# Revit family: ALWT_приток
name_source: partatom
category: Воздухораспределители
revit_build: Autodesk Revit 2014 (Build: 20130308_1515(x64)
units: mm (PartAtom-declared; Revit-internal decimal feet)

## types (1863) — shared parameters
A = 52 мм
URL = http://inplast.ru
margins = 10 мм
Изготовитель = INPLAST-SMAY
Материал = Алюминий_RAL9016 (INPLAST)
Описание = Решетка ALWT-алюминиевая защитная, угол выхода потока 15°

## per-type parameters (varying)
| type | Aef | C | C' | D | D' | Step 1 | Step 2 | n1 | n2 | Тип крепежа |
| ALWT-100х100-RAL9016 | 0.006 м² | 100 мм | 95 мм | 100 мм | 96 мм | 18 мм | 64 мм | 10 | 2 | саморезы |
| ALWT-125х100-RAL9016 | 0.008 м² | 125 мм | 120 мм | 100 мм | 96 мм | 23 мм | 80 мм | 10 | 2 | саморезы |
| ALWT-125х125-RAL9016 | 0.009 м² | 125 мм | 120 мм | 125 мм | 121 мм | 23 мм | 80 мм | 13 | 2 | саморезы |
| ALWT-150х100-RAL9016 | 0.009 м² | 150 мм | 145 мм | 100 мм | 96 мм | 27 мм | 95 мм | 10 | 2 | саморезы |
| ALWT-150х125-RAL9016 | 0.011 м² | 150 мм | 145 мм | 125 мм | 121 мм | 27 мм | 95 мм | 13 | 2 | саморезы |
| ALWT-150х150-RAL9016 | 0.014 м² | 150 мм | 145 мм | 150 мм | 146 мм | 27 мм | 95 мм | 15 | 2 | саморезы |
| ALWT-200х100-RAL9016 | 0.012 м² | 200 мм | 195 мм | 100 мм | 96 мм | 36 мм | 127 мм | 10 | 2 | саморезы |
| ALWT-200х125-RAL9016 | 0.015 м² | 200 мм | 195 мм | 125 мм | 121 мм | 36 мм | 127 мм | 13 | 2 | саморезы |
| ALWT-200х150-RAL9016 | 0.018 м² | 200 мм | 195 мм | 150 мм | 146 мм | 36 мм | 127 мм | 15 | 2 | саморезы |
| ALWT-200х200-RAL9016 | 0.024 м² | 200 мм | 195 мм | 200 мм | 196 мм | 36 мм | 127 мм | 20 | 2 | саморезы |
| ALWT-225х100-RAL9016 | 0.014 м² | 225 мм | 220 мм | 100 мм | 96 мм | 41 мм | 143 мм | 10 | 2 | саморезы |
| ALWT-225х125-RAL9016 | 0.017 м² | 225 мм | 220 мм | 125 мм | 121 мм | 41 мм | 143 мм | 13 | 2 | саморезы |
| ALWT-225х150-RAL9016 | 0.020 м² | 225 мм | 220 мм | 150 мм | 146 мм | 41 мм | 143 мм | 15 | 2 | саморезы |
| ALWT-225х200-RAL9016 | 0.027 м² | 225 мм | 220 мм | 200 мм | 196 мм | 41 мм | 143 мм | 20 | 2 | саморезы |
| ALWT-225х225-RAL9016 | 0.030 м² | 225 мм | 220 мм | 225 мм | 221 мм | 41 мм | 143 мм | 23 | 2 | саморезы |
| ALWT-250х100-RAL9016 | 0.015 м² | 250 мм | 245 мм | 100 мм | 96 мм | 45 мм | 159 мм | 10 | 2 | саморезы |
| ALWT-250х125-RAL9016 | 0.019 м² | 250 мм | 245 мм | 125 мм | 121 мм | 45 мм | 159 мм | 13 | 2 | саморезы |
| ALWT-250х150-RAL9016 | 0.023 м² | 250 мм | 245 мм | 150 мм | 146 мм | 45 мм | 159 мм | 15 | 2 | саморезы |
| ALWT-250х200-RAL9016 | 0.030 м² | 250 мм | 245 мм | 200 мм | 196 мм | 45 мм | 159 мм | 20 | 2 | саморезы |
| ALWT-250х225-RAL9016 | 0.034 м² | 250 мм | 245 мм | 225 мм | 221 мм | 45 мм | 159 мм | 23 | 2 | саморезы |
| ALWT-250х250-RAL9016 | 0.038 м² | 250 мм | 245 мм | 250 мм | 246 мм | 45 мм | 159 мм | 25 | 2 | саморезы |
| ALWT-300х100-RAL9016 | 0.018 м² | 300 мм | 295 мм | 100 мм | 96 мм | 55 мм | 191 мм | 10 | 2 | саморезы |
| ALWT-300х125-RAL9016 | 0.023 м² | 300 мм | 295 мм | 125 мм | 121 мм | 55 мм | 191 мм | 13 | 2 | саморезы |
| ALWT-300х150-RAL9016 | 0.027 м² | 300 мм | 295 мм | 150 мм | 146 мм | 55 мм | 191 мм | 15 | 2 | саморезы |
| ALWT-300х200-RAL9016 | 0.036 м² | 300 мм | 295 мм | 200 мм | 196 мм | 55 мм | 191 мм | 20 | 2 | саморезы |
| ALWT-300х225-RAL9016 | 0.041 м² | 300 мм | 295 мм | 225 мм | 221 мм | 55 мм | 191 мм | 23 | 2 | саморезы |
| ALWT-300х250-RAL9016 | 0.045 м² | 300 мм | 295 мм | 250 мм | 246 мм | 55 мм | 191 мм | 25 | 2 | саморезы |
| ALWT-300х300-RAL9016 | 0.054 м² | 300 мм | 295 мм | 300 мм | 296 мм | 55 мм | 191 мм | 30 | 2 | саморезы |
| ALWT-325х100-RAL9016 | 0.020 м² | 325 мм | 320 мм | 100 мм | 96 мм | 59 мм | 207 мм | 10 | 2 | саморезы |
| ALWT-325х125-RAL9016 | 0.024 м² | 325 мм | 320 мм | 125 мм | 121 мм | 59 мм | 207 мм | 13 | 2 | саморезы |
| ALWT-325х150-RAL9016 | 0.029 м² | 325 мм | 320 мм | 150 мм | 146 мм | 59 мм | 207 мм | 15 | 2 | саморезы |
| ALWT-325х200-RAL9016 | 0.039 м² | 325 мм | 320 мм | 200 мм | 196 мм | 59 мм | 207 мм | 20 | 2 | саморезы |
| ALWT-325х225-RAL9016 | 0.044 м² | 325 мм | 320 мм | 225 мм | 221 мм | 59 мм | 207 мм | 23 | 2 | саморезы |
| ALWT-325х250-RAL9016 | 0.049 м² | 325 мм | 320 мм | 250 мм | 246 мм | 59 мм | 207 мм | 25 | 2 | саморезы |
| ALWT-325х300-RAL9016 | 0.059 м² | 325 мм | 320 мм | 300 мм | 296 мм | 59 мм | 207 мм | 30 | 2 | саморезы |
| ALWT-325х325-RAL9016 | 0.064 м² | 325 мм | 320 мм | 325 мм | 321 мм | 59 мм | 207 мм | 33 | 2 | саморезы |
| ALWT-350х100-RAL9016 | 0.021 м² | 350 мм | 345 мм | 100 мм | 96 мм | 64 мм | 223 мм | 10 | 2 | саморезы |
| ALWT-350х125-RAL9016 | 0.026 м² | 350 мм | 345 мм | 125 мм | 121 мм | 64 мм | 223 мм | 13 | 2 | саморезы |
| ALWT-350х150-RAL9016 | 0.032 м² | 350 мм | 345 мм | 150 мм | 146 мм | 64 мм | 223 мм | 15 | 2 | саморезы |
| ALWT-350х200-RAL9016 | 0.042 м² | 350 мм | 345 мм | 200 мм | 196 мм | 64 мм | 223 мм | 20 | 2 | саморезы |
| ALWT-350х225-RAL9016 | 0.047 м² | 350 мм | 345 мм | 225 мм | 221 мм | 64 мм | 223 мм | 23 | 2 | саморезы |
| ALWT-350х250-RAL9016 | 0.053 м² | 350 мм | 345 мм | 250 мм | 246 мм | 64 мм | 223 мм | 25 | 2 | саморезы |
| ALWT-350х300-RAL9016 | 0.063 м² | 350 мм | 345 мм | 300 мм | 296 мм | 64 мм | 223 мм | 30 | 2 | саморезы |
| ALWT-350х325-RAL9016 | 0.068 м² | 350 мм | 345 мм | 325 мм | 321 мм | 64 мм | 223 мм | 33 | 2 | саморезы |
| ALWT-350х350-RAL9016 | 0.074 м² | 350 мм | 345 мм | 350 мм | 346 мм | 64 мм | 223 мм | 35 | 2 | саморезы |
| ALWT-400х100-RAL9016 | 0.024 м² | 400 мм | 395 мм | 100 мм | 96 мм | 73 мм | 255 мм | 10 | 3 | саморезы |
| ALWT-400х125-RAL9016 | 0.030 м² | 400 мм | 395 мм | 125 мм | 121 мм | 73 мм | 255 мм | 13 | 3 | саморезы |
| ALWT-400х150-RAL9016 | 0.036 м² | 400 мм | 395 мм | 150 мм | 146 мм | 73 мм | 255 мм | 15 | 3 | саморезы |
| ALWT-400х200-RAL9016 | 0.048 м² | 400 мм | 395 мм | 200 мм | 196 мм | 73 мм | 255 мм | 20 | 3 | саморезы |
| ALWT-400х225-RAL9016 | 0.054 м² | 400 мм | 395 мм | 225 мм | 221 мм | 73 мм | 255 мм | 23 | 3 | саморезы |
| ALWT-400х250-RAL9016 | 0.060 м² | 400 мм | 395 мм | 250 мм | 246 мм | 73 мм | 255 мм | 25 | 3 | саморезы |
| ALWT-400х300-RAL9016 | 0.072 м² | 400 мм | 395 мм | 300 мм | 296 мм | 73 мм | 255 мм | 30 | 3 | саморезы |
| ALWT-400х325-RAL9016 | 0.078 м² | 400 мм | 395 мм | 325 мм | 321 мм | 73 мм | 255 мм | 33 | 3 | саморезы |
| ALWT-400х350-RAL9016 | 0.084 м² | 400 мм | 395 мм | 350 мм | 346 мм | 73 мм | 255 мм | 35 | 3 | саморезы |
| ALWT-400х400-RAL9016 | 0.096 м² | 400 мм | 395 мм | 400 мм | 396 мм | 73 мм | 255 мм | 40 | 3 | саморезы |
| ALWT-425х100-RAL9016 | 0.026 м² | 425 мм | 420 мм | 100 мм | 96 мм | 77 мм | 270 мм | 10 | 3 | саморезы |
| ALWT-425х125-RAL9016 | 0.032 м² | 425 мм | 420 мм | 125 мм | 121 мм | 77 мм | 270 мм | 13 | 3 | саморезы |
| ALWT-425х150-RAL9016 | 0.038 м² | 425 мм | 420 мм | 150 мм | 146 мм | 77 мм | 270 мм | 15 | 3 | саморезы |
| ALWT-425х200-RAL9016 | 0.051 м² | 425 мм | 420 мм | 200 мм | 196 мм | 77 мм | 270 мм | 20 | 3 | саморезы |
| ALWT-425х225-RAL9016 | 0.058 м² | 425 мм | 420 мм | 225 мм | 221 мм | 77 мм | 270 мм | 23 | 3 | саморезы |
| ALWT-425х250-RAL9016 | 0.064 м² | 425 мм | 420 мм | 250 мм | 246 мм | 77 мм | 270 мм | 25 | 3 | саморезы |
| ALWT-425х300-RAL9016 | 0.077 м² | 425 мм | 420 мм | 300 мм | 296 мм | 77 мм | 270 мм | 30 | 3 | саморезы |
| ALWT-425х325-RAL9016 | 0.083 м² | 425 мм | 420 мм | 325 мм | 321 мм | 77 мм | 270 мм | 33 | 3 | саморезы |
| ALWT-425х350-RAL9016 | 0.089 м² | 425 мм | 420 мм | 350 мм | 346 мм | 77 мм | 270 мм | 35 | 3 | саморезы |
| ALWT-425х400-RAL9016 | 0.102 м² | 425 мм | 420 мм | 400 мм | 396 мм | 77 мм | 270 мм | 40 | 3 | саморезы |
| ALWT-425х425-RAL9016 | 0.109 м² | 425 мм | 420 мм | 425 мм | 421 мм | 77 мм | 270 мм | 43 | 3 | саморезы |
| ALWT-450х100-RAL9016 | 0.027 м² | 450 мм | 445 мм | 100 мм | 96 мм | 82 мм | 286 мм | 10 | 3 | саморезы |
| ALWT-450х125-RAL9016 | 0.034 м² | 450 мм | 445 мм | 125 мм | 121 мм | 82 мм | 286 мм | 13 | 3 | саморезы |
| ALWT-450х150-RAL9016 | 0.041 м² | 450 мм | 445 мм | 150 мм | 146 мм | 82 мм | 286 мм | 15 | 3 | саморезы |
| ALWT-450х200-RAL9016 | 0.054 м² | 450 мм | 445 мм | 200 мм | 196 мм | 82 мм | 286 мм | 20 | 3 | саморезы |
| ALWT-450х225-RAL9016 | 0.061 м² | 450 мм | 445 мм | 225 мм | 221 мм | 82 мм | 286 мм | 23 | 3 | саморезы |
| ALWT-450х250-RAL9016 | 0.068 м² | 450 мм | 445 мм | 250 мм | 246 мм | 82 мм | 286 мм | 25 | 3 | саморезы |
| ALWT-450х300-RAL9016 | 0.081 м² | 450 мм | 445 мм | 300 мм | 296 мм | 82 мм | 286 мм | 30 | 3 | саморезы |
| ALWT-450х325-RAL9016 | 0.088 м² | 450 мм | 445 мм | 325 мм | 321 мм | 82 мм | 286 мм | 33 | 3 | саморезы |
| ALWT-450х350-RAL9016 | 0.095 м² | 450 мм | 445 мм | 350 мм | 346 мм | 82 мм | 286 мм | 35 | 3 | саморезы |
| ALWT-450х400-RAL9016 | 0.108 м² | 450 мм | 445 мм | 400 мм | 396 мм | 82 мм | 286 мм | 40 | 3 | саморезы |
| ALWT-450х425-RAL9016 | 0.115 м² | 450 мм | 445 мм | 425 мм | 421 мм | 82 мм | 286 мм | 43 | 3 | саморезы |
| ALWT-450х450-RAL9016 | 0.122 м² | 450 мм | 445 мм | 450 мм | 446 мм | 82 мм | 286 мм | 45 | 3 | саморезы |
| ALWT-500х100-RAL9016 | 0.030 м² | 500 мм | 495 мм | 100 мм | 96 мм | 91 мм | 318 мм | 10 | 3 | саморезы |
| ALWT-500х125-RAL9016 | 0.038 м² | 500 мм | 495 мм | 125 мм | 121 мм | 91 мм | 318 мм | 13 | 3 | саморезы |
| ALWT-500х150-RAL9016 | 0.045 м² | 500 мм | 495 мм | 150 мм | 146 мм | 91 мм | 318 мм | 15 | 3 | саморезы |
| ALWT-500х200-RAL9016 | 0.060 м² | 500 мм | 495 мм | 200 мм | 196 мм | 91 мм | 318 мм | 20 | 3 | саморезы |
| ALWT-500х225-RAL9016 | 0.068 м² | 500 мм | 495 мм | 225 мм | 221 мм | 91 мм | 318 мм | 23 | 3 | саморезы |
| ALWT-500х250-RAL9016 | 0.075 м² | 500 мм | 495 мм | 250 мм | 246 мм | 91 мм | 318 мм | 25 | 3 | саморезы |
| ALWT-500х300-RAL9016 | 0.090 м² | 500 мм | 495 мм | 300 мм | 296 мм | 91 мм | 318 мм | 30 | 3 | саморезы |
| ALWT-500х325-RAL9016 | 0.098 м² | 500 мм | 495 мм | 325 мм | 321 мм | 91 мм | 318 мм | 33 | 3 | саморезы |
| ALWT-500х350-RAL9016 | 0.105 м² | 500 мм | 495 мм | 350 мм | 346 мм | 91 мм | 318 мм | 35 | 3 | саморезы |
| ALWT-500х400-RAL9016 | 0.120 м² | 500 мм | 495 мм | 400 мм | 396 мм | 91 мм | 318 мм | 40 | 3 | саморезы |
| ALWT-500х425-RAL9016 | 0.128 м² | 500 мм | 495 мм | 425 мм | 421 мм | 91 мм | 318 мм | 43 | 3 | саморезы |
| ALWT-500х450-RAL9016 | 0.135 м² | 500 мм | 495 мм | 450 мм | 446 мм | 91 мм | 318 мм | 45 | 3 | саморезы |
| ALWT-500х500-RAL9016 | 0.150 м² | 500 мм | 495 мм | 500 мм | 496 мм | 91 мм | 318 мм | 50 | 3 | саморезы |
| ALWT-525х100-RAL9016 | 0.032 м² | 525 мм | 520 мм | 100 мм | 96 мм | 95 мм | 334 мм | 10 | 3 | саморезы |
| ALWT-525х125-RAL9016 | 0.039 м² | 525 мм | 520 мм | 125 мм | 121 мм | 95 мм | 334 мм | 13 | 3 | саморезы |
| ALWT-525х150-RAL9016 | 0.047 м² | 525 мм | 520 мм | 150 мм | 146 мм | 95 мм | 334 мм | 15 | 3 | саморезы |
| ALWT-525х200-RAL9016 | 0.063 м² | 525 мм | 520 мм | 200 мм | 196 мм | 95 мм | 334 мм | 20 | 3 | саморезы |
| ALWT-525х225-RAL9016 | 0.071 м² | 525 мм | 520 мм | 225 мм | 221 мм | 95 мм | 334 мм | 23 | 3 | саморезы |
| ALWT-525х250-RAL9016 | 0.079 м² | 525 мм | 520 мм | 250 мм | 246 мм | 95 мм | 334 мм | 25 | 3 | саморезы |
| ALWT-525х300-RAL9016 | 0.095 м² | 525 мм | 520 мм | 300 мм | 296 мм | 95 мм | 334 мм | 30 | 3 | саморезы |
| ALWT-525х325-RAL9016 | 0.103 м² | 525 мм | 520 мм | 325 мм | 321 мм | 95 мм | 334 мм | 33 | 3 | саморезы |
| ALWT-525х350-RAL9016 | 0.111 м² | 525 мм | 520 мм | 350 мм | 346 мм | 95 мм | 334 мм | 35 | 3 | саморезы |
| ALWT-525х400-RAL9016 | 0.126 м² | 525 мм | 520 мм | 400 мм | 396 мм | 95 мм | 334 мм | 40 | 3 | саморезы |
| ALWT-525х425-RAL9016 | 0.134 м² | 525 мм | 520 мм | 425 мм | 421 мм | 95 мм | 334 мм | 43 | 3 | саморезы |
| ALWT-525х450-RAL9016 | 0.142 м² | 525 мм | 520 мм | 450 мм | 446 мм | 95 мм | 334 мм | 45 | 3 | саморезы |
| ALWT-525х500-RAL9016 | 0.158 м² | 525 мм | 520 мм | 500 мм | 496 мм | 95 мм | 334 мм | 50 | 3 | саморезы |
| ALWT-525х525-RAL9016 | 0.166 м² | 525 мм | 520 мм | 525 мм | 521 мм | 95 мм | 334 мм | 53 | 3 | саморезы |
| ALWT-550х100-RAL9016 | 0.033 м² | 550 мм | 545 мм | 100 мм | 96 мм | 100 мм | 350 мм | 10 | 3 | саморезы |
| ALWT-550х125-RAL9016 | 0.041 м² | 550 мм | 545 мм | 125 мм | 121 мм | 100 мм | 350 мм | 13 | 3 | саморезы |
| ALWT-550х150-RAL9016 | 0.050 м² | 550 мм | 545 мм | 150 мм | 146 мм | 100 мм | 350 мм | 15 | 3 | саморезы |
| ALWT-550х200-RAL9016 | 0.066 м² | 550 мм | 545 мм | 200 мм | 196 мм | 100 мм | 350 мм | 20 | 3 | саморезы |
| ALWT-550х225-RAL9016 | 0.074 м² | 550 мм | 545 мм | 225 мм | 221 мм | 100 мм | 350 мм | 23 | 3 | саморезы |
| ALWT-550х250-RAL9016 | 0.083 м² | 550 мм | 545 мм | 250 мм | 246 мм | 100 мм | 350 мм | 25 | 3 | саморезы |
| ALWT-550х300-RAL9016 | 0.099 м² | 550 мм | 545 мм | 300 мм | 296 мм | 100 мм | 350 мм | 30 | 3 | саморезы |
| ALWT-550х325-RAL9016 | 0.108 м² | 550 мм | 545 мм | 325 мм | 321 мм | 100 мм | 350 мм | 33 | 3 | саморезы |
| ALWT-550х350-RAL9016 | 0.116 м² | 550 мм | 545 мм | 350 мм | 346 мм | 100 мм | 350 мм | 35 | 3 | саморезы |
| ALWT-550х400-RAL9016 | 0.132 м² | 550 мм | 545 мм | 400 мм | 396 мм | 100 мм | 350 мм | 40 | 3 | саморезы |
| ALWT-550х425-RAL9016 | 0.141 м² | 550 мм | 545 мм | 425 мм | 421 мм | 100 мм | 350 мм | 43 | 3 | саморезы |
| ALWT-550х450-RAL9016 | 0.149 м² | 550 мм | 545 мм | 450 мм | 446 мм | 100 мм | 350 мм | 45 | 3 | саморезы |
| ALWT-550х500-RAL9016 | 0.165 м² | 550 мм | 545 мм | 500 мм | 496 мм | 100 мм | 350 мм | 50 | 3 | саморезы |
| ALWT-550х525-RAL9016 | 0.174 м² | 550 мм | 545 мм | 525 мм | 521 мм | 100 мм | 350 мм | 53 | 3 | саморезы |
| ALWT-550х550-RAL9016 | 0.182 м² | 550 мм | 545 мм | 550 мм | 546 мм | 100 мм | 350 мм | 55 | 3 | саморезы |
| ALWT-600х100-RAL9016 | 0.036 м² | 600 мм | 595 мм | 100 мм | 96 мм | 109 мм | 382 мм | 10 | 3 | саморезы |
| ALWT-600х125-RAL9016 | 0.045 м² | 600 мм | 595 мм | 125 мм | 121 мм | 109 мм | 382 мм | 13 | 3 | саморезы |
| ALWT-600х150-RAL9016 | 0.054 м² | 600 мм | 595 мм | 150 мм | 146 мм | 109 мм | 382 мм | 15 | 3 | саморезы |
| ALWT-600х200-RAL9016 | 0.072 м² | 600 мм | 595 мм | 200 мм | 196 мм | 109 мм | 382 мм | 20 | 3 | саморезы |
| ALWT-600х225-RAL9016 | 0.081 м² | 600 мм | 595 мм | 225 мм | 221 мм | 109 мм | 382 мм | 23 | 3 | саморезы |
| ALWT-600х250-RAL9016 | 0.090 м² | 600 мм | 595 мм | 250 мм | 246 мм | 109 мм | 382 мм | 25 | 3 | саморезы |
| ALWT-600х300-RAL9016 | 0.108 м² | 600 мм | 595 мм | 300 мм | 296 мм | 109 мм | 382 мм | 30 | 3 | саморезы |
| ALWT-600х325-RAL9016 | 0.117 м² | 600 мм | 595 мм | 325 мм | 321 мм | 109 мм | 382 мм | 33 | 3 | саморезы |
| ALWT-600х350-RAL9016 | 0.126 м² | 600 мм | 595 мм | 350 мм | 346 мм | 109 мм | 382 мм | 35 | 3 | саморезы |
| ALWT-600х400-RAL9016 | 0.144 м² | 600 мм | 595 мм | 400 мм | 396 мм | 109 мм | 382 мм | 40 | 3 | саморезы |
| ALWT-600х425-RAL9016 | 0.153 м² | 600 мм | 595 мм | 425 мм | 421 мм | 109 мм | 382 мм | 43 | 3 | саморезы |
| ALWT-600х450-RAL9016 | 0.162 м² | 600 мм | 595 мм | 450 мм | 446 мм | 109 мм | 382 мм | 45 | 3 | саморезы |
| ALWT-600х500-RAL9016 | 0.180 м² | 600 мм | 595 мм | 500 мм | 496 мм | 109 мм | 382 мм | 50 | 3 | саморезы |
| ALWT-600х525-RAL9016 | 0.190 м² | 600 мм | 595 мм | 525 мм | 521 мм | 109 мм | 382 мм | 53 | 3 | саморезы |
| ALWT-600х550-RAL9016 | 0.199 м² | 600 мм | 595 мм | 550 мм | 546 мм | 109 мм | 382 мм | 55 | 3 | саморезы |
| ALWT-600х600-RAL9016 | 0.217 м² | 600 мм | 595 мм | 600 мм | 596 мм | 109 мм | 382 мм | 60 | 3 | саморезы |
| ALWT-625х100-RAL9016 | 0.038 м² | 625 мм | 620 мм | 100 мм | 96 мм | 114 мм | 398 мм | 10 | 3 | саморезы |
| ALWT-625х125-RAL9016 | 0.047 м² | 625 мм | 620 мм | 125 мм | 121 мм | 114 мм | 398 мм | 13 | 3 | саморезы |
| ALWT-625х150-RAL9016 | 0.056 м² | 625 мм | 620 мм | 150 мм | 146 мм | 114 мм | 398 мм | 15 | 3 | саморезы |
| ALWT-625х200-RAL9016 | 0.075 м² | 625 мм | 620 мм | 200 мм | 196 мм | 114 мм | 398 мм | 20 | 3 | саморезы |
| ALWT-625х225-RAL9016 | 0.085 м² | 625 мм | 620 мм | 225 мм | 221 мм | 114 мм | 398 мм | 23 | 3 | саморезы |
| ALWT-625х250-RAL9016 | 0.094 м² | 625 мм | 620 мм | 250 мм | 246 мм | 114 мм | 398 мм | 25 | 3 | саморезы |
| ALWT-625х300-RAL9016 | 0.113 м² | 625 мм | 620 мм | 300 мм | 296 мм | 114 мм | 398 мм | 30 | 3 | саморезы |
| ALWT-625х325-RAL9016 | 0.122 м² | 625 мм | 620 мм | 325 мм | 321 мм | 114 мм | 398 мм | 33 | 3 | саморезы |
| ALWT-625х350-RAL9016 | 0.132 м² | 625 мм | 620 мм | 350 мм | 346 мм | 114 мм | 398 мм | 35 | 3 | саморезы |
| ALWT-625х400-RAL9016 | 0.150 м² | 625 мм | 620 мм | 400 мм | 396 мм | 114 мм | 398 мм | 40 | 3 | саморезы |
| ALWT-625х425-RAL9016 | 0.160 м² | 625 мм | 620 мм | 425 мм | 421 мм | 114 мм | 398 мм | 43 | 3 | саморезы |
| ALWT-625х450-RAL9016 | 0.169 м² | 625 мм | 620 мм | 450 мм | 446 мм | 114 мм | 398 мм | 45 | 3 | саморезы |
| ALWT-625х500-RAL9016 | 0.188 м² | 625 мм | 620 мм | 500 мм | 496 мм | 114 мм | 398 мм | 50 | 3 | саморезы |
| ALWT-625х525-RAL9016 | 0.197 м² | 625 мм | 620 мм | 525 мм | 521 мм | 114 мм | 398 мм | 53 | 3 | саморезы |
| ALWT-625х550-RAL9016 | 0.207 м² | 625 мм | 620 мм | 550 мм | 546 мм | 114 мм | 398 мм | 55 | 3 | саморезы |
| ALWT-625х600-RAL9016 | 0.226 м² | 625 мм | 620 мм | 600 мм | 596 мм | 114 мм | 398 мм | 60 | 3 | саморезы |
| ALWT-625х625-RAL9016 | 0.235 м² | 625 мм | 620 мм | 625 мм | 621 мм | 114 мм | 398 мм | 63 | 3 | саморезы |
| ALWT-650х100-RAL9016 | 0.039 м² | 650 мм | 645 мм | 100 мм | 96 мм | 118 мм | 414 мм | 10 | 3 | саморезы |
| ALWT-650х125-RAL9016 | 0.049 м² | 650 мм | 645 мм | 125 мм | 121 мм | 118 мм | 414 мм | 13 | 3 | саморезы |
| ALWT-650х150-RAL9016 | 0.059 м² | 650 мм | 645 мм | 150 мм | 146 мм | 118 мм | 414 мм | 15 | 3 | саморезы |
| ALWT-650х200-RAL9016 | 0.078 м² | 650 мм | 645 мм | 200 мм | 196 мм | 118 мм | 414 мм | 20 | 3 | саморезы |
| ALWT-650х225-RAL9016 | 0.088 м² | 650 мм | 645 мм | 225 мм | 221 мм | 118 мм | 414 мм | 23 | 3 | саморезы |
| ALWT-650х250-RAL9016 | 0.098 м² | 650 мм | 645 мм | 250 мм | 246 мм | 118 мм | 414 мм | 25 | 3 | саморезы |
| ALWT-650х300-RAL9016 | 0.117 м² | 650 мм | 645 мм | 300 мм | 296 мм | 118 мм | 414 мм | 30 | 3 | саморезы |
| ALWT-650х325-RAL9016 | 0.127 м² | 650 мм | 645 мм | 325 мм | 321 мм | 118 мм | 414 мм | 33 | 3 | саморезы |
| ALWT-650х350-RAL9016 | 0.137 м² | 650 мм | 645 мм | 350 мм | 346 мм | 118 мм | 414 мм | 35 | 3 | саморезы |
| ALWT-650х400-RAL9016 | 0.156 м² | 650 мм | 645 мм | 400 мм | 396 мм | 118 мм | 414 мм | 40 | 3 | саморезы |
| ALWT-650х425-RAL9016 | 0.166 м² | 650 мм | 645 мм | 425 мм | 421 мм | 118 мм | 414 мм | 43 | 3 | саморезы |
| ALWT-650х450-RAL9016 | 0.176 м² | 650 мм | 645 мм | 450 мм | 446 мм | 118 мм | 414 мм | 45 | 3 | саморезы |
| ALWT-650х500-RAL9016 | 0.196 м² | 650 мм | 645 мм | 500 мм | 496 мм | 118 мм | 414 мм | 50 | 3 | саморезы |
| ALWT-650х525-RAL9016 | 0.205 м² | 650 мм | 645 мм | 525 мм | 521 мм | 118 мм | 414 мм | 53 | 3 | саморезы |
| ALWT-650х550-RAL9016 | 0.215 м² | 650 мм | 645 мм | 550 мм | 546 мм | 118 мм | 414 мм | 55 | 3 | саморезы |
| ALWT-650х600-RAL9016 | 0.235 м² | 650 мм | 645 мм | 600 мм | 596 мм | 118 мм | 414 мм | 60 | 3 | саморезы |
| ALWT-650х625-RAL9016 | 0.244 м² | 650 мм | 645 мм | 625 мм | 621 мм | 118 мм | 414 мм | 63 | 3 | саморезы |
| ALWT-650х650-RAL9016 | 0.254 м² | 650 мм | 645 мм | 650 мм | 646 мм | 118 мм | 414 мм | 65 | 3 | саморезы |
| ALWT-700х100-RAL9016 | 0.042 м² | 700 мм | 695 мм | 100 мм | 96 мм | 127 мм | 445 мм | 10 | 3 | саморезы |
| ALWT-700х125-RAL9016 | 0.053 м² | 700 мм | 695 мм | 125 мм | 121 мм | 127 мм | 445 мм | 13 | 3 | саморезы |
| ALWT-700х150-RAL9016 | 0.063 м² | 700 мм | 695 мм | 150 мм | 146 мм | 127 мм | 445 мм | 15 | 3 | саморезы |
| ALWT-700х200-RAL9016 | 0.084 м² | 700 мм | 695 мм | 200 мм | 196 мм | 127 мм | 445 мм | 20 | 3 | саморезы |
| ALWT-700х225-RAL9016 | 0.095 м² | 700 мм | 695 мм | 225 мм | 221 мм | 127 мм | 445 мм | 23 | 3 | саморезы |
| ALWT-700х250-RAL9016 | 0.105 м² | 700 мм | 695 мм | 250 мм | 246 мм | 127 мм | 445 мм | 25 | 3 | саморезы |
| ALWT-700х300-RAL9016 | 0.126 м² | 700 мм | 695 мм | 300 мм | 296 мм | 127 мм | 445 мм | 30 | 3 | саморезы |
| ALWT-700х325-RAL9016 | 0.137 м² | 700 мм | 695 мм | 325 мм | 321 мм | 127 мм | 445 мм | 33 | 3 | саморезы |
| ALWT-700х350-RAL9016 | 0.147 м² | 700 мм | 695 мм | 350 мм | 346 мм | 127 мм | 445 мм | 35 | 3 | саморезы |
| ALWT-700х400-RAL9016 | 0.168 м² | 700 мм | 695 мм | 400 мм | 396 мм | 127 мм | 445 мм | 40 | 3 | саморезы |
| ALWT-700х425-RAL9016 | 0.179 м² | 700 мм | 695 мм | 425 мм | 421 мм | 127 мм | 445 мм | 43 | 3 | саморезы |
| ALWT-700х450-RAL9016 | 0.190 м² | 700 мм | 695 мм | 450 мм | 446 мм | 127 мм | 445 мм | 45 | 3 | саморезы |
| ALWT-700х500-RAL9016 | 0.211 м² | 700 мм | 695 мм | 500 мм | 496 мм | 127 мм | 445 мм | 50 | 3 | саморезы |
| ALWT-700х525-RAL9016 | 0.221 м² | 700 мм | 695 мм | 525 мм | 521 мм | 127 мм | 445 мм | 53 | 3 | саморезы |
| ALWT-700х550-RAL9016 | 0.232 м² | 700 мм | 695 мм | 550 мм | 546 мм | 127 мм | 445 мм | 55 | 3 | саморезы |
| ALWT-700х600-RAL9016 | 0.253 м² | 700 мм | 695 мм | 600 мм | 596 мм | 127 мм | 445 мм | 60 | 3 | саморезы |
| ALWT-700х625-RAL9016 | 0.263 м² | 700 мм | 695 мм | 625 мм | 621 мм | 127 мм | 445 мм | 63 | 3 | саморезы |
| ALWT-700х650-RAL9016 | 0.274 м² | 700 мм | 695 мм | 650 мм | 646 мм | 127 мм | 445 мм | 65 | 3 | саморезы |
| ALWT-725х100-RAL9016 | 0.044 м² | 725 мм | 720 мм | 100 мм | 96 мм | 132 мм | 461 мм | 10 | 3 | саморезы |
| ALWT-725х125-RAL9016 | 0.055 м² | 725 мм | 720 мм | 125 мм | 121 мм | 132 мм | 461 мм | 13 | 3 | саморезы |
| ALWT-725х150-RAL9016 | 0.065 м² | 725 мм | 720 мм | 150 мм | 146 мм | 132 мм | 461 мм | 15 | 3 | саморезы |
| ALWT-725х200-RAL9016 | 0.087 м² | 725 мм | 720 мм | 200 мм | 196 мм | 132 мм | 461 мм | 20 | 3 | саморезы |
| ALWT-725х225-RAL9016 | 0.098 м² | 725 мм | 720 мм | 225 мм | 221 мм | 132 мм | 461 мм | 23 | 3 | саморезы |
| ALWT-725х250-RAL9016 | 0.109 м² | 725 мм | 720 мм | 250 мм | 246 мм | 132 мм | 461 мм | 25 | 3 | саморезы |
| ALWT-725х300-RAL9016 | 0.131 м² | 725 мм | 720 мм | 300 мм | 296 мм | 132 мм | 461 мм | 30 | 3 | саморезы |
| ALWT-725х325-RAL9016 | 0.142 м² | 725 мм | 720 мм | 325 мм | 321 мм | 132 мм | 461 мм | 33 | 3 | саморезы |
| ALWT-725х350-RAL9016 | 0.153 м² | 725 мм | 720 мм | 350 мм | 346 мм | 132 мм | 461 мм | 35 | 3 | саморезы |
| ALWT-725х400-RAL9016 | 0.174 м² | 725 мм | 720 мм | 400 мм | 396 мм | 132 мм | 461 мм | 40 | 3 | саморезы |
| ALWT-725х425-RAL9016 | 0.185 м² | 725 мм | 720 мм | 425 мм | 421 мм | 132 мм | 461 мм | 43 | 3 | саморезы |
| ALWT-725х450-RAL9016 | 0.196 м² | 725 мм | 720 мм | 450 мм | 446 мм | 132 мм | 461 мм | 45 | 3 | саморезы |
| ALWT-725х500-RAL9016 | 0.218 м² | 725 мм | 720 мм | 500 мм | 496 мм | 132 мм | 461 мм | 50 | 3 | саморезы |
| ALWT-725х525-RAL9016 | 0.229 м² | 725 мм | 720 мм | 525 мм | 521 мм | 132 мм | 461 мм | 53 | 3 | саморезы |
| ALWT-725х550-RAL9016 | 0.240 м² | 725 мм | 720 мм | 550 мм | 546 мм | 132 мм | 461 мм | 55 | 3 | саморезы |
| ALWT-725х600-RAL9016 | 0.262 м² | 725 мм | 720 мм | 600 мм | 596 мм | 132 мм | 461 мм | 60 | 3 | саморезы |
| ALWT-725х625-RAL9016 | 0.273 м² | 725 мм | 720 мм | 625 мм | 621 мм | 132 мм | 461 мм | 63 | 3 | саморезы |
| ALWT-725х650-RAL9016 | 0.284 м² | 725 мм | 720 мм | 650 мм | 646 мм | 132 мм | 461 мм | 65 | 3 | саморезы |
| ALWT-750х100-RAL9016 | 0.045 м² | 750 мм | 745 мм | 100 мм | 96 мм | 136 мм | 477 мм | 10 | 3 | саморезы |
| ALWT-750х125-RAL9016 | 0.056 м² | 750 мм | 745 мм | 125 мм | 121 мм | 136 мм | 477 мм | 13 | 3 | саморезы |
| ALWT-750х150-RAL9016 | 0.068 м² | 750 мм | 745 мм | 150 мм | 146 мм | 136 мм | 477 мм | 15 | 3 | саморезы |
| ALWT-750х200-RAL9016 | 0.090 м² | 750 мм | 745 мм | 200 мм | 196 мм | 136 мм | 477 мм | 20 | 3 | саморезы |
| ALWT-750х225-RAL9016 | 0.102 м² | 750 мм | 745 мм | 225 мм | 221 мм | 136 мм | 477 мм | 23 | 3 | саморезы |
| ALWT-750х250-RAL9016 | 0.113 м² | 750 мм | 745 мм | 250 мм | 246 мм | 136 мм | 477 мм | 25 | 3 | саморезы |
| ALWT-750х300-RAL9016 | 0.135 м² | 750 мм | 745 мм | 300 мм | 296 мм | 136 мм | 477 мм | 30 | 3 | саморезы |
| ALWT-750х325-RAL9016 | 0.147 м² | 750 мм | 745 мм | 325 мм | 321 мм | 136 мм | 477 мм | 33 | 3 | саморезы |
| ALWT-750х350-RAL9016 | 0.158 м² | 750 мм | 745 мм | 350 мм | 346 мм | 136 мм | 477 мм | 35 | 3 | саморезы |
| ALWT-750х400-RAL9016 | 0.180 м² | 750 мм | 745 мм | 400 мм | 396 мм | 136 мм | 477 мм | 40 | 3 | саморезы |
| ALWT-750х425-RAL9016 | 0.192 м² | 750 мм | 745 мм | 425 мм | 421 мм | 136 мм | 477 мм | 43 | 3 | саморезы |
| ALWT-750х450-RAL9016 | 0.203 м² | 750 мм | 745 мм | 450 мм | 446 мм | 136 мм | 477 мм | 45 | 3 | саморезы |
| ALWT-750х500-RAL9016 | 0.226 м² | 750 мм | 745 мм | 500 мм | 496 мм | 136 мм | 477 мм | 50 | 3 | саморезы |
| ALWT-750х525-RAL9016 | 0.237 м² | 750 мм | 745 мм | 525 мм | 521 мм | 136 мм | 477 мм | 53 | 3 | саморезы |
| ALWT-750х550-RAL9016 | 0.248 м² | 750 мм | 745 мм | 550 мм | 546 мм | 136 мм | 477 мм | 55 | 3 | саморезы |
| ALWT-750х600-RAL9016 | 0.271 м² | 750 мм | 745 мм | 600 мм | 596 мм | 136 мм | 477 мм | 60 | 3 | саморезы |
| ALWT-750х625-RAL9016 | 0.282 м² | 750 мм | 745 мм | 625 мм | 621 мм | 136 мм | 477 мм | 63 | 3 | саморезы |
| ALWT-750х650-RAL9016 | 0.293 м² | 750 мм | 745 мм | 650 мм | 646 мм | 136 мм | 477 мм | 65 | 3 | саморезы |
| ALWT-800х100-RAL9016 | 0.048 м² | 800 мм | 795 мм | 100 мм | 96 мм | 145 мм | 509 мм | 10 | 4 | саморезы |
| ALWT-800х125-RAL9016 | 0.060 м² | 800 мм | 795 мм | 125 мм | 121 мм | 145 мм | 509 мм | 13 | 4 | саморезы |
| ALWT-800х150-RAL9016 | 0.072 м² | 800 мм | 795 мм | 150 мм | 146 мм | 145 мм | 509 мм | 15 | 4 | саморезы |
| ALWT-800х200-RAL9016 | 0.096 м² | 800 мм | 795 мм | 200 мм | 196 мм | 145 мм | 509 мм | 20 | 4 | саморезы |
| ALWT-800х225-RAL9016 | 0.108 м² | 800 мм | 795 мм | 225 мм | 221 мм | 145 мм | 509 мм | 23 | 4 | саморезы |
| ALWT-800х250-RAL9016 | 0.120 м² | 800 мм | 795 мм | 250 мм | 246 мм | 145 мм | 509 мм | 25 | 4 | саморезы |
| ALWT-800х300-RAL9016 | 0.144 м² | 800 мм | 795 мм | 300 мм | 296 мм | 145 мм | 509 мм | 30 | 4 | саморезы |
| ALWT-800х325-RAL9016 | 0.156 м² | 800 мм | 795 мм | 325 мм | 321 мм | 145 мм | 509 мм | 33 | 4 | саморезы |
| ALWT-800х350-RAL9016 | 0.168 м² | 800 мм | 795 мм | 350 мм | 346 мм | 145 мм | 509 мм | 35 | 4 | саморезы |
| ALWT-800х400-RAL9016 | 0.193 м² | 800 мм | 795 мм | 400 мм | 396 мм | 145 мм | 509 мм | 40 | 4 | саморезы |
| ALWT-800х425-RAL9016 | 0.205 м² | 800 мм | 795 мм | 425 мм | 421 мм | 145 мм | 509 мм | 43 | 4 | саморезы |
| ALWT-800х450-RAL9016 | 0.217 м² | 800 мм | 795 мм | 450 мм | 446 мм | 145 мм | 509 мм | 45 | 4 | саморезы |
| ALWT-800х500-RAL9016 | 0.241 м² | 800 мм | 795 мм | 500 мм | 496 мм | 145 мм | 509 мм | 50 | 4 | саморезы |
| ALWT-800х525-RAL9016 | 0.253 м² | 800 мм | 795 мм | 525 мм | 521 мм | 145 мм | 509 мм | 53 | 4 | саморезы |
| ALWT-800х550-RAL9016 | 0.265 м² | 800 мм | 795 мм | 550 мм | 546 мм | 145 мм | 509 мм | 55 | 4 | саморезы |
| ALWT-800х600-RAL9016 | 0.289 м² | 800 мм | 795 мм | 600 мм | 596 мм | 145 мм | 509 мм | 60 | 4 | саморезы |
| ALWT-800х625-RAL9016 | 0.301 м² | 800 мм | 795 мм | 625 мм | 621 мм | 145 мм | 509 мм | 63 | 4 | саморезы |
| ALWT-800х650-RAL9016 | 0.313 м² | 800 мм | 795 мм | 650 мм | 646 мм | 145 мм | 509 мм | 65 | 4 | саморезы |
| ALWT-825х100-RAL9016 | 0.050 м² | 825 мм | 820 мм | 100 мм | 96 мм | 150 мм | 525 мм | 10 | 4 | саморезы |
| ALWT-825х125-RAL9016 | 0.062 м² | 825 мм | 820 мм | 125 мм | 121 мм | 150 мм | 525 мм | 13 | 4 | саморезы |
| ALWT-825х150-RAL9016 | 0.074 м² | 825 мм | 820 мм | 150 мм | 146 мм | 150 мм | 525 мм | 15 | 4 | саморезы |
| ALWT-825х200-RAL9016 | 0.099 м² | 825 мм | 820 мм | 200 мм | 196 мм | 150 мм | 525 мм | 20 | 4 | саморезы |
| ALWT-825х225-RAL9016 | 0.112 м² | 825 мм | 820 мм | 225 мм | 221 мм | 150 мм | 525 мм | 23 | 4 | саморезы |
| ALWT-825х250-RAL9016 | 0.124 м² | 825 мм | 820 мм | 250 мм | 246 мм | 150 мм | 525 мм | 25 | 4 | саморезы |
| ALWT-825х300-RAL9016 | 0.149 м² | 825 мм | 820 мм | 300 мм | 296 мм | 150 мм | 525 мм | 30 | 4 | саморезы |
| ALWT-825х325-RAL9016 | 0.161 м² | 825 мм | 820 мм | 325 мм | 321 мм | 150 мм | 525 мм | 33 | 4 | саморезы |
| ALWT-825х350-RAL9016 | 0.174 м² | 825 мм | 820 мм | 350 мм | 346 мм | 150 мм | 525 мм | 35 | 4 | саморезы |
| ALWT-825х400-RAL9016 | 0.199 м² | 825 мм | 820 мм | 400 мм | 396 мм | 150 мм | 525 мм | 40 | 4 | саморезы |
| ALWT-825х425-RAL9016 | 0.211 м² | 825 мм | 820 мм | 425 мм | 421 мм | 150 мм | 525 мм | 43 | 4 | саморезы |
| ALWT-825х450-RAL9016 | 0.223 м² | 825 мм | 820 мм | 450 мм | 446 мм | 150 мм | 525 мм | 45 | 4 | саморезы |
| ALWT-825х500-RAL9016 | 0.248 м² | 825 мм | 820 мм | 500 мм | 496 мм | 150 мм | 525 мм | 50 | 4 | саморезы |
| ALWT-825х525-RAL9016 | 0.261 м² | 825 мм | 820 мм | 525 мм | 521 мм | 150 мм | 525 мм | 53 | 4 | саморезы |
| ALWT-825х550-RAL9016 | 0.273 м² | 825 мм | 820 мм | 550 мм | 546 мм | 150 мм | 525 мм | 55 | 4 | саморезы |
| ALWT-825х600-RAL9016 | 0.298 м² | 825 мм | 820 мм | 600 мм | 596 мм | 150 мм | 525 мм | 60 | 4 | саморезы |
| ALWT-825х625-RAL9016 | 0.310 м² | 825 мм | 820 мм | 625 мм | 621 мм | 150 мм | 525 мм | 63 | 4 | саморезы |
| ALWT-825х650-RAL9016 | 0.323 м² | 825 мм | 820 мм | 650 мм | 646 мм | 150 мм | 525 мм | 65 | 4 | саморезы |
| ALWT-850х100-RAL9016 | 0.051 м² | 850 мм | 845 мм | 100 мм | 96 мм | 155 мм | 541 мм | 10 | 4 | саморезы |
| ALWT-850х125-RAL9016 | 0.064 м² | 850 мм | 845 мм | 125 мм | 121 мм | 155 мм | 541 мм | 13 | 4 | саморезы |
| ALWT-850х150-RAL9016 | 0.077 м² | 850 мм | 845 мм | 150 мм | 146 мм | 155 мм | 541 мм | 15 | 4 | саморезы |
| ALWT-850х200-RAL9016 | 0.102 м² | 850 мм | 845 мм | 200 мм | 196 мм | 155 мм | 541 мм | 20 | 4 | саморезы |
| ALWT-850х225-RAL9016 | 0.115 м² | 850 мм | 845 мм | 225 мм | 221 мм | 155 мм | 541 мм | 23 | 4 | саморезы |
| ALWT-850х250-RAL9016 | 0.128 м² | 850 мм | 845 мм | 250 мм | 246 мм | 155 мм | 541 мм | 25 | 4 | саморезы |
| ALWT-850х300-RAL9016 | 0.153 м² | 850 мм | 845 мм | 300 мм | 296 мм | 155 мм | 541 мм | 30 | 4 | саморезы |
| ALWT-850х325-RAL9016 | 0.166 м² | 850 мм | 845 мм | 325 мм | 321 мм | 155 мм | 541 мм | 33 | 4 | саморезы |
| ALWT-850х350-RAL9016 | 0.179 м² | 850 мм | 845 мм | 350 мм | 346 мм | 155 мм | 541 мм | 35 | 4 | саморезы |
| ALWT-850х400-RAL9016 | 0.205 м² | 850 мм | 845 мм | 400 мм | 396 мм | 155 мм | 541 мм | 40 | 4 | саморезы |
| ALWT-850х425-RAL9016 | 0.217 м² | 850 мм | 845 мм | 425 мм | 421 мм | 155 мм | 541 мм | 43 | 4 | саморезы |
| ALWT-850х450-RAL9016 | 0.230 м² | 850 мм | 845 мм | 450 мм | 446 мм | 155 мм | 541 мм | 45 | 4 | саморезы |
| ALWT-850х500-RAL9016 | 0.256 м² | 850 мм | 845 мм | 500 мм | 496 мм | 155 мм | 541 мм | 50 | 4 | саморезы |
| ALWT-850х525-RAL9016 | 0.268 м² | 850 мм | 845 мм | 525 мм | 521 мм | 155 мм | 541 мм | 53 | 4 | саморезы |
| ALWT-850х550-RAL9016 | 0.281 м² | 850 мм | 845 мм | 550 мм | 546 мм | 155 мм | 541 мм | 55 | 4 | саморезы |
| ALWT-850х600-RAL9016 | 0.307 м² | 850 мм | 845 мм | 600 мм | 596 мм | 155 мм | 541 мм | 60 | 4 | саморезы |
| ALWT-850х625-RAL9016 | 0.320 м² | 850 мм | 845 мм | 625 мм | 621 мм | 155 мм | 541 мм | 63 | 4 | саморезы |
| ALWT-850х650-RAL9016 | 0.332 м² | 850 мм | 845 мм | 650 мм | 646 мм | 155 мм | 541 мм | 65 | 4 | саморезы |
| ALWT-900х100-RAL9016 | 0.054 м² | 900 мм | 895 мм | 100 мм | 96 мм | 164 мм | 573 мм | 10 | 4 | саморезы |
| ALWT-900х125-RAL9016 | 0.068 м² | 900 мм | 895 мм | 125 мм | 121 мм | 164 мм | 573 мм | 13 | 4 | саморезы |
| ALWT-900х150-RAL9016 | 0.081 м² | 900 мм | 895 мм | 150 мм | 146 мм | 164 мм | 573 мм | 15 | 4 | саморезы |
| ALWT-900х200-RAL9016 | 0.108 м² | 900 мм | 895 мм | 200 мм | 196 мм | 164 мм | 573 мм | 20 | 4 | саморезы |
| ALWT-900х225-RAL9016 | 0.122 м² | 900 мм | 895 мм | 225 мм | 221 мм | 164 мм | 573 мм | 23 | 4 | саморезы |
| ALWT-900х250-RAL9016 | 0.135 м² | 900 мм | 895 мм | 250 мм | 246 мм | 164 мм | 573 мм | 25 | 4 | саморезы |
| ALWT-900х300-RAL9016 | 0.162 м² | 900 мм | 895 мм | 300 мм | 296 мм | 164 мм | 573 мм | 30 | 4 | саморезы |
| ALWT-900х325-RAL9016 | 0.176 м² | 900 мм | 895 мм | 325 мм | 321 мм | 164 мм | 573 мм | 33 | 4 | саморезы |
| ALWT-900х350-RAL9016 | 0.190 м² | 900 мм | 895 мм | 350 мм | 346 мм | 164 мм | 573 мм | 35 | 4 | саморезы |
| ALWT-900х400-RAL9016 | 0.217 м² | 900 мм | 895 мм | 400 мм | 396 мм | 164 мм | 573 мм | 40 | 4 | саморезы |
| ALWT-900х425-RAL9016 | 0.230 м² | 900 мм | 895 мм | 425 мм | 421 мм | 164 мм | 573 мм | 43 | 4 | саморезы |
| ALWT-900х450-RAL9016 | 0.244 м² | 900 мм | 895 мм | 450 мм | 446 мм | 164 мм | 573 мм | 45 | 4 | саморезы |
| ALWT-900х500-RAL9016 | 0.271 м² | 900 мм | 895 мм | 500 мм | 496 мм | 164 мм | 573 мм | 50 | 4 | саморезы |
| ALWT-900х525-RAL9016 | 0.284 м² | 900 мм | 895 мм | 525 мм | 521 мм | 164 мм | 573 мм | 53 | 4 | саморезы |
| ALWT-900х550-RAL9016 | 0.298 м² | 900 мм | 895 мм | 550 мм | 546 мм | 164 мм | 573 мм | 55 | 4 | саморезы |
| ALWT-900х600-RAL9016 | 0.325 м² | 900 мм | 895 мм | 600 мм | 596 мм | 164 мм | 573 мм | 60 | 4 | саморезы |
| ALWT-900х625-RAL9016 | 0.338 м² | 900 мм | 895 мм | 625 мм | 621 мм | 164 мм | 573 мм | 63 | 4 | саморезы |
| ALWT-900х650-RAL9016 | 0.352 м² | 900 мм | 895 мм | 650 мм | 646 мм | 164 мм | 573 мм | 65 | 4 | саморезы |
| ALWT-925х100-RAL9016 | 0.056 м² | 925 мм | 920 мм | 100 мм | 96 мм | 168 мм | 589 мм | 10 | 4 | саморезы |
| ALWT-925х125-RAL9016 | 0.070 м² | 925 мм | 920 мм | 125 мм | 121 мм | 168 мм | 589 мм | 13 | 4 | саморезы |
| ALWT-925х150-RAL9016 | 0.083 м² | 925 мм | 920 мм | 150 мм | 146 мм | 168 мм | 589 мм | 15 | 4 | саморезы |
| ALWT-925х200-RAL9016 | 0.111 м² | 925 мм | 920 мм | 200 мм | 196 мм | 168 мм | 589 мм | 20 | 4 | саморезы |
| ALWT-925х225-RAL9016 | 0.125 м² | 925 мм | 920 мм | 225 мм | 221 мм | 168 мм | 589 мм | 23 | 4 | саморезы |
| ALWT-925х250-RAL9016 | 0.139 м² | 925 мм | 920 мм | 250 мм | 246 мм | 168 мм | 589 мм | 25 | 4 | саморезы |
| ALWT-925х300-RAL9016 | 0.167 м² | 925 мм | 920 мм | 300 мм | 296 мм | 168 мм | 589 мм | 30 | 4 | саморезы |
| ALWT-925х325-RAL9016 | 0.181 м² | 925 мм | 920 мм | 325 мм | 321 мм | 168 мм | 589 мм | 33 | 4 | саморезы |
| ALWT-925х350-RAL9016 | 0.195 м² | 925 мм | 920 мм | 350 мм | 346 мм | 168 мм | 589 мм | 35 | 4 | саморезы |
| ALWT-925х400-RAL9016 | 0.223 м² | 925 мм | 920 мм | 400 мм | 396 мм | 168 мм | 589 мм | 40 | 4 | саморезы |
| ALWT-925х425-RAL9016 | 0.237 м² | 925 мм | 920 мм | 425 мм | 421 мм | 168 мм | 589 мм | 43 | 4 | саморезы |
| ALWT-925х450-RAL9016 | 0.250 м² | 925 мм | 920 мм | 450 мм | 446 мм | 168 мм | 589 мм | 45 | 4 | саморезы |
| ALWT-925х500-RAL9016 | 0.278 м² | 925 мм | 920 мм | 500 мм | 496 мм | 168 мм | 589 мм | 50 | 4 | саморезы |
| ALWT-925х525-RAL9016 | 0.292 м² | 925 мм | 920 мм | 525 мм | 521 мм | 168 мм | 589 мм | 53 | 4 | саморезы |
| ALWT-925х550-RAL9016 | 0.306 м² | 925 мм | 920 мм | 550 мм | 546 мм | 168 мм | 589 мм | 55 | 4 | саморезы |
| ALWT-925х600-RAL9016 | 0.334 м² | 925 мм | 920 мм | 600 мм | 596 мм | 168 мм | 589 мм | 60 | 4 | саморезы |
| ALWT-925х625-RAL9016 | 0.348 м² | 925 мм | 920 мм | 625 мм | 621 мм | 168 мм | 589 мм | 63 | 4 | саморезы |
| ALWT-925х650-RAL9016 | 0.362 м² | 925 мм | 920 мм | 650 мм | 646 мм | 168 мм | 589 мм | 65 | 4 | саморезы |
| ALWT-950х100-RAL9016 | 0.057 м² | 950 мм | 945 мм | 100 мм | 96 мм | 173 мм | 605 мм | 10 | 4 | саморезы |
| ALWT-950х125-RAL9016 | 0.071 м² | 950 мм | 945 мм | 125 мм | 121 мм | 173 мм | 605 мм | 13 | 4 | саморезы |
| ALWT-950х150-RAL9016 | 0.086 м² | 950 мм | 945 мм | 150 мм | 146 мм | 173 мм | 605 мм | 15 | 4 | саморезы |
| ALWT-950х200-RAL9016 | 0.114 м² | 950 мм | 945 мм | 200 мм | 196 мм | 173 мм | 605 мм | 20 | 4 | саморезы |
| ALWT-950х225-RAL9016 | 0.129 м² | 950 мм | 945 мм | 225 мм | 221 мм | 173 мм | 605 мм | 23 | 4 | саморезы |
| ALWT-950х250-RAL9016 | 0.143 м² | 950 мм | 945 мм | 250 мм | 246 мм | 173 мм | 605 мм | 25 | 4 | саморезы |
| ALWT-950х300-RAL9016 | 0.171 м² | 950 мм | 945 мм | 300 мм | 296 мм | 173 мм | 605 мм | 30 | 4 | саморезы |
| ALWT-950х325-RAL9016 | 0.186 м² | 950 мм | 945 мм | 325 мм | 321 мм | 173 мм | 605 мм | 33 | 4 | саморезы |
| ALWT-950х350-RAL9016 | 0.200 м² | 950 мм | 945 мм | 350 мм | 346 мм | 173 мм | 605 мм | 35 | 4 | саморезы |
| ALWT-950х400-RAL9016 | 0.229 м² | 950 мм | 945 мм | 400 мм | 396 мм | 173 мм | 605 мм | 40 | 4 | саморезы |
| ALWT-950х425-RAL9016 | 0.243 м² | 950 мм | 945 мм | 425 мм | 421 мм | 173 мм | 605 мм | 43 | 4 | саморезы |
| ALWT-950х450-RAL9016 | 0.257 м² | 950 мм | 945 мм | 450 мм | 446 мм | 173 мм | 605 мм | 45 | 4 | саморезы |
| ALWT-950х500-RAL9016 | 0.286 м² | 950 мм | 945 мм | 500 мм | 496 мм | 173 мм | 605 мм | 50 | 4 | саморезы |
| ALWT-950х525-RAL9016 | 0.300 м² | 950 мм | 945 мм | 525 мм | 521 мм | 173 мм | 605 мм | 53 | 4 | саморезы |
| ALWT-950х550-RAL9016 | 0.314 м² | 950 мм | 945 мм | 550 мм | 546 мм | 173 мм | 605 мм | 55 | 4 | саморезы |
| ALWT-950х600-RAL9016 | 0.343 м² | 950 мм | 945 мм | 600 мм | 596 мм | 173 мм | 605 мм | 60 | 4 | саморезы |
| ALWT-950х625-RAL9016 | 0.357 м² | 950 мм | 945 мм | 625 мм | 621 мм | 173 мм | 605 мм | 63 | 4 | саморезы |
| ALWT-950х650-RAL9016 | 0.371 м² | 950 мм | 945 мм | 650 мм | 646 мм | 173 мм | 605 мм | 65 | 4 | саморезы |
| ALWT-1000х100-RAL9016 | 0.060 м² | 1000 мм | 995 мм | 100 мм | 96 мм | 182 мм | 636 мм | 10 | 4 | саморезы |
| ALWT-1000х125-RAL9016 | 0.075 м² | 1000 мм | 995 мм | 125 мм | 121 мм | 182 мм | 636 мм | 13 | 4 | саморезы |
| ALWT-1000х150-RAL9016 | 0.090 м² | 1000 мм | 995 мм | 150 мм | 146 мм | 182 мм | 636 мм | 15 | 4 | саморезы |
| ALWT-1000х200-RAL9016 | 0.120 м² | 1000 мм | 995 мм | 200 мм | 196 мм | 182 мм | 636 мм | 20 | 4 | саморезы |
| ALWT-1000х225-RAL9016 | 0.135 м² | 1000 мм | 995 мм | 225 мм | 221 мм | 182 мм | 636 мм | 23 | 4 | саморезы |
| ALWT-1000х250-RAL9016 | 0.150 м² | 1000 мм | 995 мм | 250 мм | 246 мм | 182 мм | 636 мм | 25 | 4 | саморезы |
| ALWT-1000х300-RAL9016 | 0.180 м² | 1000 мм | 995 мм | 300 мм | 296 мм | 182 мм | 636 мм | 30 | 4 | саморезы |
| ALWT-1000х325-RAL9016 | 0.196 м² | 1000 мм | 995 мм | 325 мм | 321 мм | 182 мм | 636 мм | 33 | 4 | саморезы |
| ALWT-1000х350-RAL9016 | 0.211 м² | 1000 мм | 995 мм | 350 мм | 346 мм | 182 мм | 636 мм | 35 | 4 | саморезы |
| ALWT-1000х400-RAL9016 | 0.241 м² | 1000 мм | 995 мм | 400 мм | 396 мм | 182 мм | 636 мм | 40 | 4 | саморезы |
| ALWT-1000х425-RAL9016 | 0.256 м² | 1000 мм | 995 мм | 425 мм | 421 мм | 182 мм | 636 мм | 43 | 4 | саморезы |
| ALWT-1000х450-RAL9016 | 0.271 м² | 1000 мм | 995 мм | 450 мм | 446 мм | 182 мм | 636 мм | 45 | 4 | саморезы |
| ALWT-1000х500-RAL9016 | 0.301 м² | 1000 мм | 995 мм | 500 мм | 496 мм | 182 мм | 636 мм | 50 | 4 | саморезы |
| ALWT-1000х525-RAL9016 | 0.316 м² | 1000 мм | 995 мм | 525 мм | 521 мм | 182 мм | 636 мм | 53 | 4 | саморезы |
| ALWT-1000х550-RAL9016 | 0.331 м² | 1000 мм | 995 мм | 550 мм | 546 мм | 182 мм | 636 мм | 55 | 4 | саморезы |
| ALWT-1000х600-RAL9016 | 0.361 м² | 1000 мм | 995 мм | 600 мм | 596 мм | 182 мм | 636 мм | 60 | 4 | саморезы |
| ALWT-1000х625-RAL9016 | 0.376 м² | 1000 мм | 995 мм | 625 мм | 621 мм | 182 мм | 636 мм | 63 | 4 | саморезы |
| ALWT-1000х650-RAL9016 | 0.391 м² | 1000 мм | 995 мм | 650 мм | 646 мм | 182 мм | 636 мм | 65 | 4 | саморезы |
| ALWT-1025х100-RAL9016 | 0.062 м² | 1025 мм | 1020 мм | 100 мм | 96 мм | 186 мм | 652 мм | 10 | 4 | саморезы |
| ALWT-1025х125-RAL9016 | 0.077 м² | 1025 мм | 1020 мм | 125 мм | 121 мм | 186 мм | 652 мм | 13 | 4 | саморезы |
| ALWT-1025х150-RAL9016 | 0.092 м² | 1025 мм | 1020 мм | 150 мм | 146 мм | 186 мм | 652 мм | 15 | 4 | саморезы |
| ALWT-1025х200-RAL9016 | 0.123 м² | 1025 мм | 1020 мм | 200 мм | 196 мм | 186 мм | 652 мм | 20 | 4 | саморезы |
| ALWT-1025х225-RAL9016 | 0.139 м² | 1025 мм | 1020 мм | 225 мм | 221 мм | 186 мм | 652 мм | 23 | 4 | саморезы |
| ALWT-1025х250-RAL9016 | 0.154 м² | 1025 мм | 1020 мм | 250 мм | 246 мм | 186 мм | 652 мм | 25 | 4 | саморезы |
| ALWT-1025х300-RAL9016 | 0.185 м² | 1025 мм | 1020 мм | 300 мм | 296 мм | 186 мм | 652 мм | 30 | 4 | саморезы |
| ALWT-1025х325-RAL9016 | 0.200 м² | 1025 мм | 1020 мм | 325 мм | 321 мм | 186 мм | 652 мм | 33 | 4 | саморезы |
| ALWT-1025х350-RAL9016 | 0.216 м² | 1025 мм | 1020 мм | 350 мм | 346 мм | 186 мм | 652 мм | 35 | 4 | саморезы |
| ALWT-1025х400-RAL9016 | 0.247 м² | 1025 мм | 1020 мм | 400 мм | 396 мм | 186 мм | 652 мм | 40 | 4 | саморезы |
| ALWT-1025х425-RAL9016 | 0.262 м² | 1025 мм | 1020 мм | 425 мм | 421 мм | 186 мм | 652 мм | 43 | 4 | саморезы |
| ALWT-1025х450-RAL9016 | 0.277 м² | 1025 мм | 1020 мм | 450 мм | 446 мм | 186 мм | 652 мм | 45 | 4 | саморезы |
| ALWT-1025х500-RAL9016 | 0.308 м² | 1025 мм | 1020 мм | 500 мм | 496 мм | 186 мм | 652 мм | 50 | 4 | саморезы |
| ALWT-1025х525-RAL9016 | 0.324 м² | 1025 мм | 1020 мм | 525 мм | 521 мм | 186 мм | 652 мм | 53 | 4 | саморезы |
| ALWT-1025х550-RAL9016 | 0.339 м² | 1025 мм | 1020 мм | 550 мм | 546 мм | 186 мм | 652 мм | 55 | 4 | саморезы |
| ALWT-1025х600-RAL9016 | 0.370 м² | 1025 мм | 1020 мм | 600 мм | 596 мм | 186 мм | 652 мм | 60 | 4 | саморезы |
| ALWT-1025х625-RAL9016 | 0.385 м² | 1025 мм | 1020 мм | 625 мм | 621 мм | 186 мм | 652 мм | 63 | 4 | саморезы |
| ALWT-1025х650-RAL9016 | 0.401 м² | 1025 мм | 1020 мм | 650 мм | 646 мм | 186 мм | 652 мм | 65 | 4 | саморезы |
| ALWT-1050х100-RAL9016 | 0.063 м² | 1050 мм | 1045 мм | 100 мм | 96 мм | 191 мм | 668 мм | 10 | 4 | саморезы |
| ALWT-1050х125-RAL9016 | 0.079 м² | 1050 мм | 1045 мм | 125 мм | 121 мм | 191 мм | 668 мм | 13 | 4 | саморезы |
| ALWT-1050х150-RAL9016 | 0.095 м² | 1050 мм | 1045 мм | 150 мм | 146 мм | 191 мм | 668 мм | 15 | 4 | саморезы |
| ALWT-1050х200-RAL9016 | 0.126 м² | 1050 мм | 1045 мм | 200 мм | 196 мм | 191 мм | 668 мм | 20 | 4 | саморезы |
| ALWT-1050х225-RAL9016 | 0.142 м² | 1050 мм | 1045 мм | 225 мм | 221 мм | 191 мм | 668 мм | 23 | 4 | саморезы |
| ALWT-1050х250-RAL9016 | 0.158 м² | 1050 мм | 1045 мм | 250 мм | 246 мм | 191 мм | 668 мм | 25 | 4 | саморезы |
| ALWT-1050х300-RAL9016 | 0.190 м² | 1050 мм | 1045 мм | 300 мм | 296 мм | 191 мм | 668 мм | 30 | 4 | саморезы |
| ALWT-1050х325-RAL9016 | 0.205 м² | 1050 мм | 1045 мм | 325 мм | 321 мм | 191 мм | 668 мм | 33 | 4 | саморезы |
| ALWT-1050х350-RAL9016 | 0.221 м² | 1050 мм | 1045 мм | 350 мм | 346 мм | 191 мм | 668 мм | 35 | 4 | саморезы |
| ALWT-1050х400-RAL9016 | 0.253 м² | 1050 мм | 1045 мм | 400 мм | 396 мм | 191 мм | 668 мм | 40 | 4 | саморезы |
| ALWT-1050х425-RAL9016 | 0.268 м² | 1050 мм | 1045 мм | 425 мм | 421 мм | 191 мм | 668 мм | 43 | 4 | саморезы |
| ALWT-1050х450-RAL9016 | 0.284 м² | 1050 мм | 1045 мм | 450 мм | 446 мм | 191 мм | 668 мм | 45 | 4 | саморезы |
| ALWT-1050х500-RAL9016 | 0.316 м² | 1050 мм | 1045 мм | 500 мм | 496 мм | 191 мм | 668 мм | 50 | 4 | саморезы |
| ALWT-1050х525-RAL9016 | 0.332 м² | 1050 мм | 1045 мм | 525 мм | 521 мм | 191 мм | 668 мм | 53 | 4 | саморезы |
| ALWT-1050х550-RAL9016 | 0.347 м² | 1050 мм | 1045 мм | 550 мм | 546 мм | 191 мм | 668 мм | 55 | 4 | саморезы |
| ALWT-1050х600-RAL9016 | 0.379 м² | 1050 мм | 1045 мм | 600 мм | 596 мм | 191 мм | 668 мм | 60 | 4 | саморезы |
| ALWT-1050х625-RAL9016 | 0.395 м² | 1050 мм | 1045 мм | 625 мм | 621 мм | 191 мм | 668 мм | 63 | 4 | саморезы |
| ALWT-1050х650-RAL9016 | 0.411 м² | 1050 мм | 1045 мм | 650 мм | 646 мм | 191 мм | 668 мм | 65 | 4 | саморезы |
| ALWT-1100х100-RAL9016 | 0.066 м² | 1100 мм | 1095 мм | 100 мм | 96 мм | 200 мм | 700 мм | 10 | 4 | саморезы |
| ALWT-1100х125-RAL9016 | 0.083 м² | 1100 мм | 1095 мм | 125 мм | 121 мм | 200 мм | 700 мм | 13 | 4 | саморезы |
| ALWT-1100х150-RAL9016 | 0.099 м² | 1100 мм | 1095 мм | 150 мм | 146 мм | 200 мм | 700 мм | 15 | 4 | саморезы |
| ALWT-1100х200-RAL9016 | 0.132 м² | 1100 мм | 1095 мм | 200 мм | 196 мм | 200 мм | 700 мм | 20 | 4 | саморезы |
| ALWT-1100х225-RAL9016 | 0.149 м² | 1100 мм | 1095 мм | 225 мм | 221 мм | 200 мм | 700 мм | 23 | 4 | саморезы |
| ALWT-1100х250-RAL9016 | 0.165 м² | 1100 мм | 1095 мм | 250 мм | 246 мм | 200 мм | 700 мм | 25 | 4 | саморезы |
| ALWT-1100х300-RAL9016 | 0.199 м² | 1100 мм | 1095 мм | 300 мм | 296 мм | 200 мм | 700 мм | 30 | 4 | саморезы |
| ALWT-1100х325-RAL9016 | 0.215 м² | 1100 мм | 1095 мм | 325 мм | 321 мм | 200 мм | 700 мм | 33 | 4 | саморезы |
| ALWT-1100х350-RAL9016 | 0.232 м² | 1100 мм | 1095 мм | 350 мм | 346 мм | 200 мм | 700 мм | 35 | 4 | саморезы |
| ALWT-1100х400-RAL9016 | 0.265 м² | 1100 мм | 1095 мм | 400 мм | 396 мм | 200 мм | 700 мм | 40 | 4 | саморезы |
| ALWT-1100х425-RAL9016 | 0.281 м² | 1100 мм | 1095 мм | 425 мм | 421 мм | 200 мм | 700 мм | 43 | 4 | саморезы |
| ALWT-1100х450-RAL9016 | 0.298 м² | 1100 мм | 1095 мм | 450 мм | 446 мм | 200 мм | 700 мм | 45 | 4 | саморезы |
| ALWT-1100х500-RAL9016 | 0.331 м² | 1100 мм | 1095 мм | 500 мм | 496 мм | 200 мм | 700 мм | 50 | 4 | саморезы |
| ALWT-1100х525-RAL9016 | 0.347 м² | 1100 мм | 1095 мм | 525 мм | 521 мм | 200 мм | 700 мм | 53 | 4 | саморезы |
| ALWT-1100х550-RAL9016 | 0.364 м² | 1100 мм | 1095 мм | 550 мм | 546 мм | 200 мм | 700 мм | 55 | 4 | саморезы |
| ALWT-1100х600-RAL9016 | 0.397 м² | 1100 мм | 1095 мм | 600 мм | 596 мм | 200 мм | 700 мм | 60 | 4 | саморезы |
| ALWT-1100х625-RAL9016 | 0.414 м² | 1100 мм | 1095 мм | 625 мм | 621 мм | 200 мм | 700 мм | 63 | 4 | саморезы |
| ALWT-1100х650-RAL9016 | 0.430 м² | 1100 мм | 1095 мм | 650 мм | 646 мм | 200 мм | 700 мм | 65 | 4 | саморезы |
| ALWT-1125х100-RAL9016 | 0.068 м² | 1125 мм | 1120 мм | 100 мм | 96 мм | 205 мм | 716 мм | 10 | 4 | саморезы |
| ALWT-1125х125-RAL9016 | 0.085 м² | 1125 мм | 1120 мм | 125 мм | 121 мм | 205 мм | 716 мм | 13 | 4 | саморезы |
| ALWT-1125х150-RAL9016 | 0.102 м² | 1125 мм | 1120 мм | 150 мм | 146 мм | 205 мм | 716 мм | 15 | 4 | саморезы |
| ALWT-1125х200-RAL9016 | 0.135 м² | 1125 мм | 1120 мм | 200 мм | 196 мм | 205 мм | 716 мм | 20 | 4 | саморезы |
| ALWT-1125х225-RAL9016 | 0.152 м² | 1125 мм | 1120 мм | 225 мм | 221 мм | 205 мм | 716 мм | 23 | 4 | саморезы |
| ALWT-1125х250-RAL9016 | 0.169 м² | 1125 мм | 1120 мм | 250 мм | 246 мм | 205 мм | 716 мм | 25 | 4 | саморезы |
| ALWT-1125х300-RAL9016 | 0.203 м² | 1125 мм | 1120 мм | 300 мм | 296 мм | 205 мм | 716 мм | 30 | 4 | саморезы |
| ALWT-1125х325-RAL9016 | 0.220 м² | 1125 мм | 1120 мм | 325 мм | 321 мм | 205 мм | 716 мм | 33 | 4 | саморезы |
| ALWT-1125х350-RAL9016 | 0.237 м² | 1125 мм | 1120 мм | 350 мм | 346 мм | 205 мм | 716 мм | 35 | 4 | саморезы |
| ALWT-1125х400-RAL9016 | 0.271 м² | 1125 мм | 1120 мм | 400 мм | 396 мм | 205 мм | 716 мм | 40 | 4 | саморезы |
| ALWT-1125х425-RAL9016 | 0.288 м² | 1125 мм | 1120 мм | 425 мм | 421 мм | 205 мм | 716 мм | 43 | 4 | саморезы |
| ALWT-1125х450-RAL9016 | 0.305 м² | 1125 мм | 1120 мм | 450 мм | 446 мм | 205 мм | 716 мм | 45 | 4 | саморезы |
| ALWT-1125х500-RAL9016 | 0.338 м² | 1125 мм | 1120 мм | 500 мм | 496 мм | 205 мм | 716 мм | 50 | 4 | саморезы |
| ALWT-1125х525-RAL9016 | 0.355 м² | 1125 мм | 1120 мм | 525 мм | 521 мм | 205 мм | 716 мм | 53 | 4 | саморезы |
| ALWT-1125х550-RAL9016 | 0.372 м² | 1125 мм | 1120 мм | 550 мм | 546 мм | 205 мм | 716 мм | 55 | 4 | саморезы |
| ALWT-1125х600-RAL9016 | 0.406 м² | 1125 мм | 1120 мм | 600 мм | 596 мм | 205 мм | 716 мм | 60 | 4 | саморезы |
| ALWT-1125х625-RAL9016 | 0.423 м² | 1125 мм | 1120 мм | 625 мм | 621 мм | 205 мм | 716 мм | 63 | 4 | саморезы |
| ALWT-1125х650-RAL9016 | 0.440 м² | 1125 мм | 1120 мм | 650 мм | 646 мм | 205 мм | 716 мм | 65 | 4 | саморезы |
| ALWT-1150х100-RAL9016 | 0.069 м² | 1150 мм | 1145 мм | 100 мм | 96 мм | 209 мм | 732 мм | 10 | 4 | саморезы |
| ALWT-1150х125-RAL9016 | 0.086 м² | 1150 мм | 1145 мм | 125 мм | 121 мм | 209 мм | 732 мм | 13 | 4 | саморезы |
| ALWT-1150х150-RAL9016 | 0.104 м² | 1150 мм | 1145 мм | 150 мм | 146 мм | 209 мм | 732 мм | 15 | 4 | саморезы |
| ALWT-1150х200-RAL9016 | 0.138 м² | 1150 мм | 1145 мм | 200 мм | 196 мм | 209 мм | 732 мм | 20 | 4 | саморезы |
| ALWT-1150х225-RAL9016 | 0.156 м² | 1150 мм | 1145 мм | 225 мм | 221 мм | 209 мм | 732 мм | 23 | 4 | саморезы |
| ALWT-1150х250-RAL9016 | 0.173 м² | 1150 мм | 1145 мм | 250 мм | 246 мм | 209 мм | 732 мм | 25 | 4 | саморезы |
| ALWT-1150х300-RAL9016 | 0.208 м² | 1150 мм | 1145 мм | 300 мм | 296 мм | 209 мм | 732 мм | 30 | 4 | саморезы |
| ALWT-1150х325-RAL9016 | 0.225 м² | 1150 мм | 1145 мм | 325 мм | 321 мм | 209 мм | 732 мм | 33 | 4 | саморезы |
| ALWT-1150х350-RAL9016 | 0.242 м² | 1150 мм | 1145 мм | 350 мм | 346 мм | 209 мм | 732 мм | 35 | 4 | саморезы |
| ALWT-1150х400-RAL9016 | 0.277 м² | 1150 мм | 1145 мм | 400 мм | 396 мм | 209 мм | 732 мм | 40 | 4 | саморезы |
| ALWT-1150х425-RAL9016 | 0.294 м² | 1150 мм | 1145 мм | 425 мм | 421 мм | 209 мм | 732 мм | 43 | 4 | саморезы |
| ALWT-1150х450-RAL9016 | 0.311 м² | 1150 мм | 1145 мм | 450 мм | 446 мм | 209 мм | 732 мм | 45 | 4 | саморезы |
| ALWT-1150х500-RAL9016 | 0.346 м² | 1150 мм | 1145 мм | 500 мм | 496 мм | 209 мм | 732 мм | 50 | 4 | саморезы |
| ALWT-1150х525-RAL9016 | 0.363 м² | 1150 мм | 1145 мм | 525 мм | 521 мм | 209 мм | 732 мм | 53 | 4 | саморезы |
| ALWT-1150х550-RAL9016 | 0.381 м² | 1150 мм | 1145 мм | 550 мм | 546 мм | 209 мм | 732 мм | 55 | 4 | саморезы |
| ALWT-1150х600-RAL9016 | 0.415 м² | 1150 мм | 1145 мм | 600 мм | 596 мм | 209 мм | 732 мм | 60 | 4 | саморезы |
| ALWT-1150х625-RAL9016 | 0.432 м² | 1150 мм | 1145 мм | 625 мм | 621 мм | 209 мм | 732 мм | 63 | 4 | саморезы |
| ALWT-1150х650-RAL9016 | 0.450 м² | 1150 мм | 1145 мм | 650 мм | 646 мм | 209 мм | 732 мм | 65 | 4 | саморезы |
| ALWT-1200х100-RAL9016 | 0.072 м² | 1200 мм | 1195 мм | 100 мм | 96 мм | 218 мм | 764 мм | 10 | 4 | саморезы |
| ALWT-1200х125-RAL9016 | 0.090 м² | 1200 мм | 1195 мм | 125 мм | 121 мм | 218 мм | 764 мм | 13 | 4 | саморезы |
| ALWT-1200х150-RAL9016 | 0.108 м² | 1200 мм | 1195 мм | 150 мм | 146 мм | 218 мм | 764 мм | 15 | 4 | саморезы |
| ALWT-1200х200-RAL9016 | 0.144 м² | 1200 мм | 1195 мм | 200 мм | 196 мм | 218 мм | 764 мм | 20 | 4 | саморезы |
| ALWT-1200х225-RAL9016 | 0.162 м² | 1200 мм | 1195 мм | 225 мм | 221 мм | 218 мм | 764 мм | 23 | 4 | саморезы |
| ALWT-1200х250-RAL9016 | 0.180 м² | 1200 мм | 1195 мм | 250 мм | 246 мм | 218 мм | 764 мм | 25 | 4 | саморезы |
| ALWT-1200х300-RAL9016 | 0.217 м² | 1200 мм | 1195 мм | 300 мм | 296 мм | 218 мм | 764 мм | 30 | 4 | саморезы |
| ALWT-1200х325-RAL9016 | 0.235 м² | 1200 мм | 1195 мм | 325 мм | 321 мм | 218 мм | 764 мм | 33 | 4 | саморезы |
| ALWT-1200х350-RAL9016 | 0.253 м² | 1200 мм | 1195 мм | 350 мм | 346 мм | 218 мм | 764 мм | 35 | 4 | саморезы |
| ALWT-1200х400-RAL9016 | 0.289 м² | 1200 мм | 1195 мм | 400 мм | 396 мм | 218 мм | 764 мм | 40 | 4 | саморезы |
| ALWT-1200х425-RAL9016 | 0.307 м² | 1200 мм | 1195 мм | 425 мм | 421 мм | 218 мм | 764 мм | 43 | 4 | саморезы |
| ALWT-1200х450-RAL9016 | 0.325 м² | 1200 мм | 1195 мм | 450 мм | 446 мм | 218 мм | 764 мм | 45 | 4 | саморезы |
| ALWT-1200х500-RAL9016 | 0.361 м² | 1200 мм | 1195 мм | 500 мм | 496 мм | 218 мм | 764 мм | 50 | 4 | саморезы |
| ALWT-1200х525-RAL9016 | 0.379 м² | 1200 мм | 1195 мм | 525 мм | 521 мм | 218 мм | 764 мм | 53 | 4 | саморезы |
| ALWT-1200х550-RAL9016 | 0.397 м² | 1200 мм | 1195 мм | 550 мм | 546 мм | 218 мм | 764 мм | 55 | 4 | саморезы |
| ALWT-1200х600-RAL9016 | 0.433 м² | 1200 мм | 1195 мм | 600 мм | 596 мм | 218 мм | 764 мм | 60 | 4 | саморезы |
| ALWT-1200х625-RAL9016 | 0.451 м² | 1200 мм | 1195 мм | 625 мм | 621 мм | 218 мм | 764 мм | 63 | 4 | саморезы |
| ALWT-1200х650-RAL9016 | 0.469 м² | 1200 мм | 1195 мм | 650 мм | 646 мм | 218 мм | 764 мм | 65 | 4 | саморезы |
| ALWT-1225х100-RAL9016 | 0.074 м² | 1225 мм | 1220 мм | 100 мм | 96 мм | 223 мм | 780 мм | 10 | 4 | саморезы |
| ALWT-1225х125-RAL9016 | 0.092 м² | 1225 мм | 1220 мм | 125 мм | 121 мм | 223 мм | 780 мм | 13 | 4 | саморезы |
| ALWT-1225х150-RAL9016 | 0.111 м² | 1225 мм | 1220 мм | 150 мм | 146 мм | 223 мм | 780 мм | 15 | 4 | саморезы |
| ALWT-1225х200-RAL9016 | 0.147 м² | 1225 мм | 1220 мм | 200 мм | 196 мм | 223 мм | 780 мм | 20 | 4 | саморезы |
| ALWT-1225х225-RAL9016 | 0.166 м² | 1225 мм | 1220 мм | 225 мм | 221 мм | 223 мм | 780 мм | 23 | 4 | саморезы |
| ALWT-1225х250-RAL9016 | 0.184 м² | 1225 мм | 1220 мм | 250 мм | 246 мм | 223 мм | 780 мм | 25 | 4 | саморезы |
| ALWT-1225х300-RAL9016 | 0.221 м² | 1225 мм | 1220 мм | 300 мм | 296 мм | 223 мм | 780 мм | 30 | 4 | саморезы |
| ALWT-1225х325-RAL9016 | 0.240 м² | 1225 мм | 1220 мм | 325 мм | 321 мм | 223 мм | 780 мм | 33 | 4 | саморезы |
| ALWT-1225х350-RAL9016 | 0.258 м² | 1225 мм | 1220 мм | 350 мм | 346 мм | 223 мм | 780 мм | 35 | 4 | саморезы |
| ALWT-1225х400-RAL9016 | 0.295 м² | 1225 мм | 1220 мм | 400 мм | 396 мм | 223 мм | 780 мм | 40 | 4 | саморезы |
| ALWT-1225х425-RAL9016 | 0.313 м² | 1225 мм | 1220 мм | 425 мм | 421 мм | 223 мм | 780 мм | 43 | 4 | саморезы |
| ALWT-1225х450-RAL9016 | 0.332 м² | 1225 мм | 1220 мм | 450 мм | 446 мм | 223 мм | 780 мм | 45 | 4 | саморезы |
| ALWT-1225х500-RAL9016 | 0.368 м² | 1225 мм | 1220 мм | 500 мм | 496 мм | 223 мм | 780 мм | 50 | 4 | саморезы |
| ALWT-1225х525-RAL9016 | 0.387 м² | 1225 мм | 1220 мм | 525 мм | 521 мм | 223 мм | 780 мм | 53 | 4 | саморезы |
| ALWT-1225х550-RAL9016 | 0.405 м² | 1225 мм | 1220 мм | 550 мм | 546 мм | 223 мм | 780 мм | 55 | 4 | саморезы |
| ALWT-1225х600-RAL9016 | 0.442 м² | 1225 мм | 1220 мм | 600 мм | 596 мм | 223 мм | 780 мм | 60 | 4 | саморезы |
| ALWT-1225х625-RAL9016 | 0.461 м² | 1225 мм | 1220 мм | 625 мм | 621 мм | 223 мм | 780 мм | 63 | 4 | саморезы |
| ALWT-1225х650-RAL9016 | 0.479 м² | 1225 мм | 1220 мм | 650 мм | 646 мм | 223 мм | 780 мм | 65 | 4 | саморезы |
| ALWT-1250х100-RAL9016 | 0.075 м² | 1250 мм | 1245 мм | 100 мм | 96 мм | 227 мм | 795 мм | 10 | 4 | саморезы |
| ALWT-1250х125-RAL9016 | 0.094 м² | 1250 мм | 1245 мм | 125 мм | 121 мм | 227 мм | 795 мм | 13 | 4 | саморезы |
| ALWT-1250х150-RAL9016 | 0.113 м² | 1250 мм | 1245 мм | 150 мм | 146 мм | 227 мм | 795 мм | 15 | 4 | саморезы |
| ALWT-1250х200-RAL9016 | 0.150 м² | 1250 мм | 1245 мм | 200 мм | 196 мм | 227 мм | 795 мм | 20 | 4 | саморезы |
| ALWT-1250х225-RAL9016 | 0.169 м² | 1250 мм | 1245 мм | 225 мм | 221 мм | 227 мм | 795 мм | 23 | 4 | саморезы |
| ALWT-1250х250-RAL9016 | 0.188 м² | 1250 мм | 1245 мм | 250 мм | 246 мм | 227 мм | 795 мм | 25 | 4 | саморезы |
| ALWT-1250х300-RAL9016 | 0.226 м² | 1250 мм | 1245 мм | 300 мм | 296 мм | 227 мм | 795 мм | 30 | 4 | саморезы |
| ALWT-1250х325-RAL9016 | 0.244 м² | 1250 мм | 1245 мм | 325 мм | 321 мм | 227 мм | 795 мм | 33 | 4 | саморезы |
| ALWT-1250х350-RAL9016 | 0.263 м² | 1250 мм | 1245 мм | 350 мм | 346 мм | 227 мм | 795 мм | 35 | 4 | саморезы |
| ALWT-1250х400-RAL9016 | 0.301 м² | 1250 мм | 1245 мм | 400 мм | 396 мм | 227 мм | 795 мм | 40 | 4 | саморезы |
| ALWT-1250х425-RAL9016 | 0.320 м² | 1250 мм | 1245 мм | 425 мм | 421 мм | 227 мм | 795 мм | 43 | 4 | саморезы |
| ALWT-1250х450-RAL9016 | 0.338 м² | 1250 мм | 1245 мм | 450 мм | 446 мм | 227 мм | 795 мм | 45 | 4 | саморезы |
| ALWT-1250х500-RAL9016 | 0.376 м² | 1250 мм | 1245 мм | 500 мм | 496 мм | 227 мм | 795 мм | 50 | 4 | саморезы |
| ALWT-1250х525-RAL9016 | 0.395 м² | 1250 мм | 1245 мм | 525 мм | 521 мм | 227 мм | 795 мм | 53 | 4 | саморезы |
| ALWT-1250х550-RAL9016 | 0.414 м² | 1250 мм | 1245 мм | 550 мм | 546 мм | 227 мм | 795 мм | 55 | 4 | саморезы |
| ALWT-1250х600-RAL9016 | 0.451 м² | 1250 мм | 1245 мм | 600 мм | 596 мм | 227 мм | 795 мм | 60 | 4 | саморезы |
| ALWT-1250х625-RAL9016 | 0.470 м² | 1250 мм | 1245 мм | 625 мм | 621 мм | 227 мм | 795 мм | 63 | 4 | саморезы |
| ALWT-1250х650-RAL9016 | 0.489 м² | 1250 мм | 1245 мм | 650 мм | 646 мм | 227 мм | 795 мм | 65 | 4 | саморезы |
| ALWT-1300х100-RAL9016 | 0.078 м² | 1300 мм | 1295 мм | 100 мм | 96 мм | 236 мм | 827 мм | 10 | 4 | саморезы |
| ALWT-1300х125-RAL9016 | 0.098 м² | 1300 мм | 1295 мм | 125 мм | 121 мм | 236 мм | 827 мм | 13 | 4 | саморезы |
| ALWT-1300х150-RAL9016 | 0.117 м² | 1300 мм | 1295 мм | 150 мм | 146 мм | 236 мм | 827 мм | 15 | 4 | саморезы |
| ALWT-1300х200-RAL9016 | 0.156 м² | 1300 мм | 1295 мм | 200 мм | 196 мм | 236 мм | 827 мм | 20 | 4 | саморезы |
| ALWT-1300х225-RAL9016 | 0.176 м² | 1300 мм | 1295 мм | 225 мм | 221 мм | 236 мм | 827 мм | 23 | 4 | саморезы |
| ALWT-1300х250-RAL9016 | 0.196 м² | 1300 мм | 1295 мм | 250 мм | 246 мм | 236 мм | 827 мм | 25 | 4 | саморезы |
| ALWT-1300х300-RAL9016 | 0.235 м² | 1300 мм | 1295 мм | 300 мм | 296 мм | 236 мм | 827 мм | 30 | 4 | саморезы |
| ALWT-1300х325-RAL9016 | 0.254 м² | 1300 мм | 1295 мм | 325 мм | 321 мм | 236 мм | 827 мм | 33 | 4 | саморезы |
| ALWT-1300х350-RAL9016 | 0.274 м² | 1300 мм | 1295 мм | 350 мм | 346 мм | 236 мм | 827 мм | 35 | 4 | саморезы |
| ALWT-1300х400-RAL9016 | 0.313 м² | 1300 мм | 1295 мм | 400 мм | 396 мм | 236 мм | 827 мм | 40 | 4 | саморезы |
| ALWT-1300х425-RAL9016 | 0.332 м² | 1300 мм | 1295 мм | 425 мм | 421 мм | 236 мм | 827 мм | 43 | 4 | саморезы |
| ALWT-1300х450-RAL9016 | 0.352 м² | 1300 мм | 1295 мм | 450 мм | 446 мм | 236 мм | 827 мм | 45 | 4 | саморезы |
| ALWT-1300х500-RAL9016 | 0.391 м² | 1300 мм | 1295 мм | 500 мм | 496 мм | 236 мм | 827 мм | 50 | 4 | саморезы |
| ALWT-1300х525-RAL9016 | 0.411 м² | 1300 мм | 1295 мм | 525 мм | 521 мм | 236 мм | 827 мм | 53 | 4 | саморезы |
| ALWT-1300х550-RAL9016 | 0.430 м² | 1300 мм | 1295 мм | 550 мм | 546 мм | 236 мм | 827 мм | 55 | 4 | саморезы |
| ALWT-1300х600-RAL9016 | 0.469 м² | 1300 мм | 1295 мм | 600 мм | 596 мм | 236 мм | 827 мм | 60 | 4 | саморезы |
| ALWT-1300х625-RAL9016 | 0.489 м² | 1300 мм | 1295 мм | 625 мм | 621 мм | 236 мм | 827 мм | 63 | 4 | саморезы |
| ALWT-1300х650-RAL9016 | 0.508 м² | 1300 мм | 1295 мм | 650 мм | 646 мм | 236 мм | 827 мм | 65 | 4 | саморезы |
| ALWT-1325х100-RAL9016 | 0.080 м² | 1325 мм | 1320 мм | 100 мм | 96 мм | 241 мм | 843 мм | 10 | 4 | саморезы |
| ALWT-1325х125-RAL9016 | 0.100 м² | 1325 мм | 1320 мм | 125 мм | 121 мм | 241 мм | 843 мм | 13 | 4 | саморезы |
| ALWT-1325х150-RAL9016 | 0.120 м² | 1325 мм | 1320 мм | 150 мм | 146 мм | 241 мм | 843 мм | 15 | 4 | саморезы |
| ALWT-1325х200-RAL9016 | 0.159 м² | 1325 мм | 1320 мм | 200 мм | 196 мм | 241 мм | 843 мм | 20 | 4 | саморезы |
| ALWT-1325х225-RAL9016 | 0.179 м² | 1325 мм | 1320 мм | 225 мм | 221 мм | 241 мм | 843 мм | 23 | 4 | саморезы |
| ALWT-1325х250-RAL9016 | 0.199 м² | 1325 мм | 1320 мм | 250 мм | 246 мм | 241 мм | 843 мм | 25 | 4 | саморезы |
| ALWT-1325х300-RAL9016 | 0.239 м² | 1325 мм | 1320 мм | 300 мм | 296 мм | 241 мм | 843 мм | 30 | 4 | саморезы |
| ALWT-1325х325-RAL9016 | 0.259 м² | 1325 мм | 1320 мм | 325 мм | 321 мм | 241 мм | 843 мм | 33 | 4 | саморезы |
| ALWT-1325х350-RAL9016 | 0.279 м² | 1325 мм | 1320 мм | 350 мм | 346 мм | 241 мм | 843 мм | 35 | 4 | саморезы |
| ALWT-1325х400-RAL9016 | 0.319 м² | 1325 мм | 1320 мм | 400 мм | 396 мм | 241 мм | 843 мм | 40 | 4 | саморезы |
| ALWT-1325х425-RAL9016 | 0.339 м² | 1325 мм | 1320 мм | 425 мм | 421 мм | 241 мм | 843 мм | 43 | 4 | саморезы |
| ALWT-1325х450-RAL9016 | 0.359 м² | 1325 мм | 1320 мм | 450 мм | 446 мм | 241 мм | 843 мм | 45 | 4 | саморезы |
| ALWT-1325х500-RAL9016 | 0.399 м² | 1325 мм | 1320 мм | 500 мм | 496 мм | 241 мм | 843 мм | 50 | 4 | саморезы |
| ALWT-1325х525-RAL9016 | 0.418 м² | 1325 мм | 1320 мм | 525 мм | 521 мм | 241 мм | 843 мм | 53 | 4 | саморезы |
| ALWT-1325х550-RAL9016 | 0.438 м² | 1325 мм | 1320 мм | 550 мм | 546 мм | 241 мм | 843 мм | 55 | 4 | саморезы |
| ALWT-1325х600-RAL9016 | 0.478 м² | 1325 мм | 1320 мм | 600 мм | 596 мм | 241 мм | 843 мм | 60 | 4 | саморезы |
| ALWT-1325х625-RAL9016 | 0.498 м² | 1325 мм | 1320 мм | 625 мм | 621 мм | 241 мм | 843 мм | 63 | 4 | саморезы |
| ALWT-1325х650-RAL9016 | 0.518 м² | 1325 мм | 1320 мм | 650 мм | 646 мм | 241 мм | 843 мм | 65 | 4 | саморезы |
| ALWT-1350х100-RAL9016 | 0.081 м² | 1350 мм | 1345 мм | 100 мм | 96 мм | 245 мм | 859 мм | 10 | 4 | саморезы |
| ALWT-1350х125-RAL9016 | 0.102 м² | 1350 мм | 1345 мм | 125 мм | 121 мм | 245 мм | 859 мм | 13 | 4 | саморезы |
| ALWT-1350х150-RAL9016 | 0.122 м² | 1350 мм | 1345 мм | 150 мм | 146 мм | 245 мм | 859 мм | 15 | 4 | саморезы |
| ALWT-1350х200-RAL9016 | 0.162 м² | 1350 мм | 1345 мм | 200 мм | 196 мм | 245 мм | 859 мм | 20 | 4 | саморезы |
| ALWT-1350х225-RAL9016 | 0.183 м² | 1350 мм | 1345 мм | 225 мм | 221 мм | 245 мм | 859 мм | 23 | 4 | саморезы |
| ALWT-1350х250-RAL9016 | 0.203 м² | 1350 мм | 1345 мм | 250 мм | 246 мм | 245 мм | 859 мм | 25 | 4 | саморезы |
| ALWT-1350х300-RAL9016 | 0.244 м² | 1350 мм | 1345 мм | 300 мм | 296 мм | 245 мм | 859 мм | 30 | 4 | саморезы |
| ALWT-1350х325-RAL9016 | 0.264 м² | 1350 мм | 1345 мм | 325 мм | 321 мм | 245 мм | 859 мм | 33 | 4 | саморезы |
| ALWT-1350х350-RAL9016 | 0.284 м² | 1350 мм | 1345 мм | 350 мм | 346 мм | 245 мм | 859 мм | 35 | 4 | саморезы |
| ALWT-1350х400-RAL9016 | 0.325 м² | 1350 мм | 1345 мм | 400 мм | 396 мм | 245 мм | 859 мм | 40 | 4 | саморезы |
| ALWT-1350х425-RAL9016 | 0.345 м² | 1350 мм | 1345 мм | 425 мм | 421 мм | 245 мм | 859 мм | 43 | 4 | саморезы |
| ALWT-1350х450-RAL9016 | 0.365 м² | 1350 мм | 1345 мм | 450 мм | 446 мм | 245 мм | 859 мм | 45 | 4 | саморезы |
| ALWT-1350х500-RAL9016 | 0.406 м² | 1350 мм | 1345 мм | 500 мм | 496 мм | 245 мм | 859 мм | 50 | 4 | саморезы |
| ALWT-1350х525-RAL9016 | 0.426 м² | 1350 мм | 1345 мм | 525 мм | 521 мм | 245 мм | 859 мм | 53 | 4 | саморезы |
| ALWT-1350х550-RAL9016 | 0.447 м² | 1350 мм | 1345 мм | 550 мм | 546 мм | 245 мм | 859 мм | 55 | 4 | саморезы |
| ALWT-1350х600-RAL9016 | 0.487 м² | 1350 мм | 1345 мм | 600 мм | 596 мм | 245 мм | 859 мм | 60 | 4 | саморезы |
| ALWT-1350х625-RAL9016 | 0.508 м² | 1350 мм | 1345 мм | 625 мм | 621 мм | 245 мм | 859 мм | 63 | 4 | саморезы |
| ALWT-1350х650-RAL9016 | 0.528 м² | 1350 мм | 1345 мм | 650 мм | 646 мм | 245 мм | 859 мм | 65 | 4 | саморезы |
| ALWT-1400х100-RAL9016 | 0.084 м² | 1400 мм | 1395 мм | 100 мм | 96 мм | 255 мм | 891 мм | 10 | 4 | саморезы |
| ALWT-1400х125-RAL9016 | 0.105 м² | 1400 мм | 1395 мм | 125 мм | 121 мм | 255 мм | 891 мм | 13 | 4 | саморезы |
| ALWT-1400х150-RAL9016 | 0.126 м² | 1400 мм | 1395 мм | 150 мм | 146 мм | 255 мм | 891 мм | 15 | 4 | саморезы |
| ALWT-1400х200-RAL9016 | 0.168 м² | 1400 мм | 1395 мм | 200 мм | 196 мм | 255 мм | 891 мм | 20 | 4 | саморезы |
| ALWT-1400х225-RAL9016 | 0.190 м² | 1400 мм | 1395 мм | 225 мм | 221 мм | 255 мм | 891 мм | 23 | 4 | саморезы |
| ALWT-1400х250-RAL9016 | 0.211 м² | 1400 мм | 1395 мм | 250 мм | 246 мм | 255 мм | 891 мм | 25 | 4 | саморезы |
| ALWT-1400х300-RAL9016 | 0.253 м² | 1400 мм | 1395 мм | 300 мм | 296 мм | 255 мм | 891 мм | 30 | 4 | саморезы |
| ALWT-1400х325-RAL9016 | 0.274 м² | 1400 мм | 1395 мм | 325 мм | 321 мм | 255 мм | 891 мм | 33 | 4 | саморезы |
| ALWT-1400х350-RAL9016 | 0.295 м² | 1400 мм | 1395 мм | 350 мм | 346 мм | 255 мм | 891 мм | 35 | 4 | саморезы |
| ALWT-1400х400-RAL9016 | 0.337 м² | 1400 мм | 1395 мм | 400 мм | 396 мм | 255 мм | 891 мм | 40 | 4 | саморезы |
| ALWT-1400х425-RAL9016 | 0.358 м² | 1400 мм | 1395 мм | 425 мм | 421 мм | 255 мм | 891 мм | 43 | 4 | саморезы |
| ALWT-1400х450-RAL9016 | 0.379 м² | 1400 мм | 1395 мм | 450 мм | 446 мм | 255 мм | 891 мм | 45 | 4 | саморезы |
| ALWT-1400х500-RAL9016 | 0.421 м² | 1400 мм | 1395 мм | 500 мм | 496 мм | 255 мм | 891 мм | 50 | 4 | саморезы |
| ALWT-1400х525-RAL9016 | 0.442 м² | 1400 мм | 1395 мм | 525 мм | 521 мм | 255 мм | 891 мм | 53 | 4 | саморезы |
| ALWT-1400х550-RAL9016 | 0.463 м² | 1400 мм | 1395 мм | 550 мм | 546 мм | 255 мм | 891 мм | 55 | 4 | саморезы |
| ALWT-1400х600-RAL9016 | 0.505 м² | 1400 мм | 1395 мм | 600 мм | 596 мм | 255 мм | 891 мм | 60 | 4 | саморезы |
| ALWT-1400х625-RAL9016 | 0.526 м² | 1400 мм | 1395 мм | 625 мм | 621 мм | 255 мм | 891 мм | 63 | 4 | саморезы |
| ALWT-1400х650-RAL9016 | 0.547 м² | 1400 мм | 1395 мм | 650 мм | 646 мм | 255 мм | 891 мм | 65 | 4 | саморезы |
| ALWT-1425х100-RAL9016 | 0.086 м² | 1425 мм | 1420 мм | 100 мм | 96 мм | 259 мм | 907 мм | 10 | 4 | саморезы |
| ALWT-1425х125-RAL9016 | 0.107 м² | 1425 мм | 1420 мм | 125 мм | 121 мм | 259 мм | 907 мм | 13 | 4 | саморезы |
| ALWT-1425х150-RAL9016 | 0.129 м² | 1425 мм | 1420 мм | 150 мм | 146 мм | 259 мм | 907 мм | 15 | 4 | саморезы |
| ALWT-1425х200-RAL9016 | 0.171 м² | 1425 мм | 1420 мм | 200 мм | 196 мм | 259 мм | 907 мм | 20 | 4 | саморезы |
| ALWT-1425х225-RAL9016 | 0.193 м² | 1425 мм | 1420 мм | 225 мм | 221 мм | 259 мм | 907 мм | 23 | 4 | саморезы |
| ALWT-1425х250-RAL9016 | 0.214 м² | 1425 мм | 1420 мм | 250 мм | 246 мм | 259 мм | 907 мм | 25 | 4 | саморезы |
| ALWT-1425х300-RAL9016 | 0.257 м² | 1425 мм | 1420 мм | 300 мм | 296 мм | 259 мм | 907 мм | 30 | 4 | саморезы |
| ALWT-1425х325-RAL9016 | 0.279 м² | 1425 мм | 1420 мм | 325 мм | 321 мм | 259 мм | 907 мм | 33 | 4 | саморезы |
| ALWT-1425х350-RAL9016 | 0.300 м² | 1425 мм | 1420 мм | 350 мм | 346 мм | 259 мм | 907 мм | 35 | 4 | саморезы |
| ALWT-1425х400-RAL9016 | 0.343 м² | 1425 мм | 1420 мм | 400 мм | 396 мм | 259 мм | 907 мм | 40 | 4 | саморезы |
| ALWT-1425х425-RAL9016 | 0.364 м² | 1425 мм | 1420 мм | 425 мм | 421 мм | 259 мм | 907 мм | 43 | 4 | саморезы |
| ALWT-1425х450-RAL9016 | 0.386 м² | 1425 мм | 1420 мм | 450 мм | 446 мм | 259 мм | 907 мм | 45 | 4 | саморезы |
| ALWT-1425х500-RAL9016 | 0.429 м² | 1425 мм | 1420 мм | 500 мм | 496 мм | 259 мм | 907 мм | 50 | 4 | саморезы |
| ALWT-1425х525-RAL9016 | 0.450 м² | 1425 мм | 1420 мм | 525 мм | 521 мм | 259 мм | 907 мм | 53 | 4 | саморезы |
| ALWT-1425х550-RAL9016 | 0.472 м² | 1425 мм | 1420 мм | 550 мм | 546 мм | 259 мм | 907 мм | 55 | 4 | саморезы |
| ALWT-1425х600-RAL9016 | 0.514 м² | 1425 мм | 1420 мм | 600 мм | 596 мм | 259 мм | 907 мм | 60 | 4 | саморезы |
| ALWT-1425х625-RAL9016 | 0.536 м² | 1425 мм | 1420 мм | 625 мм | 621 мм | 259 мм | 907 мм | 63 | 4 | саморезы |
| ALWT-1425х650-RAL9016 | 0.557 м² | 1425 мм | 1420 мм | 650 мм | 646 мм | 259 мм | 907 мм | 65 | 4 | саморезы |
| ALWT-1450х100-RAL9016 | 0.087 м² | 1450 мм | 1445 мм | 100 мм | 96 мм | 264 мм | 923 мм | 10 | 4 | саморезы |
| ALWT-1450х125-RAL9016 | 0.109 м² | 1450 мм | 1445 мм | 125 мм | 121 мм | 264 мм | 923 мм | 13 | 4 | саморезы |
| ALWT-1450х150-RAL9016 | 0.131 м² | 1450 мм | 1445 мм | 150 мм | 146 мм | 264 мм | 923 мм | 15 | 4 | саморезы |
| ALWT-1450х200-RAL9016 | 0.174 м² | 1450 мм | 1445 мм | 200 мм | 196 мм | 264 мм | 923 мм | 20 | 4 | саморезы |
| ALWT-1450х225-RAL9016 | 0.196 м² | 1450 мм | 1445 мм | 225 мм | 221 мм | 264 мм | 923 мм | 23 | 4 | саморезы |
| ALWT-1450х250-RAL9016 | 0.218 м² | 1450 мм | 1445 мм | 250 мм | 246 мм | 264 мм | 923 мм | 25 | 4 | саморезы |
| ALWT-1450х300-RAL9016 | 0.262 м² | 1450 мм | 1445 мм | 300 мм | 296 мм | 264 мм | 923 мм | 30 | 4 | саморезы |
| ALWT-1450х325-RAL9016 | 0.284 м² | 1450 мм | 1445 мм | 325 мм | 321 мм | 264 мм | 923 мм | 33 | 4 | саморезы |
| ALWT-1450х350-RAL9016 | 0.305 м² | 1450 мм | 1445 мм | 350 мм | 346 мм | 264 мм | 923 мм | 35 | 4 | саморезы |
| ALWT-1450х400-RAL9016 | 0.349 м² | 1450 мм | 1445 мм | 400 мм | 396 мм | 264 мм | 923 мм | 40 | 4 | саморезы |
| ALWT-1450х425-RAL9016 | 0.371 м² | 1450 мм | 1445 мм | 425 мм | 421 мм | 264 мм | 923 мм | 43 | 4 | саморезы |
| ALWT-1450х450-RAL9016 | 0.393 м² | 1450 мм | 1445 мм | 450 мм | 446 мм | 264 мм | 923 мм | 45 | 4 | саморезы |
| ALWT-1450х500-RAL9016 | 0.436 м² | 1450 мм | 1445 мм | 500 мм | 496 мм | 264 мм | 923 мм | 50 | 4 | саморезы |
| ALWT-1450х525-RAL9016 | 0.458 м² | 1450 мм | 1445 мм | 525 мм | 521 мм | 264 мм | 923 мм | 53 | 4 | саморезы |
| ALWT-1450х550-RAL9016 | 0.480 м² | 1450 мм | 1445 мм | 550 мм | 546 мм | 264 мм | 923 мм | 55 | 4 | саморезы |
| ALWT-1450х600-RAL9016 | 0.523 м² | 1450 мм | 1445 мм | 600 мм | 596 мм | 264 мм | 923 мм | 60 | 4 | саморезы |
| ALWT-1450х625-RAL9016 | 0.545 м² | 1450 мм | 1445 мм | 625 мм | 621 мм | 264 мм | 923 мм | 63 | 4 | саморезы |
| ALWT-1450х650-RAL9016 | 0.567 м² | 1450 мм | 1445 мм | 650 мм | 646 мм | 264 мм | 923 мм | 65 | 4 | саморезы |
| ALWT-1500х100-RAL9016 | 0.090 м² | 1500 мм | 1495 мм | 100 мм | 96 мм | 273 мм | 955 мм | 10 | 4 | саморезы |
| ALWT-1500х125-RAL9016 | 0.113 м² | 1500 мм | 1495 мм | 125 мм | 121 мм | 273 мм | 955 мм | 13 | 4 | саморезы |
| ALWT-1500х150-RAL9016 | 0.135 м² | 1500 мм | 1495 мм | 150 мм | 146 мм | 273 мм | 955 мм | 15 | 4 | саморезы |
| ALWT-1500х200-RAL9016 | 0.180 м² | 1500 мм | 1495 мм | 200 мм | 196 мм | 273 мм | 955 мм | 20 | 4 | саморезы |
| ALWT-1500х225-RAL9016 | 0.203 м² | 1500 мм | 1495 мм | 225 мм | 221 мм | 273 мм | 955 мм | 23 | 4 | саморезы |
| ALWT-1500х250-RAL9016 | 0.226 м² | 1500 мм | 1495 мм | 250 мм | 246 мм | 273 мм | 955 мм | 25 | 4 | саморезы |
| ALWT-1500х300-RAL9016 | 0.271 м² | 1500 мм | 1495 мм | 300 мм | 296 мм | 273 мм | 955 мм | 30 | 4 | саморезы |
| ALWT-1500х325-RAL9016 | 0.293 м² | 1500 мм | 1495 мм | 325 мм | 321 мм | 273 мм | 955 мм | 33 | 4 | саморезы |
| ALWT-1500х350-RAL9016 | 0.316 м² | 1500 мм | 1495 мм | 350 мм | 346 мм | 273 мм | 955 мм | 35 | 4 | саморезы |
| ALWT-1500х400-RAL9016 | 0.361 м² | 1500 мм | 1495 мм | 400 мм | 396 мм | 273 мм | 955 мм | 40 | 4 | саморезы |
| ALWT-1500х425-RAL9016 | 0.384 м² | 1500 мм | 1495 мм | 425 мм | 421 мм | 273 мм | 955 мм | 43 | 4 | саморезы |
| ALWT-1500х450-RAL9016 | 0.406 м² | 1500 мм | 1495 мм | 450 мм | 446 мм | 273 мм | 955 мм | 45 | 4 | саморезы |
| ALWT-1500х500-RAL9016 | 0.451 м² | 1500 мм | 1495 мм | 500 мм | 496 мм | 273 мм | 955 мм | 50 | 4 | саморезы |
| ALWT-1500х525-RAL9016 | 0.474 м² | 1500 мм | 1495 мм | 525 мм | 521 мм | 273 мм | 955 мм | 53 | 4 | саморезы |
| ALWT-1500х550-RAL9016 | 0.496 м² | 1500 мм | 1495 мм | 550 мм | 546 мм | 273 мм | 955 мм | 55 | 4 | саморезы |
| ALWT-1500х600-RAL9016 | 0.541 м² | 1500 мм | 1495 мм | 600 мм | 596 мм | 273 мм | 955 мм | 60 | 4 | саморезы |
| ALWT-1500х625-RAL9016 | 0.564 м² | 1500 мм | 1495 мм | 625 мм | 621 мм | 273 мм | 955 мм | 63 | 4 | саморезы |
| ALWT-1500х650-RAL9016 | 0.587 м² | 1500 мм | 1495 мм | 650 мм | 646 мм | 273 мм | 955 мм | 65 | 4 | саморезы |
| ALWT-100х100-Z-АА | 0.006 м² | 100 мм | 95 мм | 100 мм | 96 мм | 18 мм | 64 мм | 10 | 2 | скрытые защелки |
| ALWT-125х100-Z-АА | 0.008 м² | 125 мм | 120 мм | 100 мм | 96 мм | 23 мм | 80 мм | 10 | 2 | скрытые защелки |
| ALWT-125х125-Z-АА | 0.009 м² | 125 мм | 120 мм | 125 мм | 121 мм | 23 мм | 80 мм | 13 | 2 | скрытые защелки |
| ALWT-150х100-Z-АА | 0.009 м² | 150 мм | 145 мм | 100 мм | 96 мм | 27 мм | 95 мм | 10 | 2 | скрытые защелки |
| ALWT-150х125-Z-АА | 0.011 м² | 150 мм | 145 мм | 125 мм | 121 мм | 27 мм | 95 мм | 13 | 2 | скрытые защелки |
| ALWT-150х150-Z-АА | 0.014 м² | 150 мм | 145 мм | 150 мм | 146 мм | 27 мм | 95 мм | 15 | 2 | скрытые защелки |
| ALWT-200х100-Z-АА | 0.012 м² | 200 мм | 195 мм | 100 мм | 96 мм | 36 мм | 127 мм | 10 | 2 | скрытые защелки |
| ALWT-200х125-Z-АА | 0.015 м² | 200 мм | 195 мм | 125 мм | 121 мм | 36 мм | 127 мм | 13 | 2 | скрытые защелки |
| ALWT-200х150-Z-АА | 0.018 м² | 200 мм | 195 мм | 150 мм | 146 мм | 36 мм | 127 мм | 15 | 2 | скрытые защелки |
| ALWT-200х200-Z-АА | 0.024 м² | 200 мм | 195 мм | 200 мм | 196 мм | 36 мм | 127 мм | 20 | 2 | скрытые защелки |
| ALWT-225х100-Z-АА | 0.014 м² | 225 мм | 220 мм | 100 мм | 96 мм | 41 мм | 143 мм | 10 | 2 | скрытые защелки |
| ALWT-225х125-Z-АА | 0.017 м² | 225 мм | 220 мм | 125 мм | 121 мм | 41 мм | 143 мм | 13 | 2 | скрытые защелки |
| ALWT-225х150-Z-АА | 0.020 м² | 225 мм | 220 мм | 150 мм | 146 мм | 41 мм | 143 мм | 15 | 2 | скрытые защелки |
| ALWT-225х200-Z-АА | 0.027 м² | 225 мм | 220 мм | 200 мм | 196 мм | 41 мм | 143 мм | 20 | 2 | скрытые защелки |
| ALWT-225х225-Z-АА | 0.030 м² | 225 мм | 220 мм | 225 мм | 221 мм | 41 мм | 143 мм | 23 | 2 | скрытые защелки |
| ALWT-250х100-Z-АА | 0.015 м² | 250 мм | 245 мм | 100 мм | 96 мм | 45 мм | 159 мм | 10 | 2 | скрытые защелки |
| ALWT-250х125-Z-АА | 0.019 м² | 250 мм | 245 мм | 125 мм | 121 мм | 45 мм | 159 мм | 13 | 2 | скрытые защелки |
| ALWT-250х150-Z-АА | 0.023 м² | 250 мм | 245 мм | 150 мм | 146 мм | 45 мм | 159 мм | 15 | 2 | скрытые защелки |
| ALWT-250х200-Z-АА | 0.030 м² | 250 мм | 245 мм | 200 мм | 196 мм | 45 мм | 159 мм | 20 | 2 | скрытые защелки |
| ALWT-250х225-Z-АА | 0.034 м² | 250 мм | 245 мм | 225 мм | 221 мм | 45 мм | 159 мм | 23 | 2 | скрытые защелки |
| ALWT-250х250-Z-АА | 0.038 м² | 250 мм | 245 мм | 250 мм | 246 мм | 45 мм | 159 мм | 25 | 2 | скрытые защелки |
| ALWT-300х100-Z-АА | 0.018 м² | 300 мм | 295 мм | 100 мм | 96 мм | 55 мм | 191 мм | 10 | 2 | скрытые защелки |
| ALWT-300х125-Z-АА | 0.023 м² | 300 мм | 295 мм | 125 мм | 121 мм | 55 мм | 191 мм | 13 | 2 | скрытые защелки |
| ALWT-300х150-Z-АА | 0.027 м² | 300 мм | 295 мм | 150 мм | 146 мм | 55 мм | 191 мм | 15 | 2 | скрытые защелки |
| ALWT-300х200-Z-АА | 0.036 м² | 300 мм | 295 мм | 200 мм | 196 мм | 55 мм | 191 мм | 20 | 2 | скрытые защелки |
| ALWT-300х225-Z-АА | 0.041 м² | 300 мм | 295 мм | 225 мм | 221 мм | 55 мм | 191 мм | 23 | 2 | скрытые защелки |
| ALWT-300х250-Z-АА | 0.045 м² | 300 мм | 295 мм | 250 мм | 246 мм | 55 мм | 191 мм | 25 | 2 | скрытые защелки |
| ALWT-300х300-Z-АА | 0.054 м² | 300 мм | 295 мм | 300 мм | 296 мм | 55 мм | 191 мм | 30 | 2 | скрытые защелки |
| ALWT-325х100-Z-АА | 0.020 м² | 325 мм | 320 мм | 100 мм | 96 мм | 59 мм | 207 мм | 10 | 2 | скрытые защелки |
| ALWT-325х125-Z-АА | 0.024 м² | 325 мм | 320 мм | 125 мм | 121 мм | 59 мм | 207 мм | 13 | 2 | скрытые защелки |
| ALWT-325х150-Z-АА | 0.029 м² | 325 мм | 320 мм | 150 мм | 146 мм | 59 мм | 207 мм | 15 | 2 | скрытые защелки |
| ALWT-325х200-Z-АА | 0.039 м² | 325 мм | 320 мм | 200 мм | 196 мм | 59 мм | 207 мм | 20 | 2 | скрытые защелки |
| ALWT-325х225-Z-АА | 0.044 м² | 325 мм | 320 мм | 225 мм | 221 мм | 59 мм | 207 мм | 23 | 2 | скрытые защелки |
| ALWT-325х250-Z-АА | 0.049 м² | 325 мм | 320 мм | 250 мм | 246 мм | 59 мм | 207 мм | 25 | 2 | скрытые защелки |
| ALWT-325х300-Z-АА | 0.059 м² | 325 мм | 320 мм | 300 мм | 296 мм | 59 мм | 207 мм | 30 | 2 | скрытые защелки |
| ALWT-325х325-Z-АА | 0.064 м² | 325 мм | 320 мм | 325 мм | 321 мм | 59 мм | 207 мм | 33 | 2 | скрытые защелки |
| ALWT-350х100-Z-АА | 0.021 м² | 350 мм | 345 мм | 100 мм | 96 мм | 64 мм | 223 мм | 10 | 2 | скрытые защелки |
| ALWT-350х125-Z-АА | 0.026 м² | 350 мм | 345 мм | 125 мм | 121 мм | 64 мм | 223 мм | 13 | 2 | скрытые защелки |
| ALWT-350х150-Z-АА | 0.032 м² | 350 мм | 345 мм | 150 мм | 146 мм | 64 мм | 223 мм | 15 | 2 | скрытые защелки |
| ALWT-350х200-Z-АА | 0.042 м² | 350 мм | 345 мм | 200 мм | 196 мм | 64 мм | 223 мм | 20 | 2 | скрытые защелки |
| ALWT-350х225-Z-АА | 0.047 м² | 350 мм | 345 мм | 225 мм | 221 мм | 64 мм | 223 мм | 23 | 2 | скрытые защелки |
| ALWT-350х250-Z-АА | 0.053 м² | 350 мм | 345 мм | 250 мм | 246 мм | 64 мм | 223 мм | 25 | 2 | скрытые защелки |
| ALWT-350х300-Z-АА | 0.063 м² | 350 мм | 345 мм | 300 мм | 296 мм | 64 мм | 223 мм | 30 | 2 | скрытые защелки |
| ALWT-350х325-Z-АА | 0.068 м² | 350 мм | 345 мм | 325 мм | 321 мм | 64 мм | 223 мм | 33 | 2 | скрытые защелки |
| ALWT-350х350-Z-АА | 0.074 м² | 350 мм | 345 мм | 350 мм | 346 мм | 64 мм | 223 мм | 35 | 2 | скрытые защелки |
| ALWT-400х100-Z-АА | 0.024 м² | 400 мм | 395 мм | 100 мм | 96 мм | 73 мм | 255 мм | 10 | 3 | скрытые защелки |
| ALWT-400х125-Z-АА | 0.030 м² | 400 мм | 395 мм | 125 мм | 121 мм | 73 мм | 255 мм | 13 | 3 | скрытые защелки |
| ALWT-400х150-Z-АА | 0.036 м² | 400 мм | 395 мм | 150 мм | 146 мм | 73 мм | 255 мм | 15 | 3 | скрытые защелки |
| ALWT-400х200-Z-АА | 0.048 м² | 400 мм | 395 мм | 200 мм | 196 мм | 73 мм | 255 мм | 20 | 3 | скрытые защелки |
| ALWT-400х225-Z-АА | 0.054 м² | 400 мм | 395 мм | 225 мм | 221 мм | 73 мм | 255 мм | 23 | 3 | скрытые защелки |
| ALWT-400х250-Z-АА | 0.060 м² | 400 мм | 395 мм | 250 мм | 246 мм | 73 мм | 255 мм | 25 | 3 | скрытые защелки |
| ALWT-400х300-Z-АА | 0.072 м² | 400 мм | 395 мм | 300 мм | 296 мм | 73 мм | 255 мм | 30 | 3 | скрытые защелки |
| ALWT-400х325-Z-АА | 0.078 м² | 400 мм | 395 мм | 325 мм | 321 мм | 73 мм | 255 мм | 33 | 3 | скрытые защелки |
| ALWT-400х350-Z-АА | 0.084 м² | 400 мм | 395 мм | 350 мм | 346 мм | 73 мм | 255 мм | 35 | 3 | скрытые защелки |
| ALWT-400х400-Z-АА | 0.096 м² | 400 мм | 395 мм | 400 мм | 396 мм | 73 мм | 255 мм | 40 | 3 | скрытые защелки |
| ALWT-425х100-Z-АА | 0.026 м² | 425 мм | 420 мм | 100 мм | 96 мм | 77 мм | 270 мм | 10 | 3 | скрытые защелки |
| ALWT-425х125-Z-АА | 0.032 м² | 425 мм | 420 мм | 125 мм | 121 мм | 77 мм | 270 мм | 13 | 3 | скрытые защелки |
| ALWT-425х150-Z-АА | 0.038 м² | 425 мм | 420 мм | 150 мм | 146 мм | 77 мм | 270 мм | 15 | 3 | скрытые защелки |
| ALWT-425х200-Z-АА | 0.051 м² | 425 мм | 420 мм | 200 мм | 196 мм | 77 мм | 270 мм | 20 | 3 | скрытые защелки |
| ALWT-425х225-Z-АА | 0.058 м² | 425 мм | 420 мм | 225 мм | 221 мм | 77 мм | 270 мм | 23 | 3 | скрытые защелки |
| ALWT-425х250-Z-АА | 0.064 м² | 425 мм | 420 мм | 250 мм | 246 мм | 77 мм | 270 мм | 25 | 3 | скрытые защелки |
| ALWT-425х300-Z-АА | 0.077 м² | 425 мм | 420 мм | 300 мм | 296 мм | 77 мм | 270 мм | 30 | 3 | скрытые защелки |
| ALWT-425х325-Z-АА | 0.083 м² | 425 мм | 420 мм | 325 мм | 321 мм | 77 мм | 270 мм | 33 | 3 | скрытые защелки |
| ALWT-425х350-Z-АА | 0.089 м² | 425 мм | 420 мм | 350 мм | 346 мм | 77 мм | 270 мм | 35 | 3 | скрытые защелки |
| ALWT-425х400-Z-АА | 0.102 м² | 425 мм | 420 мм | 400 мм | 396 мм | 77 мм | 270 мм | 40 | 3 | скрытые защелки |
| ALWT-425х425-Z-АА | 0.109 м² | 425 мм | 420 мм | 425 мм | 421 мм | 77 мм | 270 мм | 43 | 3 | скрытые защелки |
| ALWT-450х100-Z-АА | 0.027 м² | 450 мм | 445 мм | 100 мм | 96 мм | 82 мм | 286 мм | 10 | 3 | скрытые защелки |
| ALWT-450х125-Z-АА | 0.034 м² | 450 мм | 445 мм | 125 мм | 121 мм | 82 мм | 286 мм | 13 | 3 | скрытые защелки |
| ALWT-450х150-Z-АА | 0.041 м² | 450 мм | 445 мм | 150 мм | 146 мм | 82 мм | 286 мм | 15 | 3 | скрытые защелки |
| ALWT-450х200-Z-АА | 0.054 м² | 450 мм | 445 мм | 200 мм | 196 мм | 82 мм | 286 мм | 20 | 3 | скрытые защелки |
| ALWT-450х225-Z-АА | 0.061 м² | 450 мм | 445 мм | 225 мм | 221 мм | 82 мм | 286 мм | 23 | 3 | скрытые защелки |
| ALWT-450х250-Z-АА | 0.068 м² | 450 мм | 445 мм | 250 мм | 246 мм | 82 мм | 286 мм | 25 | 3 | скрытые защелки |
| ALWT-450х300-Z-АА | 0.081 м² | 450 мм | 445 мм | 300 мм | 296 мм | 82 мм | 286 мм | 30 | 3 | скрытые защелки |
| ALWT-450х325-Z-АА | 0.088 м² | 450 мм | 445 мм | 325 мм | 321 мм | 82 мм | 286 мм | 33 | 3 | скрытые защелки |
| ALWT-450х350-Z-АА | 0.095 м² | 450 мм | 445 мм | 350 мм | 346 мм | 82 мм | 286 мм | 35 | 3 | скрытые защелки |
| ALWT-450х400-Z-АА | 0.108 м² | 450 мм | 445 мм | 400 мм | 396 мм | 82 мм | 286 мм | 40 | 3 | скрытые защелки |
| ALWT-450х425-Z-АА | 0.115 м² | 450 мм | 445 мм | 425 мм | 421 мм | 82 мм | 286 мм | 43 | 3 | скрытые защелки |
| ALWT-450х450-Z-АА | 0.122 м² | 450 мм | 445 мм | 450 мм | 446 мм | 82 мм | 286 мм | 45 | 3 | скрытые защелки |
| ALWT-500х100-Z-АА | 0.030 м² | 500 мм | 495 мм | 100 мм | 96 мм | 91 мм | 318 мм | 10 | 3 | скрытые защелки |
| ALWT-500х125-Z-АА | 0.038 м² | 500 мм | 495 мм | 125 мм | 121 мм | 91 мм | 318 мм | 13 | 3 | скрытые защелки |
| ALWT-500х150-Z-АА | 0.045 м² | 500 мм | 495 мм | 150 мм | 146 мм | 91 мм | 318 мм | 15 | 3 | скрытые защелки |
| ALWT-500х200-Z-АА | 0.060 м² | 500 мм | 495 мм | 200 мм | 196 мм | 91 мм | 318 мм | 20 | 3 | скрытые защелки |
| ALWT-500х225-Z-АА | 0.068 м² | 500 мм | 495 мм | 225 мм | 221 мм | 91 мм | 318 мм | 23 | 3 | скрытые защелки |
| ALWT-500х250-Z-АА | 0.075 м² | 500 мм | 495 мм | 250 мм | 246 мм | 91 мм | 318 мм | 25 | 3 | скрытые защелки |
| ALWT-500х300-Z-АА | 0.090 м² | 500 мм | 495 мм | 300 мм | 296 мм | 91 мм | 318 мм | 30 | 3 | скрытые защелки |
| ALWT-500х325-Z-АА | 0.098 м² | 500 мм | 495 мм | 325 мм | 321 мм | 91 мм | 318 мм | 33 | 3 | скрытые защелки |
| ALWT-500х350-Z-АА | 0.105 м² | 500 мм | 495 мм | 350 мм | 346 мм | 91 мм | 318 мм | 35 | 3 | скрытые защелки |
| ALWT-500х400-Z-АА | 0.120 м² | 500 мм | 495 мм | 400 мм | 396 мм | 91 мм | 318 мм | 40 | 3 | скрытые защелки |
| ALWT-500х425-Z-АА | 0.128 м² | 500 мм | 495 мм | 425 мм | 421 мм | 91 мм | 318 мм | 43 | 3 | скрытые защелки |
| ALWT-500х450-Z-АА | 0.135 м² | 500 мм | 495 мм | 450 мм | 446 мм | 91 мм | 318 мм | 45 | 3 | скрытые защелки |
| ALWT-500х500-Z-АА | 0.150 м² | 500 мм | 495 мм | 500 мм | 496 мм | 91 мм | 318 мм | 50 | 3 | скрытые защелки |
| ALWT-525х100-Z-АА | 0.032 м² | 525 мм | 520 мм | 100 мм | 96 мм | 95 мм | 334 мм | 10 | 3 | скрытые защелки |
| ALWT-525х125-Z-АА | 0.039 м² | 525 мм | 520 мм | 125 мм | 121 мм | 95 мм | 334 мм | 13 | 3 | скрытые защелки |
| ALWT-525х150-Z-АА | 0.047 м² | 525 мм | 520 мм | 150 мм | 146 мм | 95 мм | 334 мм | 15 | 3 | скрытые защелки |
| ALWT-525х200-Z-АА | 0.063 м² | 525 мм | 520 мм | 200 мм | 196 мм | 95 мм | 334 мм | 20 | 3 | скрытые защелки |
| ALWT-525х225-Z-АА | 0.071 м² | 525 мм | 520 мм | 225 мм | 221 мм | 95 мм | 334 мм | 23 | 3 | скрытые защелки |
| ALWT-525х250-Z-АА | 0.079 м² | 525 мм | 520 мм | 250 мм | 246 мм | 95 мм | 334 мм | 25 | 3 | скрытые защелки |
| ALWT-525х300-Z-АА | 0.095 м² | 525 мм | 520 мм | 300 мм | 296 мм | 95 мм | 334 мм | 30 | 3 | скрытые защелки |
| ALWT-525х325-Z-АА | 0.103 м² | 525 мм | 520 мм | 325 мм | 321 мм | 95 мм | 334 мм | 33 | 3 | скрытые защелки |
| ALWT-525х350-Z-АА | 0.111 м² | 525 мм | 520 мм | 350 мм | 346 мм | 95 мм | 334 мм | 35 | 3 | скрытые защелки |
| ALWT-525х400-Z-АА | 0.126 м² | 525 мм | 520 мм | 400 мм | 396 мм | 95 мм | 334 мм | 40 | 3 | скрытые защелки |
| ALWT-525х425-Z-АА | 0.134 м² | 525 мм | 520 мм | 425 мм | 421 мм | 95 мм | 334 мм | 43 | 3 | скрытые защелки |
| ALWT-525х450-Z-АА | 0.142 м² | 525 мм | 520 мм | 450 мм | 446 мм | 95 мм | 334 мм | 45 | 3 | скрытые защелки |
| ALWT-525х500-Z-АА | 0.158 м² | 525 мм | 520 мм | 500 мм | 496 мм | 95 мм | 334 мм | 50 | 3 | скрытые защелки |
| ALWT-525х525-Z-АА | 0.166 м² | 525 мм | 520 мм | 525 мм | 521 мм | 95 мм | 334 мм | 53 | 3 | скрытые защелки |
| ALWT-550х100-Z-АА | 0.033 м² | 550 мм | 545 мм | 100 мм | 96 мм | 100 мм | 350 мм | 10 | 3 | скрытые защелки |
| ALWT-550х125-Z-АА | 0.041 м² | 550 мм | 545 мм | 125 мм | 121 мм | 100 мм | 350 мм | 13 | 3 | скрытые защелки |
| ALWT-550х150-Z-АА | 0.050 м² | 550 мм | 545 мм | 150 мм | 146 мм | 100 мм | 350 мм | 15 | 3 | скрытые защелки |
| ALWT-550х200-Z-АА | 0.066 м² | 550 мм | 545 мм | 200 мм | 196 мм | 100 мм | 350 мм | 20 | 3 | скрытые защелки |
| ALWT-550х225-Z-АА | 0.074 м² | 550 мм | 545 мм | 225 мм | 221 мм | 100 мм | 350 мм | 23 | 3 | скрытые защелки |
| ALWT-550х250-Z-АА | 0.083 м² | 550 мм | 545 мм | 250 мм | 246 мм | 100 мм | 350 мм | 25 | 3 | скрытые защелки |
| ALWT-550х300-Z-АА | 0.099 м² | 550 мм | 545 мм | 300 мм | 296 мм | 100 мм | 350 мм | 30 | 3 | скрытые защелки |
| ALWT-550х325-Z-АА | 0.108 м² | 550 мм | 545 мм | 325 мм | 321 мм | 100 мм | 350 мм | 33 | 3 | скрытые защелки |
| ALWT-550х350-Z-АА | 0.116 м² | 550 мм | 545 мм | 350 мм | 346 мм | 100 мм | 350 мм | 35 | 3 | скрытые защелки |
| ALWT-550х400-Z-АА | 0.132 м² | 550 мм | 545 мм | 400 мм | 396 мм | 100 мм | 350 мм | 40 | 3 | скрытые защелки |
| ALWT-550х425-Z-АА | 0.141 м² | 550 мм | 545 мм | 425 мм | 421 мм | 100 мм | 350 мм | 43 | 3 | скрытые защелки |
| ALWT-550х450-Z-АА | 0.149 м² | 550 мм | 545 мм | 450 мм | 446 мм | 100 мм | 350 мм | 45 | 3 | скрытые защелки |
| ALWT-550х500-Z-АА | 0.165 м² | 550 мм | 545 мм | 500 мм | 496 мм | 100 мм | 350 мм | 50 | 3 | скрытые защелки |
| ALWT-550х525-Z-АА | 0.174 м² | 550 мм | 545 мм | 525 мм | 521 мм | 100 мм | 350 мм | 53 | 3 | скрытые защелки |
| ALWT-550х550-Z-АА | 0.182 м² | 550 мм | 545 мм | 550 мм | 546 мм | 100 мм | 350 мм | 55 | 3 | скрытые защелки |
| ALWT-600х100-Z-АА | 0.036 м² | 600 мм | 595 мм | 100 мм | 96 мм | 109 мм | 382 мм | 10 | 3 | скрытые защелки |
| ALWT-600х125-Z-АА | 0.045 м² | 600 мм | 595 мм | 125 мм | 121 мм | 109 мм | 382 мм | 13 | 3 | скрытые защелки |
| ALWT-600х150-Z-АА | 0.054 м² | 600 мм | 595 мм | 150 мм | 146 мм | 109 мм | 382 мм | 15 | 3 | скрытые защелки |
| ALWT-600х200-Z-АА | 0.072 м² | 600 мм | 595 мм | 200 мм | 196 мм | 109 мм | 382 мм | 20 | 3 | скрытые защелки |
| ALWT-600х225-Z-АА | 0.081 м² | 600 мм | 595 мм | 225 мм | 221 мм | 109 мм | 382 мм | 23 | 3 | скрытые защелки |
| ALWT-600х250-Z-АА | 0.090 м² | 600 мм | 595 мм | 250 мм | 246 мм | 109 мм | 382 мм | 25 | 3 | скрытые защелки |
| ALWT-600х300-Z-АА | 0.108 м² | 600 мм | 595 мм | 300 мм | 296 мм | 109 мм | 382 мм | 30 | 3 | скрытые защелки |
| ALWT-600х325-Z-АА | 0.117 м² | 600 мм | 595 мм | 325 мм | 321 мм | 109 мм | 382 мм | 33 | 3 | скрытые защелки |
| ALWT-600х350-Z-АА | 0.126 м² | 600 мм | 595 мм | 350 мм | 346 мм | 109 мм | 382 мм | 35 | 3 | скрытые защелки |
| ALWT-600х400-Z-АА | 0.144 м² | 600 мм | 595 мм | 400 мм | 396 мм | 109 мм | 382 мм | 40 | 3 | скрытые защелки |
| ALWT-600х425-Z-АА | 0.153 м² | 600 мм | 595 мм | 425 мм | 421 мм | 109 мм | 382 мм | 43 | 3 | скрытые защелки |
| ALWT-600х450-Z-АА | 0.162 м² | 600 мм | 595 мм | 450 мм | 446 мм | 109 мм | 382 мм | 45 | 3 | скрытые защелки |
| ALWT-600х500-Z-АА | 0.180 м² | 600 мм | 595 мм | 500 мм | 496 мм | 109 мм | 382 мм | 50 | 3 | скрытые защелки |
| ALWT-600х525-Z-АА | 0.190 м² | 600 мм | 595 мм | 525 мм | 521 мм | 109 мм | 382 мм | 53 | 3 | скрытые защелки |
| ALWT-600х550-Z-АА | 0.199 м² | 600 мм | 595 мм | 550 мм | 546 мм | 109 мм | 382 мм | 55 | 3 | скрытые защелки |
| ALWT-600х600-Z-АА | 0.217 м² | 600 мм | 595 мм | 600 мм | 596 мм | 109 мм | 382 мм | 60 | 3 | скрытые защелки |
| ALWT-625х100-Z-АА | 0.038 м² | 625 мм | 620 мм | 100 мм | 96 мм | 114 мм | 398 мм | 10 | 3 | скрытые защелки |
| ALWT-625х125-Z-АА | 0.047 м² | 625 мм | 620 мм | 125 мм | 121 мм | 114 мм | 398 мм | 13 | 3 | скрытые защелки |
| ALWT-625х150-Z-АА | 0.056 м² | 625 мм | 620 мм | 150 мм | 146 мм | 114 мм | 398 мм | 15 | 3 | скрытые защелки |
| ALWT-625х200-Z-АА | 0.075 м² | 625 мм | 620 мм | 200 мм | 196 мм | 114 мм | 398 мм | 20 | 3 | скрытые защелки |
| ALWT-625х225-Z-АА | 0.085 м² | 625 мм | 620 мм | 225 мм | 221 мм | 114 мм | 398 мм | 23 | 3 | скрытые защелки |
| ALWT-625х250-Z-АА | 0.094 м² | 625 мм | 620 мм | 250 мм | 246 мм | 114 мм | 398 мм | 25 | 3 | скрытые защелки |
| ALWT-625х300-Z-АА | 0.113 м² | 625 мм | 620 мм | 300 мм | 296 мм | 114 мм | 398 мм | 30 | 3 | скрытые защелки |
| ALWT-625х325-Z-АА | 0.122 м² | 625 мм | 620 мм | 325 мм | 321 мм | 114 мм | 398 мм | 33 | 3 | скрытые защелки |
| ALWT-625х350-Z-АА | 0.132 м² | 625 мм | 620 мм | 350 мм | 346 мм | 114 мм | 398 мм | 35 | 3 | скрытые защелки |
| ALWT-625х400-Z-АА | 0.150 м² | 625 мм | 620 мм | 400 мм | 396 мм | 114 мм | 398 мм | 40 | 3 | скрытые защелки |
| ALWT-625х425-Z-АА | 0.160 м² | 625 мм | 620 мм | 425 мм | 421 мм | 114 мм | 398 мм | 43 | 3 | скрытые защелки |
| ALWT-625х450-Z-АА | 0.169 м² | 625 мм | 620 мм | 450 мм | 446 мм | 114 мм | 398 мм | 45 | 3 | скрытые защелки |
| ALWT-625х500-Z-АА | 0.188 м² | 625 мм | 620 мм | 500 мм | 496 мм | 114 мм | 398 мм | 50 | 3 | скрытые защелки |
| ALWT-625х525-Z-АА | 0.197 м² | 625 мм | 620 мм | 525 мм | 521 мм | 114 мм | 398 мм | 53 | 3 | скрытые защелки |
| ALWT-625х550-Z-АА | 0.207 м² | 625 мм | 620 мм | 550 мм | 546 мм | 114 мм | 398 мм | 55 | 3 | скрытые защелки |
| ALWT-625х600-Z-АА | 0.226 м² | 625 мм | 620 мм | 600 мм | 596 мм | 114 мм | 398 мм | 60 | 3 | скрытые защелки |
| ALWT-625х625-Z-АА | 0.235 м² | 625 мм | 620 мм | 625 мм | 621 мм | 114 мм | 398 мм | 63 | 3 | скрытые защелки |
| ALWT-650х100-Z-АА | 0.039 м² | 650 мм | 645 мм | 100 мм | 96 мм | 118 мм | 414 мм | 10 | 3 | скрытые защелки |
| ALWT-650х125-Z-АА | 0.049 м² | 650 мм | 645 мм | 125 мм | 121 мм | 118 мм | 414 мм | 13 | 3 | скрытые защелки |
| ALWT-650х150-Z-АА | 0.059 м² | 650 мм | 645 мм | 150 мм | 146 мм | 118 мм | 414 мм | 15 | 3 | скрытые защелки |
| ALWT-650х200-Z-АА | 0.078 м² | 650 мм | 645 мм | 200 мм | 196 мм | 118 мм | 414 мм | 20 | 3 | скрытые защелки |
| ALWT-650х225-Z-АА | 0.088 м² | 650 мм | 645 мм | 225 мм | 221 мм | 118 мм | 414 мм | 23 | 3 | скрытые защелки |
| ALWT-650х250-Z-АА | 0.098 м² | 650 мм | 645 мм | 250 мм | 246 мм | 118 мм | 414 мм | 25 | 3 | скрытые защелки |
| ALWT-650х300-Z-АА | 0.117 м² | 650 мм | 645 мм | 300 мм | 296 мм | 118 мм | 414 мм | 30 | 3 | скрытые защелки |
| ALWT-650х325-Z-АА | 0.127 м² | 650 мм | 645 мм | 325 мм | 321 мм | 118 мм | 414 мм | 33 | 3 | скрытые защелки |
| ALWT-650х350-Z-АА | 0.137 м² | 650 мм | 645 мм | 350 мм | 346 мм | 118 мм | 414 мм | 35 | 3 | скрытые защелки |
| ALWT-650х400-Z-АА | 0.156 м² | 650 мм | 645 мм | 400 мм | 396 мм | 118 мм | 414 мм | 40 | 3 | скрытые защелки |
| ALWT-650х425-Z-АА | 0.166 м² | 650 мм | 645 мм | 425 мм | 421 мм | 118 мм | 414 мм | 43 | 3 | скрытые защелки |
| ALWT-650х450-Z-АА | 0.176 м² | 650 мм | 645 мм | 450 мм | 446 мм | 118 мм | 414 мм | 45 | 3 | скрытые защелки |
| ALWT-650х500-Z-АА | 0.196 м² | 650 мм | 645 мм | 500 мм | 496 мм | 118 мм | 414 мм | 50 | 3 | скрытые защелки |
| ALWT-650х525-Z-АА | 0.205 м² | 650 мм | 645 мм | 525 мм | 521 мм | 118 мм | 414 мм | 53 | 3 | скрытые защелки |
| ALWT-650х550-Z-АА | 0.215 м² | 650 мм | 645 мм | 550 мм | 546 мм | 118 мм | 414 мм | 55 | 3 | скрытые защелки |
| ALWT-650х600-Z-АА | 0.235 м² | 650 мм | 645 мм | 600 мм | 596 мм | 118 мм | 414 мм | 60 | 3 | скрытые защелки |
| ALWT-650х625-Z-АА | 0.244 м² | 650 мм | 645 мм | 625 мм | 621 мм | 118 мм | 414 мм | 63 | 3 | скрытые защелки |
| ALWT-650х650-Z-АА | 0.254 м² | 650 мм | 645 мм | 650 мм | 646 мм | 118 мм | 414 мм | 65 | 3 | скрытые защелки |
| ALWT-700х100-Z-АА | 0.042 м² | 700 мм | 695 мм | 100 мм | 96 мм | 127 мм | 445 мм | 10 | 3 | скрытые защелки |
| ALWT-700х125-Z-АА | 0.053 м² | 700 мм | 695 мм | 125 мм | 121 мм | 127 мм | 445 мм | 13 | 3 | скрытые защелки |
| ALWT-700х150-Z-АА | 0.063 м² | 700 мм | 695 мм | 150 мм | 146 мм | 127 мм | 445 мм | 15 | 3 | скрытые защелки |
| ALWT-700х200-Z-АА | 0.084 м² | 700 мм | 695 мм | 200 мм | 196 мм | 127 мм | 445 мм | 20 | 3 | скрытые защелки |
| ALWT-700х225-Z-АА | 0.095 м² | 700 мм | 695 мм | 225 мм | 221 мм | 127 мм | 445 мм | 23 | 3 | скрытые защелки |
| ALWT-700х250-Z-АА | 0.105 м² | 700 мм | 695 мм | 250 мм | 246 мм | 127 мм | 445 мм | 25 | 3 | скрытые защелки |
| ALWT-700х300-Z-АА | 0.126 м² | 700 мм | 695 мм | 300 мм | 296 мм | 127 мм | 445 мм | 30 | 3 | скрытые защелки |
| ALWT-700х325-Z-АА | 0.137 м² | 700 мм | 695 мм | 325 мм | 321 мм | 127 мм | 445 мм | 33 | 3 | скрытые защелки |
| ALWT-700х350-Z-АА | 0.147 м² | 700 мм | 695 мм | 350 мм | 346 мм | 127 мм | 445 мм | 35 | 3 | скрытые защелки |
| ALWT-700х400-Z-АА | 0.168 м² | 700 мм | 695 мм | 400 мм | 396 мм | 127 мм | 445 мм | 40 | 3 | скрытые защелки |
| ALWT-700х425-Z-АА | 0.179 м² | 700 мм | 695 мм | 425 мм | 421 мм | 127 мм | 445 мм | 43 | 3 | скрытые защелки |
| ALWT-700х450-Z-АА | 0.190 м² | 700 мм | 695 мм | 450 мм | 446 мм | 127 мм | 445 мм | 45 | 3 | скрытые защелки |
| ALWT-700х500-Z-АА | 0.211 м² | 700 мм | 695 мм | 500 мм | 496 мм | 127 мм | 445 мм | 50 | 3 | скрытые защелки |
| ALWT-700х525-Z-АА | 0.221 м² | 700 мм | 695 мм | 525 мм | 521 мм | 127 мм | 445 мм | 53 | 3 | скрытые защелки |
| ALWT-700х550-Z-АА | 0.232 м² | 700 мм | 695 мм | 550 мм | 546 мм | 127 мм | 445 мм | 55 | 3 | скрытые защелки |
| ALWT-700х600-Z-АА | 0.253 м² | 700 мм | 695 мм | 600 мм | 596 мм | 127 мм | 445 мм | 60 | 3 | скрытые защелки |
| ALWT-700х625-Z-АА | 0.263 м² | 700 мм | 695 мм | 625 мм | 621 мм | 127 мм | 445 мм | 63 | 3 | скрытые защелки |
| ALWT-700х650-Z-АА | 0.274 м² | 700 мм | 695 мм | 650 мм | 646 мм | 127 мм | 445 мм | 65 | 3 | скрытые защелки |
| ALWT-725х100-Z-АА | 0.044 м² | 725 мм | 720 мм | 100 мм | 96 мм | 132 мм | 461 мм | 10 | 3 | скрытые защелки |
| ALWT-725х125-Z-АА | 0.055 м² | 725 мм | 720 мм | 125 мм | 121 мм | 132 мм | 461 мм | 13 | 3 | скрытые защелки |
| ALWT-725х150-Z-АА | 0.065 м² | 725 мм | 720 мм | 150 мм | 146 мм | 132 мм | 461 мм | 15 | 3 | скрытые защелки |
| ALWT-725х200-Z-АА | 0.087 м² | 725 мм | 720 мм | 200 мм | 196 мм | 132 мм | 461 мм | 20 | 3 | скрытые защелки |
| ALWT-725х225-Z-АА | 0.098 м² | 725 мм | 720 мм | 225 мм | 221 мм | 132 мм | 461 мм | 23 | 3 | скрытые защелки |
| ALWT-725х250-Z-АА | 0.109 м² | 725 мм | 720 мм | 250 мм | 246 мм | 132 мм | 461 мм | 25 | 3 | скрытые защелки |
| ALWT-725х300-Z-АА | 0.131 м² | 725 мм | 720 мм | 300 мм | 296 мм | 132 мм | 461 мм | 30 | 3 | скрытые защелки |
| ALWT-725х325-Z-АА | 0.142 м² | 725 мм | 720 мм | 325 мм | 321 мм | 132 мм | 461 мм | 33 | 3 | скрытые защелки |
| ALWT-725х350-Z-АА | 0.153 м² | 725 мм | 720 мм | 350 мм | 346 мм | 132 мм | 461 мм | 35 | 3 | скрытые защелки |
| ALWT-725х400-Z-АА | 0.174 м² | 725 мм | 720 мм | 400 мм | 396 мм | 132 мм | 461 мм | 40 | 3 | скрытые защелки |
| ALWT-725х425-Z-АА | 0.185 м² | 725 мм | 720 мм | 425 мм | 421 мм | 132 мм | 461 мм | 43 | 3 | скрытые защелки |
| ALWT-725х450-Z-АА | 0.196 м² | 725 мм | 720 мм | 450 мм | 446 мм | 132 мм | 461 мм | 45 | 3 | скрытые защелки |
| ALWT-725х500-Z-АА | 0.218 м² | 725 мм | 720 мм | 500 мм | 496 мм | 132 мм | 461 мм | 50 | 3 | скрытые защелки |
| ALWT-725х525-Z-АА | 0.229 м² | 725 мм | 720 мм | 525 мм | 521 мм | 132 мм | 461 мм | 53 | 3 | скрытые защелки |
| ALWT-725х550-Z-АА | 0.240 м² | 725 мм | 720 мм | 550 мм | 546 мм | 132 мм | 461 мм | 55 | 3 | скрытые защелки |
| ALWT-725х600-Z-АА | 0.262 м² | 725 мм | 720 мм | 600 мм | 596 мм | 132 мм | 461 мм | 60 | 3 | скрытые защелки |
| ALWT-725х625-Z-АА | 0.273 м² | 725 мм | 720 мм | 625 мм | 621 мм | 132 мм | 461 мм | 63 | 3 | скрытые защелки |
| ALWT-725х650-Z-АА | 0.284 м² | 725 мм | 720 мм | 650 мм | 646 мм | 132 мм | 461 мм | 65 | 3 | скрытые защелки |
| ALWT-750х100-Z-АА | 0.045 м² | 750 мм | 745 мм | 100 мм | 96 мм | 136 мм | 477 мм | 10 | 3 | скрытые защелки |
| ALWT-750х125-Z-АА | 0.056 м² | 750 мм | 745 мм | 125 мм | 121 мм | 136 мм | 477 мм | 13 | 3 | скрытые защелки |
| ALWT-750х150-Z-АА | 0.068 м² | 750 мм | 745 мм | 150 мм | 146 мм | 136 мм | 477 мм | 15 | 3 | скрытые защелки |
| ALWT-750х200-Z-АА | 0.090 м² | 750 мм | 745 мм | 200 мм | 196 мм | 136 мм | 477 мм | 20 | 3 | скрытые защелки |
| ALWT-750х225-Z-АА | 0.102 м² | 750 мм | 745 мм | 225 мм | 221 мм | 136 мм | 477 мм | 23 | 3 | скрытые защелки |
| ALWT-750х250-Z-АА | 0.113 м² | 750 мм | 745 мм | 250 мм | 246 мм | 136 мм | 477 мм | 25 | 3 | скрытые защелки |
| ALWT-750х300-Z-АА | 0.135 м² | 750 мм | 745 мм | 300 мм | 296 мм | 136 мм | 477 мм | 30 | 3 | скрытые защелки |
| ALWT-750х325-Z-АА | 0.147 м² | 750 мм | 745 мм | 325 мм | 321 мм | 136 мм | 477 мм | 33 | 3 | скрытые защелки |
| ALWT-750х350-Z-АА | 0.158 м² | 750 мм | 745 мм | 350 мм | 346 мм | 136 мм | 477 мм | 35 | 3 | скрытые защелки |
| ALWT-750х400-Z-АА | 0.180 м² | 750 мм | 745 мм | 400 мм | 396 мм | 136 мм | 477 мм | 40 | 3 | скрытые защелки |
| ALWT-750х425-Z-АА | 0.192 м² | 750 мм | 745 мм | 425 мм | 421 мм | 136 мм | 477 мм | 43 | 3 | скрытые защелки |
| ALWT-750х450-Z-АА | 0.203 м² | 750 мм | 745 мм | 450 мм | 446 мм | 136 мм | 477 мм | 45 | 3 | скрытые защелки |
| ALWT-750х500-Z-АА | 0.226 м² | 750 мм | 745 мм | 500 мм | 496 мм | 136 мм | 477 мм | 50 | 3 | скрытые защелки |
| ALWT-750х525-Z-АА | 0.237 м² | 750 мм | 745 мм | 525 мм | 521 мм | 136 мм | 477 мм | 53 | 3 | скрытые защелки |
| ALWT-750х550-Z-АА | 0.248 м² | 750 мм | 745 мм | 550 мм | 546 мм | 136 мм | 477 мм | 55 | 3 | скрытые защелки |
| ALWT-750х600-Z-АА | 0.271 м² | 750 мм | 745 мм | 600 мм | 596 мм | 136 мм | 477 мм | 60 | 3 | скрытые защелки |
| ALWT-750х625-Z-АА | 0.282 м² | 750 мм | 745 мм | 625 мм | 621 мм | 136 мм | 477 мм | 63 | 3 | скрытые защелки |
| ALWT-750х650-Z-АА | 0.293 м² | 750 мм | 745 мм | 650 мм | 646 мм | 136 мм | 477 мм | 65 | 3 | скрытые защелки |
| ALWT-800х100-Z-АА | 0.048 м² | 800 мм | 795 мм | 100 мм | 96 мм | 145 мм | 509 мм | 10 | 4 | скрытые защелки |
| ALWT-800х125-Z-АА | 0.060 м² | 800 мм | 795 мм | 125 мм | 121 мм | 145 мм | 509 мм | 13 | 4 | скрытые защелки |
| ALWT-800х150-Z-АА | 0.072 м² | 800 мм | 795 мм | 150 мм | 146 мм | 145 мм | 509 мм | 15 | 4 | скрытые защелки |
| ALWT-800х200-Z-АА | 0.096 м² | 800 мм | 795 мм | 200 мм | 196 мм | 145 мм | 509 мм | 20 | 4 | скрытые защелки |
| ALWT-800х225-Z-АА | 0.108 м² | 800 мм | 795 мм | 225 мм | 221 мм | 145 мм | 509 мм | 23 | 4 | скрытые защелки |
| ALWT-800х250-Z-АА | 0.120 м² | 800 мм | 795 мм | 250 мм | 246 мм | 145 мм | 509 мм | 25 | 4 | скрытые защелки |
| ALWT-800х300-Z-АА | 0.144 м² | 800 мм | 795 мм | 300 мм | 296 мм | 145 мм | 509 мм | 30 | 4 | скрытые защелки |
| ALWT-800х325-Z-АА | 0.156 м² | 800 мм | 795 мм | 325 мм | 321 мм | 145 мм | 509 мм | 33 | 4 | скрытые защелки |
| ALWT-800х350-Z-АА | 0.168 м² | 800 мм | 795 мм | 350 мм | 346 мм | 145 мм | 509 мм | 35 | 4 | скрытые защелки |
| ALWT-800х400-Z-АА | 0.193 м² | 800 мм | 795 мм | 400 мм | 396 мм | 145 мм | 509 мм | 40 | 4 | скрытые защелки |
| ALWT-800х425-Z-АА | 0.205 м² | 800 мм | 795 мм | 425 мм | 421 мм | 145 мм | 509 мм | 43 | 4 | скрытые защелки |
| ALWT-800х450-Z-АА | 0.217 м² | 800 мм | 795 мм | 450 мм | 446 мм | 145 мм | 509 мм | 45 | 4 | скрытые защелки |
| ALWT-800х500-Z-АА | 0.241 м² | 800 мм | 795 мм | 500 мм | 496 мм | 145 мм | 509 мм | 50 | 4 | скрытые защелки |
| ALWT-800х525-Z-АА | 0.253 м² | 800 мм | 795 мм | 525 мм | 521 мм | 145 мм | 509 мм | 53 | 4 | скрытые защелки |
| ALWT-800х550-Z-АА | 0.265 м² | 800 мм | 795 мм | 550 мм | 546 мм | 145 мм | 509 мм | 55 | 4 | скрытые защелки |
| ALWT-800х600-Z-АА | 0.289 м² | 800 мм | 795 мм | 600 мм | 596 мм | 145 мм | 509 мм | 60 | 4 | скрытые защелки |
| ALWT-800х625-Z-АА | 0.301 м² | 800 мм | 795 мм | 625 мм | 621 мм | 145 мм | 509 мм | 63 | 4 | скрытые защелки |
| ALWT-800х650-Z-АА | 0.313 м² | 800 мм | 795 мм | 650 мм | 646 мм | 145 мм | 509 мм | 65 | 4 | скрытые защелки |
| ALWT-825х100-Z-АА | 0.050 м² | 825 мм | 820 мм | 100 мм | 96 мм | 150 мм | 525 мм | 10 | 4 | скрытые защелки |
| ALWT-825х125-Z-АА | 0.062 м² | 825 мм | 820 мм | 125 мм | 121 мм | 150 мм | 525 мм | 13 | 4 | скрытые защелки |
| ALWT-825х150-Z-АА | 0.074 м² | 825 мм | 820 мм | 150 мм | 146 мм | 150 мм | 525 мм | 15 | 4 | скрытые защелки |
| ALWT-825х200-Z-АА | 0.099 м² | 825 мм | 820 мм | 200 мм | 196 мм | 150 мм | 525 мм | 20 | 4 | скрытые защелки |
| ALWT-825х225-Z-АА | 0.112 м² | 825 мм | 820 мм | 225 мм | 221 мм | 150 мм | 525 мм | 23 | 4 | скрытые защелки |
| ALWT-825х250-Z-АА | 0.124 м² | 825 мм | 820 мм | 250 мм | 246 мм | 150 мм | 525 мм | 25 | 4 | скрытые защелки |
| ALWT-825х300-Z-АА | 0.149 м² | 825 мм | 820 мм | 300 мм | 296 мм | 150 мм | 525 мм | 30 | 4 | скрытые защелки |
| ALWT-825х325-Z-АА | 0.161 м² | 825 мм | 820 мм | 325 мм | 321 мм | 150 мм | 525 мм | 33 | 4 | скрытые защелки |
| ALWT-825х350-Z-АА | 0.174 м² | 825 мм | 820 мм | 350 мм | 346 мм | 150 мм | 525 мм | 35 | 4 | скрытые защелки |
| ALWT-825х400-Z-АА | 0.199 м² | 825 мм | 820 мм | 400 мм | 396 мм | 150 мм | 525 мм | 40 | 4 | скрытые защелки |
| ALWT-825х425-Z-АА | 0.211 м² | 825 мм | 820 мм | 425 мм | 421 мм | 150 мм | 525 мм | 43 | 4 | скрытые защелки |
| ALWT-825х450-Z-АА | 0.223 м² | 825 мм | 820 мм | 450 мм | 446 мм | 150 мм | 525 мм | 45 | 4 | скрытые защелки |
| ALWT-825х500-Z-АА | 0.248 м² | 825 мм | 820 мм | 500 мм | 496 мм | 150 мм | 525 мм | 50 | 4 | скрытые защелки |
| ALWT-825х525-Z-АА | 0.261 м² | 825 мм | 820 мм | 525 мм | 521 мм | 150 мм | 525 мм | 53 | 4 | скрытые защелки |
| ALWT-825х550-Z-АА | 0.273 м² | 825 мм | 820 мм | 550 мм | 546 мм | 150 мм | 525 мм | 55 | 4 | скрытые защелки |
| ALWT-825х600-Z-АА | 0.298 м² | 825 мм | 820 мм | 600 мм | 596 мм | 150 мм | 525 мм | 60 | 4 | скрытые защелки |
| ALWT-825х625-Z-АА | 0.310 м² | 825 мм | 820 мм | 625 мм | 621 мм | 150 мм | 525 мм | 63 | 4 | скрытые защелки |
| ALWT-825х650-Z-АА | 0.323 м² | 825 мм | 820 мм | 650 мм | 646 мм | 150 мм | 525 мм | 65 | 4 | скрытые защелки |
| ALWT-850х100-Z-АА | 0.051 м² | 850 мм | 845 мм | 100 мм | 96 мм | 155 мм | 541 мм | 10 | 4 | скрытые защелки |
| ALWT-850х125-Z-АА | 0.064 м² | 850 мм | 845 мм | 125 мм | 121 мм | 155 мм | 541 мм | 13 | 4 | скрытые защелки |
| ALWT-850х150-Z-АА | 0.077 м² | 850 мм | 845 мм | 150 мм | 146 мм | 155 мм | 541 мм | 15 | 4 | скрытые защелки |
| ALWT-850х200-Z-АА | 0.102 м² | 850 мм | 845 мм | 200 мм | 196 мм | 155 мм | 541 мм | 20 | 4 | скрытые защелки |
| ALWT-850х225-Z-АА | 0.115 м² | 850 мм | 845 мм | 225 мм | 221 мм | 155 мм | 541 мм | 23 | 4 | скрытые защелки |
| ALWT-850х250-Z-АА | 0.128 м² | 850 мм | 845 мм | 250 мм | 246 мм | 155 мм | 541 мм | 25 | 4 | скрытые защелки |
| ALWT-850х300-Z-АА | 0.153 м² | 850 мм | 845 мм | 300 мм | 296 мм | 155 мм | 541 мм | 30 | 4 | скрытые защелки |
| ALWT-850х325-Z-АА | 0.166 м² | 850 мм | 845 мм | 325 мм | 321 мм | 155 мм | 541 мм | 33 | 4 | скрытые защелки |
| ALWT-850х350-Z-АА | 0.179 м² | 850 мм | 845 мм | 350 мм | 346 мм | 155 мм | 541 мм | 35 | 4 | скрытые защелки |
| ALWT-850х400-Z-АА | 0.205 м² | 850 мм | 845 мм | 400 мм | 396 мм | 155 мм | 541 мм | 40 | 4 | скрытые защелки |
| ALWT-850х425-Z-АА | 0.217 м² | 850 мм | 845 мм | 425 мм | 421 мм | 155 мм | 541 мм | 43 | 4 | скрытые защелки |
| ALWT-850х450-Z-АА | 0.230 м² | 850 мм | 845 мм | 450 мм | 446 мм | 155 мм | 541 мм | 45 | 4 | скрытые защелки |
| ALWT-850х500-Z-АА | 0.256 м² | 850 мм | 845 мм | 500 мм | 496 мм | 155 мм | 541 мм | 50 | 4 | скрытые защелки |
| ALWT-850х525-Z-АА | 0.268 м² | 850 мм | 845 мм | 525 мм | 521 мм | 155 мм | 541 мм | 53 | 4 | скрытые защелки |
| ALWT-850х550-Z-АА | 0.281 м² | 850 мм | 845 мм | 550 мм | 546 мм | 155 мм | 541 мм | 55 | 4 | скрытые защелки |
| ALWT-850х600-Z-АА | 0.307 м² | 850 мм | 845 мм | 600 мм | 596 мм | 155 мм | 541 мм | 60 | 4 | скрытые защелки |
| ALWT-850х625-Z-АА | 0.320 м² | 850 мм | 845 мм | 625 мм | 621 мм | 155 мм | 541 мм | 63 | 4 | скрытые защелки |
| ALWT-850х650-Z-АА | 0.332 м² | 850 мм | 845 мм | 650 мм | 646 мм | 155 мм | 541 мм | 65 | 4 | скрытые защелки |
| ALWT-900х100-Z-АА | 0.054 м² | 900 мм | 895 мм | 100 мм | 96 мм | 164 мм | 573 мм | 10 | 4 | скрытые защелки |
| ALWT-900х125-Z-АА | 0.068 м² | 900 мм | 895 мм | 125 мм | 121 мм | 164 мм | 573 мм | 13 | 4 | скрытые защелки |
| ALWT-900х150-Z-АА | 0.081 м² | 900 мм | 895 мм | 150 мм | 146 мм | 164 мм | 573 мм | 15 | 4 | скрытые защелки |
| ALWT-900х200-Z-АА | 0.108 м² | 900 мм | 895 мм | 200 мм | 196 мм | 164 мм | 573 мм | 20 | 4 | скрытые защелки |
| ALWT-900х225-Z-АА | 0.122 м² | 900 мм | 895 мм | 225 мм | 221 мм | 164 мм | 573 мм | 23 | 4 | скрытые защелки |
| ALWT-900х250-Z-АА | 0.135 м² | 900 мм | 895 мм | 250 мм | 246 мм | 164 мм | 573 мм | 25 | 4 | скрытые защелки |
| ALWT-900х300-Z-АА | 0.162 м² | 900 мм | 895 мм | 300 мм | 296 мм | 164 мм | 573 мм | 30 | 4 | скрытые защелки |
| ALWT-900х325-Z-АА | 0.176 м² | 900 мм | 895 мм | 325 мм | 321 мм | 164 мм | 573 мм | 33 | 4 | скрытые защелки |
| ALWT-900х350-Z-АА | 0.190 м² | 900 мм | 895 мм | 350 мм | 346 мм | 164 мм | 573 мм | 35 | 4 | скрытые защелки |
| ALWT-900х400-Z-АА | 0.217 м² | 900 мм | 895 мм | 400 мм | 396 мм | 164 мм | 573 мм | 40 | 4 | скрытые защелки |
| ALWT-900х425-Z-АА | 0.230 м² | 900 мм | 895 мм | 425 мм | 421 мм | 164 мм | 573 мм | 43 | 4 | скрытые защелки |
| ALWT-900х450-Z-АА | 0.244 м² | 900 мм | 895 мм | 450 мм | 446 мм | 164 мм | 573 мм | 45 | 4 | скрытые защелки |
| ALWT-900х500-Z-АА | 0.271 м² | 900 мм | 895 мм | 500 мм | 496 мм | 164 мм | 573 мм | 50 | 4 | скрытые защелки |
| ALWT-900х525-Z-АА | 0.284 м² | 900 мм | 895 мм | 525 мм | 521 мм | 164 мм | 573 мм | 53 | 4 | скрытые защелки |
| ALWT-900х550-Z-АА | 0.298 м² | 900 мм | 895 мм | 550 мм | 546 мм | 164 мм | 573 мм | 55 | 4 | скрытые защелки |
| ALWT-900х600-Z-АА | 0.325 м² | 900 мм | 895 мм | 600 мм | 596 мм | 164 мм | 573 мм | 60 | 4 | скрытые защелки |
| ALWT-900х625-Z-АА | 0.338 м² | 900 мм | 895 мм | 625 мм | 621 мм | 164 мм | 573 мм | 63 | 4 | скрытые защелки |
| ALWT-900х650-Z-АА | 0.352 м² | 900 мм | 895 мм | 650 мм | 646 мм | 164 мм | 573 мм | 65 | 4 | скрытые защелки |
| ALWT-925х100-Z-АА | 0.056 м² | 925 мм | 920 мм | 100 мм | 96 мм | 168 мм | 589 мм | 10 | 4 | скрытые защелки |
| ALWT-925х125-Z-АА | 0.070 м² | 925 мм | 920 мм | 125 мм | 121 мм | 168 мм | 589 мм | 13 | 4 | скрытые защелки |
| ALWT-925х150-Z-АА | 0.083 м² | 925 мм | 920 мм | 150 мм | 146 мм | 168 мм | 589 мм | 15 | 4 | скрытые защелки |
| ALWT-925х200-Z-АА | 0.111 м² | 925 мм | 920 мм | 200 мм | 196 мм | 168 мм | 589 мм | 20 | 4 | скрытые защелки |
| ALWT-925х225-Z-АА | 0.125 м² | 925 мм | 920 мм | 225 мм | 221 мм | 168 мм | 589 мм | 23 | 4 | скрытые защелки |
| ALWT-925х250-Z-АА | 0.139 м² | 925 мм | 920 мм | 250 мм | 246 мм | 168 мм | 589 мм | 25 | 4 | скрытые защелки |
| ALWT-925х300-Z-АА | 0.167 м² | 925 мм | 920 мм | 300 мм | 296 мм | 168 мм | 589 мм | 30 | 4 | скрытые защелки |
| ALWT-925х325-Z-АА | 0.181 м² | 925 мм | 920 мм | 325 мм | 321 мм | 168 мм | 589 мм | 33 | 4 | скрытые защелки |
| ALWT-925х350-Z-АА | 0.195 м² | 925 мм | 920 мм | 350 мм | 346 мм | 168 мм | 589 мм | 35 | 4 | скрытые защелки |
| ALWT-925х400-Z-АА | 0.223 м² | 925 мм | 920 мм | 400 мм | 396 мм | 168 мм | 589 мм | 40 | 4 | скрытые защелки |
| ALWT-925х425-Z-АА | 0.237 м² | 925 мм | 920 мм | 425 мм | 421 мм | 168 мм | 589 мм | 43 | 4 | скрытые защелки |
| ALWT-925х450-Z-АА | 0.250 м² | 925 мм | 920 мм | 450 мм | 446 мм | 168 мм | 589 мм | 45 | 4 | скрытые защелки |
| ALWT-925х500-Z-АА | 0.278 м² | 925 мм | 920 мм | 500 мм | 496 мм | 168 мм | 589 мм | 50 | 4 | скрытые защелки |
| ALWT-925х525-Z-АА | 0.292 м² | 925 мм | 920 мм | 525 мм | 521 мм | 168 мм | 589 мм | 53 | 4 | скрытые защелки |
| ALWT-925х550-Z-АА | 0.306 м² | 925 мм | 920 мм | 550 мм | 546 мм | 168 мм | 589 мм | 55 | 4 | скрытые защелки |
| ALWT-925х600-Z-АА | 0.334 м² | 925 мм | 920 мм | 600 мм | 596 мм | 168 мм | 589 мм | 60 | 4 | скрытые защелки |
| ALWT-925х625-Z-АА | 0.348 м² | 925 мм | 920 мм | 625 мм | 621 мм | 168 мм | 589 мм | 63 | 4 | скрытые защелки |
| ALWT-925х650-Z-АА | 0.362 м² | 925 мм | 920 мм | 650 мм | 646 мм | 168 мм | 589 мм | 65 | 4 | скрытые защелки |
| ALWT-950х100-Z-АА | 0.057 м² | 950 мм | 945 мм | 100 мм | 96 мм | 173 мм | 605 мм | 10 | 4 | скрытые защелки |
| ALWT-950х125-Z-АА | 0.071 м² | 950 мм | 945 мм | 125 мм | 121 мм | 173 мм | 605 мм | 13 | 4 | скрытые защелки |
| ALWT-950х150-Z-АА | 0.086 м² | 950 мм | 945 мм | 150 мм | 146 мм | 173 мм | 605 мм | 15 | 4 | скрытые защелки |
| ALWT-950х200-Z-АА | 0.114 м² | 950 мм | 945 мм | 200 мм | 196 мм | 173 мм | 605 мм | 20 | 4 | скрытые защелки |
| ALWT-950х225-Z-АА | 0.129 м² | 950 мм | 945 мм | 225 мм | 221 мм | 173 мм | 605 мм | 23 | 4 | скрытые защелки |
| ALWT-950х250-Z-АА | 0.143 м² | 950 мм | 945 мм | 250 мм | 246 мм | 173 мм | 605 мм | 25 | 4 | скрытые защелки |
| ALWT-950х300-Z-АА | 0.171 м² | 950 мм | 945 мм | 300 мм | 296 мм | 173 мм | 605 мм | 30 | 4 | скрытые защелки |
| ALWT-950х325-Z-АА | 0.186 м² | 950 мм | 945 мм | 325 мм | 321 мм | 173 мм | 605 мм | 33 | 4 | скрытые защелки |
| ALWT-950х350-Z-АА | 0.200 м² | 950 мм | 945 мм | 350 мм | 346 мм | 173 мм | 605 мм | 35 | 4 | скрытые защелки |
| ALWT-950х400-Z-АА | 0.229 м² | 950 мм | 945 мм | 400 мм | 396 мм | 173 мм | 605 мм | 40 | 4 | скрытые защелки |
| ALWT-950х425-Z-АА | 0.243 м² | 950 мм | 945 мм | 425 мм | 421 мм | 173 мм | 605 мм | 43 | 4 | скрытые защелки |
| ALWT-950х450-Z-АА | 0.257 м² | 950 мм | 945 мм | 450 мм | 446 мм | 173 мм | 605 мм | 45 | 4 | скрытые защелки |
| ALWT-950х500-Z-АА | 0.286 м² | 950 мм | 945 мм | 500 мм | 496 мм | 173 мм | 605 мм | 50 | 4 | скрытые защелки |
| ALWT-950х525-Z-АА | 0.300 м² | 950 мм | 945 мм | 525 мм | 521 мм | 173 мм | 605 мм | 53 | 4 | скрытые защелки |
| ALWT-950х550-Z-АА | 0.314 м² | 950 мм | 945 мм | 550 мм | 546 мм | 173 мм | 605 мм | 55 | 4 | скрытые защелки |
| ALWT-950х600-Z-АА | 0.343 м² | 950 мм | 945 мм | 600 мм | 596 мм | 173 мм | 605 мм | 60 | 4 | скрытые защелки |
| ALWT-950х625-Z-АА | 0.357 м² | 950 мм | 945 мм | 625 мм | 621 мм | 173 мм | 605 мм | 63 | 4 | скрытые защелки |
| ALWT-950х650-Z-АА | 0.371 м² | 950 мм | 945 мм | 650 мм | 646 мм | 173 мм | 605 мм | 65 | 4 | скрытые защелки |
| ALWT-1000х100-Z-АА | 0.060 м² | 1000 мм | 995 мм | 100 мм | 96 мм | 182 мм | 636 мм | 10 | 4 | скрытые защелки |
| ALWT-1000х125-Z-АА | 0.075 м² | 1000 мм | 995 мм | 125 мм | 121 мм | 182 мм | 636 мм | 13 | 4 | скрытые защелки |
| ALWT-1000х150-Z-АА | 0.090 м² | 1000 мм | 995 мм | 150 мм | 146 мм | 182 мм | 636 мм | 15 | 4 | скрытые защелки |
| ALWT-1000х200-Z-АА | 0.120 м² | 1000 мм | 995 мм | 200 мм | 196 мм | 182 мм | 636 мм | 20 | 4 | скрытые защелки |
| ALWT-1000х225-Z-АА | 0.135 м² | 1000 мм | 995 мм | 225 мм | 221 мм | 182 мм | 636 мм | 23 | 4 | скрытые защелки |
| ALWT-1000х250-Z-АА | 0.150 м² | 1000 мм | 995 мм | 250 мм | 246 мм | 182 мм | 636 мм | 25 | 4 | скрытые защелки |
| ALWT-1000х300-Z-АА | 0.180 м² | 1000 мм | 995 мм | 300 мм | 296 мм | 182 мм | 636 мм | 30 | 4 | скрытые защелки |
| ALWT-1000х325-Z-АА | 0.196 м² | 1000 мм | 995 мм | 325 мм | 321 мм | 182 мм | 636 мм | 33 | 4 | скрытые защелки |
| ALWT-1000х350-Z-АА | 0.211 м² | 1000 мм | 995 мм | 350 мм | 346 мм | 182 мм | 636 мм | 35 | 4 | скрытые защелки |
| ALWT-1000х400-Z-АА | 0.241 м² | 1000 мм | 995 мм | 400 мм | 396 мм | 182 мм | 636 мм | 40 | 4 | скрытые защелки |
| ALWT-1000х425-Z-АА | 0.256 м² | 1000 мм | 995 мм | 425 мм | 421 мм | 182 мм | 636 мм | 43 | 4 | скрытые защелки |
| ALWT-1000х450-Z-АА | 0.271 м² | 1000 мм | 995 мм | 450 мм | 446 мм | 182 мм | 636 мм | 45 | 4 | скрытые защелки |
| ALWT-1000х500-Z-АА | 0.301 м² | 1000 мм | 995 мм | 500 мм | 496 мм | 182 мм | 636 мм | 50 | 4 | скрытые защелки |
| ALWT-1000х525-Z-АА | 0.316 м² | 1000 мм | 995 мм | 525 мм | 521 мм | 182 мм | 636 мм | 53 | 4 | скрытые защелки |
| ALWT-1000х550-Z-АА | 0.331 м² | 1000 мм | 995 мм | 550 мм | 546 мм | 182 мм | 636 мм | 55 | 4 | скрытые защелки |
| ALWT-1000х600-Z-АА | 0.361 м² | 1000 мм | 995 мм | 600 мм | 596 мм | 182 мм | 636 мм | 60 | 4 | скрытые защелки |
| ALWT-1000х625-Z-АА | 0.376 м² | 1000 мм | 995 мм | 625 мм | 621 мм | 182 мм | 636 мм | 63 | 4 | скрытые защелки |
| ALWT-1000х650-Z-АА | 0.391 м² | 1000 мм | 995 мм | 650 мм | 646 мм | 182 мм | 636 мм | 65 | 4 | скрытые защелки |
| ALWT-1025х100-Z-АА | 0.062 м² | 1025 мм | 1020 мм | 100 мм | 96 мм | 186 мм | 652 мм | 10 | 4 | скрытые защелки |
| ALWT-1025х125-Z-АА | 0.077 м² | 1025 мм | 1020 мм | 125 мм | 121 мм | 186 мм | 652 мм | 13 | 4 | скрытые защелки |
| ALWT-1025х150-Z-АА | 0.092 м² | 1025 мм | 1020 мм | 150 мм | 146 мм | 186 мм | 652 мм | 15 | 4 | скрытые защелки |
| ALWT-1025х200-Z-АА | 0.123 м² | 1025 мм | 1020 мм | 200 мм | 196 мм | 186 мм | 652 мм | 20 | 4 | скрытые защелки |
| ALWT-1025х225-Z-АА | 0.139 м² | 1025 мм | 1020 мм | 225 мм | 221 мм | 186 мм | 652 мм | 23 | 4 | скрытые защелки |
| ALWT-1025х250-Z-АА | 0.154 м² | 1025 мм | 1020 мм | 250 мм | 246 мм | 186 мм | 652 мм | 25 | 4 | скрытые защелки |
| ALWT-1025х300-Z-АА | 0.185 м² | 1025 мм | 1020 мм | 300 мм | 296 мм | 186 мм | 652 мм | 30 | 4 | скрытые защелки |
| ALWT-1025х325-Z-АА | 0.200 м² | 1025 мм | 1020 мм | 325 мм | 321 мм | 186 мм | 652 мм | 33 | 4 | скрытые защелки |
| ALWT-1025х350-Z-АА | 0.216 м² | 1025 мм | 1020 мм | 350 мм | 346 мм | 186 мм | 652 мм | 35 | 4 | скрытые защелки |
| ALWT-1025х400-Z-АА | 0.247 м² | 1025 мм | 1020 мм | 400 мм | 396 мм | 186 мм | 652 мм | 40 | 4 | скрытые защелки |
| ALWT-1025х425-Z-АА | 0.262 м² | 1025 мм | 1020 мм | 425 мм | 421 мм | 186 мм | 652 мм | 43 | 4 | скрытые защелки |
| ALWT-1025х450-Z-АА | 0.277 м² | 1025 мм | 1020 мм | 450 мм | 446 мм | 186 мм | 652 мм | 45 | 4 | скрытые защелки |
| ALWT-1025х500-Z-АА | 0.308 м² | 1025 мм | 1020 мм | 500 мм | 496 мм | 186 мм | 652 мм | 50 | 4 | скрытые защелки |
| ALWT-1025х525-Z-АА | 0.324 м² | 1025 мм | 1020 мм | 525 мм | 521 мм | 186 мм | 652 мм | 53 | 4 | скрытые защелки |
| ALWT-1025х550-Z-АА | 0.339 м² | 1025 мм | 1020 мм | 550 мм | 546 мм | 186 мм | 652 мм | 55 | 4 | скрытые защелки |
| ALWT-1025х600-Z-АА | 0.370 м² | 1025 мм | 1020 мм | 600 мм | 596 мм | 186 мм | 652 мм | 60 | 4 | скрытые защелки |
| ALWT-1025х625-Z-АА | 0.385 м² | 1025 мм | 1020 мм | 625 мм | 621 мм | 186 мм | 652 мм | 63 | 4 | скрытые защелки |
| ALWT-1025х650-Z-АА | 0.401 м² | 1025 мм | 1020 мм | 650 мм | 646 мм | 186 мм | 652 мм | 65 | 4 | скрытые защелки |
| ALWT-1050х100-Z-АА | 0.063 м² | 1050 мм | 1045 мм | 100 мм | 96 мм | 191 мм | 668 мм | 10 | 4 | скрытые защелки |
| ALWT-1050х125-Z-АА | 0.079 м² | 1050 мм | 1045 мм | 125 мм | 121 мм | 191 мм | 668 мм | 13 | 4 | скрытые защелки |
| ALWT-1050х150-Z-АА | 0.095 м² | 1050 мм | 1045 мм | 150 мм | 146 мм | 191 мм | 668 мм | 15 | 4 | скрытые защелки |
| ALWT-1050х200-Z-АА | 0.126 м² | 1050 мм | 1045 мм | 200 мм | 196 мм | 191 мм | 668 мм | 20 | 4 | скрытые защелки |
| ALWT-1050х225-Z-АА | 0.142 м² | 1050 мм | 1045 мм | 225 мм | 221 мм | 191 мм | 668 мм | 23 | 4 | скрытые защелки |
| ALWT-1050х250-Z-АА | 0.158 м² | 1050 мм | 1045 мм | 250 мм | 246 мм | 191 мм | 668 мм | 25 | 4 | скрытые защелки |
| ALWT-1050х300-Z-АА | 0.190 м² | 1050 мм | 1045 мм | 300 мм | 296 мм | 191 мм | 668 мм | 30 | 4 | скрытые защелки |
| ALWT-1050х325-Z-АА | 0.205 м² | 1050 мм | 1045 мм | 325 мм | 321 мм | 191 мм | 668 мм | 33 | 4 | скрытые защелки |
| ALWT-1050х350-Z-АА | 0.221 м² | 1050 мм | 1045 мм | 350 мм | 346 мм | 191 мм | 668 мм | 35 | 4 | скрытые защелки |
| ALWT-1050х400-Z-АА | 0.253 м² | 1050 мм | 1045 мм | 400 мм | 396 мм | 191 мм | 668 мм | 40 | 4 | скрытые защелки |
| ALWT-1050х425-Z-АА | 0.268 м² | 1050 мм | 1045 мм | 425 мм | 421 мм | 191 мм | 668 мм | 43 | 4 | скрытые защелки |
| ALWT-1050х450-Z-АА | 0.284 м² | 1050 мм | 1045 мм | 450 мм | 446 мм | 191 мм | 668 мм | 45 | 4 | скрытые защелки |
| ALWT-1050х500-Z-АА | 0.316 м² | 1050 мм | 1045 мм | 500 мм | 496 мм | 191 мм | 668 мм | 50 | 4 | скрытые защелки |
| ALWT-1050х525-Z-АА | 0.332 м² | 1050 мм | 1045 мм | 525 мм | 521 мм | 191 мм | 668 мм | 53 | 4 | скрытые защелки |
| ALWT-1050х550-Z-АА | 0.347 м² | 1050 мм | 1045 мм | 550 мм | 546 мм | 191 мм | 668 мм | 55 | 4 | скрытые защелки |
| ALWT-1050х600-Z-АА | 0.379 м² | 1050 мм | 1045 мм | 600 мм | 596 мм | 191 мм | 668 мм | 60 | 4 | скрытые защелки |
| ALWT-1050х625-Z-АА | 0.395 м² | 1050 мм | 1045 мм | 625 мм | 621 мм | 191 мм | 668 мм | 63 | 4 | скрытые защелки |
| ALWT-1050х650-Z-АА | 0.411 м² | 1050 мм | 1045 мм | 650 мм | 646 мм | 191 мм | 668 мм | 65 | 4 | скрытые защелки |
| ALWT-1100х100-Z-АА | 0.066 м² | 1100 мм | 1095 мм | 100 мм | 96 мм | 200 мм | 700 мм | 10 | 4 | скрытые защелки |
| ALWT-1100х125-Z-АА | 0.083 м² | 1100 мм | 1095 мм | 125 мм | 121 мм | 200 мм | 700 мм | 13 | 4 | скрытые защелки |
| ALWT-1100х150-Z-АА | 0.099 м² | 1100 мм | 1095 мм | 150 мм | 146 мм | 200 мм | 700 мм | 15 | 4 | скрытые защелки |
| ALWT-1100х200-Z-АА | 0.132 м² | 1100 мм | 1095 мм | 200 мм | 196 мм | 200 мм | 700 мм | 20 | 4 | скрытые защелки |
| ALWT-1100х225-Z-АА | 0.149 м² | 1100 мм | 1095 мм | 225 мм | 221 мм | 200 мм | 700 мм | 23 | 4 | скрытые защелки |
| ALWT-1100х250-Z-АА | 0.165 м² | 1100 мм | 1095 мм | 250 мм | 246 мм | 200 мм | 700 мм | 25 | 4 | скрытые защелки |
| ALWT-1100х300-Z-АА | 0.199 м² | 1100 мм | 1095 мм | 300 мм | 296 мм | 200 мм | 700 мм | 30 | 4 | скрытые защелки |
| ALWT-1100х325-Z-АА | 0.215 м² | 1100 мм | 1095 мм | 325 мм | 321 мм | 200 мм | 700 мм | 33 | 4 | скрытые защелки |
| ALWT-1100х350-Z-АА | 0.232 м² | 1100 мм | 1095 мм | 350 мм | 346 мм | 200 мм | 700 мм | 35 | 4 | скрытые защелки |
| ALWT-1100х400-Z-АА | 0.265 м² | 1100 мм | 1095 мм | 400 мм | 396 мм | 200 мм | 700 мм | 40 | 4 | скрытые защелки |
| ALWT-1100х425-Z-АА | 0.281 м² | 1100 мм | 1095 мм | 425 мм | 421 мм | 200 мм | 700 мм | 43 | 4 | скрытые защелки |
| ALWT-1100х450-Z-АА | 0.298 м² | 1100 мм | 1095 мм | 450 мм | 446 мм | 200 мм | 700 мм | 45 | 4 | скрытые защелки |
| ALWT-1100х500-Z-АА | 0.331 м² | 1100 мм | 1095 мм | 500 мм | 496 мм | 200 мм | 700 мм | 50 | 4 | скрытые защелки |
| ALWT-1100х525-Z-АА | 0.347 м² | 1100 мм | 1095 мм | 525 мм | 521 мм | 200 мм | 700 мм | 53 | 4 | скрытые защелки |
| ALWT-1100х550-Z-АА | 0.364 м² | 1100 мм | 1095 мм | 550 мм | 546 мм | 200 мм | 700 мм | 55 | 4 | скрытые защелки |
| ALWT-1100х600-Z-АА | 0.397 м² | 1100 мм | 1095 мм | 600 мм | 596 мм | 200 мм | 700 мм | 60 | 4 | скрытые защелки |
| ALWT-1100х625-Z-АА | 0.414 м² | 1100 мм | 1095 мм | 625 мм | 621 мм | 200 мм | 700 мм | 63 | 4 | скрытые защелки |
| ALWT-1100х650-Z-АА | 0.430 м² | 1100 мм | 1095 мм | 650 мм | 646 мм | 200 мм | 700 мм | 65 | 4 | скрытые защелки |
| ALWT-1125х100-Z-АА | 0.068 м² | 1125 мм | 1120 мм | 100 мм | 96 мм | 205 мм | 716 мм | 10 | 4 | скрытые защелки |
| ALWT-1125х125-Z-АА | 0.085 м² | 1125 мм | 1120 мм | 125 мм | 121 мм | 205 мм | 716 мм | 13 | 4 | скрытые защелки |
| ALWT-1125х150-Z-АА | 0.102 м² | 1125 мм | 1120 мм | 150 мм | 146 мм | 205 мм | 716 мм | 15 | 4 | скрытые защелки |
| ALWT-1125х200-Z-АА | 0.135 м² | 1125 мм | 1120 мм | 200 мм | 196 мм | 205 мм | 716 мм | 20 | 4 | скрытые защелки |
| ALWT-1125х225-Z-АА | 0.152 м² | 1125 мм | 1120 мм | 225 мм | 221 мм | 205 мм | 716 мм | 23 | 4 | скрытые защелки |
| ALWT-1125х250-Z-АА | 0.169 м² | 1125 мм | 1120 мм | 250 мм | 246 мм | 205 мм | 716 мм | 25 | 4 | скрытые защелки |
| ALWT-1125х300-Z-АА | 0.203 м² | 1125 мм | 1120 мм | 300 мм | 296 мм | 205 мм | 716 мм | 30 | 4 | скрытые защелки |
| ALWT-1125х325-Z-АА | 0.220 м² | 1125 мм | 1120 мм | 325 мм | 321 мм | 205 мм | 716 мм | 33 | 4 | скрытые защелки |
| ALWT-1125х350-Z-АА | 0.237 м² | 1125 мм | 1120 мм | 350 мм | 346 мм | 205 мм | 716 мм | 35 | 4 | скрытые защелки |
| ALWT-1125х400-Z-АА | 0.271 м² | 1125 мм | 1120 мм | 400 мм | 396 мм | 205 мм | 716 мм | 40 | 4 | скрытые защелки |
| ALWT-1125х425-Z-АА | 0.288 м² | 1125 мм | 1120 мм | 425 мм | 421 мм | 205 мм | 716 мм | 43 | 4 | скрытые защелки |
| ALWT-1125х450-Z-АА | 0.305 м² | 1125 мм | 1120 мм | 450 мм | 446 мм | 205 мм | 716 мм | 45 | 4 | скрытые защелки |
| ALWT-1125х500-Z-АА | 0.338 м² | 1125 мм | 1120 мм | 500 мм | 496 мм | 205 мм | 716 мм | 50 | 4 | скрытые защелки |
| ALWT-1125х525-Z-АА | 0.355 м² | 1125 мм | 1120 мм | 525 мм | 521 мм | 205 мм | 716 мм | 53 | 4 | скрытые защелки |
| ALWT-1125х550-Z-АА | 0.372 м² | 1125 мм | 1120 мм | 550 мм | 546 мм | 205 мм | 716 мм | 55 | 4 | скрытые защелки |
| ALWT-1125х600-Z-АА | 0.406 м² | 1125 мм | 1120 мм | 600 мм | 596 мм | 205 мм | 716 мм | 60 | 4 | скрытые защелки |
| ALWT-1125х625-Z-АА | 0.423 м² | 1125 мм | 1120 мм | 625 мм | 621 мм | 205 мм | 716 мм | 63 | 4 | скрытые защелки |
| ALWT-1125х650-Z-АА | 0.440 м² | 1125 мм | 1120 мм | 650 мм | 646 мм | 205 мм | 716 мм | 65 | 4 | скрытые защелки |
| ALWT-1150х100-Z-АА | 0.069 м² | 1150 мм | 1145 мм | 100 мм | 96 мм | 209 мм | 732 мм | 10 | 4 | скрытые защелки |
| ALWT-1150х125-Z-АА | 0.086 м² | 1150 мм | 1145 мм | 125 мм | 121 мм | 209 мм | 732 мм | 13 | 4 | скрытые защелки |
| ALWT-1150х150-Z-АА | 0.104 м² | 1150 мм | 1145 мм | 150 мм | 146 мм | 209 мм | 732 мм | 15 | 4 | скрытые защелки |
| ALWT-1150х200-Z-АА | 0.138 м² | 1150 мм | 1145 мм | 200 мм | 196 мм | 209 мм | 732 мм | 20 | 4 | скрытые защелки |
| ALWT-1150х225-Z-АА | 0.156 м² | 1150 мм | 1145 мм | 225 мм | 221 мм | 209 мм | 732 мм | 23 | 4 | скрытые защелки |
| ALWT-1150х250-Z-АА | 0.173 м² | 1150 мм | 1145 мм | 250 мм | 246 мм | 209 мм | 732 мм | 25 | 4 | скрытые защелки |
| ALWT-1150х300-Z-АА | 0.208 м² | 1150 мм | 1145 мм | 300 мм | 296 мм | 209 мм | 732 мм | 30 | 4 | скрытые защелки |
| ALWT-1150х325-Z-АА | 0.225 м² | 1150 мм | 1145 мм | 325 мм | 321 мм | 209 мм | 732 мм | 33 | 4 | скрытые защелки |
| ALWT-1150х350-Z-АА | 0.242 м² | 1150 мм | 1145 мм | 350 мм | 346 мм | 209 мм | 732 мм | 35 | 4 | скрытые защелки |
| ALWT-1150х400-Z-АА | 0.277 м² | 1150 мм | 1145 мм | 400 мм | 396 мм | 209 мм | 732 мм | 40 | 4 | скрытые защелки |
| ALWT-1150х425-Z-АА | 0.294 м² | 1150 мм | 1145 мм | 425 мм | 421 мм | 209 мм | 732 мм | 43 | 4 | скрытые защелки |
| ALWT-1150х450-Z-АА | 0.311 м² | 1150 мм | 1145 мм | 450 мм | 446 мм | 209 мм | 732 мм | 45 | 4 | скрытые защелки |
| ALWT-1150х500-Z-АА | 0.346 м² | 1150 мм | 1145 мм | 500 мм | 496 мм | 209 мм | 732 мм | 50 | 4 | скрытые защелки |
| ALWT-1150х525-Z-АА | 0.363 м² | 1150 мм | 1145 мм | 525 мм | 521 мм | 209 мм | 732 мм | 53 | 4 | скрытые защелки |
| ALWT-1150х550-Z-АА | 0.381 м² | 1150 мм | 1145 мм | 550 мм | 546 мм | 209 мм | 732 мм | 55 | 4 | скрытые защелки |
| ALWT-1150х600-Z-АА | 0.415 м² | 1150 мм | 1145 мм | 600 мм | 596 мм | 209 мм | 732 мм | 60 | 4 | скрытые защелки |
| ALWT-1150х625-Z-АА | 0.432 м² | 1150 мм | 1145 мм | 625 мм | 621 мм | 209 мм | 732 мм | 63 | 4 | скрытые защелки |
| ALWT-1150х650-Z-АА | 0.450 м² | 1150 мм | 1145 мм | 650 мм | 646 мм | 209 мм | 732 мм | 65 | 4 | скрытые защелки |
| ALWT-1200х100-Z-АА | 0.072 м² | 1200 мм | 1195 мм | 100 мм | 96 мм | 218 мм | 764 мм | 10 | 4 | скрытые защелки |
| ALWT-1200х125-Z-АА | 0.090 м² | 1200 мм | 1195 мм | 125 мм | 121 мм | 218 мм | 764 мм | 13 | 4 | скрытые защелки |
| ALWT-1200х150-Z-АА | 0.108 м² | 1200 мм | 1195 мм | 150 мм | 146 мм | 218 мм | 764 мм | 15 | 4 | скрытые защелки |
| ALWT-1200х200-Z-АА | 0.144 м² | 1200 мм | 1195 мм | 200 мм | 196 мм | 218 мм | 764 мм | 20 | 4 | скрытые защелки |
| ALWT-1200х225-Z-АА | 0.162 м² | 1200 мм | 1195 мм | 225 мм | 221 мм | 218 мм | 764 мм | 23 | 4 | скрытые защелки |
| ALWT-1200х250-Z-АА | 0.180 м² | 1200 мм | 1195 мм | 250 мм | 246 мм | 218 мм | 764 мм | 25 | 4 | скрытые защелки |
| ALWT-1200х300-Z-АА | 0.217 м² | 1200 мм | 1195 мм | 300 мм | 296 мм | 218 мм | 764 мм | 30 | 4 | скрытые защелки |
| ALWT-1200х325-Z-АА | 0.235 м² | 1200 мм | 1195 мм | 325 мм | 321 мм | 218 мм | 764 мм | 33 | 4 | скрытые защелки |
| ALWT-1200х350-Z-АА | 0.253 м² | 1200 мм | 1195 мм | 350 мм | 346 мм | 218 мм | 764 мм | 35 | 4 | скрытые защелки |
| ALWT-1200х400-Z-АА | 0.289 м² | 1200 мм | 1195 мм | 400 мм | 396 мм | 218 мм | 764 мм | 40 | 4 | скрытые защелки |
| ALWT-1200х425-Z-АА | 0.307 м² | 1200 мм | 1195 мм | 425 мм | 421 мм | 218 мм | 764 мм | 43 | 4 | скрытые защелки |
| ALWT-1200х450-Z-АА | 0.325 м² | 1200 мм | 1195 мм | 450 мм | 446 мм | 218 мм | 764 мм | 45 | 4 | скрытые защелки |
| ALWT-1200х500-Z-АА | 0.361 м² | 1200 мм | 1195 мм | 500 мм | 496 мм | 218 мм | 764 мм | 50 | 4 | скрытые защелки |
| ALWT-1200х525-Z-АА | 0.379 м² | 1200 мм | 1195 мм | 525 мм | 521 мм | 218 мм | 764 мм | 53 | 4 | скрытые защелки |
| ALWT-1200х550-Z-АА | 0.397 м² | 1200 мм | 1195 мм | 550 мм | 546 мм | 218 мм | 764 мм | 55 | 4 | скрытые защелки |
| ALWT-1200х600-Z-АА | 0.433 м² | 1200 мм | 1195 мм | 600 мм | 596 мм | 218 мм | 764 мм | 60 | 4 | скрытые защелки |
| ALWT-1200х625-Z-АА | 0.451 м² | 1200 мм | 1195 мм | 625 мм | 621 мм | 218 мм | 764 мм | 63 | 4 | скрытые защелки |
| ALWT-1200х650-Z-АА | 0.469 м² | 1200 мм | 1195 мм | 650 мм | 646 мм | 218 мм | 764 мм | 65 | 4 | скрытые защелки |
| ALWT-1225х100-Z-АА | 0.074 м² | 1225 мм | 1220 мм | 100 мм | 96 мм | 223 мм | 780 мм | 10 | 4 | скрытые защелки |
| ALWT-1225х125-Z-АА | 0.092 м² | 1225 мм | 1220 мм | 125 мм | 121 мм | 223 мм | 780 мм | 13 | 4 | скрытые защелки |
| ALWT-1225х150-Z-АА | 0.111 м² | 1225 мм | 1220 мм | 150 мм | 146 мм | 223 мм | 780 мм | 15 | 4 | скрытые защелки |
| ALWT-1225х200-Z-АА | 0.147 м² | 1225 мм | 1220 мм | 200 мм | 196 мм | 223 мм | 780 мм | 20 | 4 | скрытые защелки |
| ALWT-1225х225-Z-АА | 0.166 м² | 1225 мм | 1220 мм | 225 мм | 221 мм | 223 мм | 780 мм | 23 | 4 | скрытые защелки |
| ALWT-1225х250-Z-АА | 0.184 м² | 1225 мм | 1220 мм | 250 мм | 246 мм | 223 мм | 780 мм | 25 | 4 | скрытые защелки |
| ALWT-1225х300-Z-АА | 0.221 м² | 1225 мм | 1220 мм | 300 мм | 296 мм | 223 мм | 780 мм | 30 | 4 | скрытые защелки |
| ALWT-1225х325-Z-АА | 0.240 м² | 1225 мм | 1220 мм | 325 мм | 321 мм | 223 мм | 780 мм | 33 | 4 | скрытые защелки |
| ALWT-1225х350-Z-АА | 0.258 м² | 1225 мм | 1220 мм | 350 мм | 346 мм | 223 мм | 780 мм | 35 | 4 | скрытые защелки |
| ALWT-1225х400-Z-АА | 0.295 м² | 1225 мм | 1220 мм | 400 мм | 396 мм | 223 мм | 780 мм | 40 | 4 | скрытые защелки |
| ALWT-1225х425-Z-АА | 0.313 м² | 1225 мм | 1220 мм | 425 мм | 421 мм | 223 мм | 780 мм | 43 | 4 | скрытые защелки |
| ALWT-1225х450-Z-АА | 0.332 м² | 1225 мм | 1220 мм | 450 мм | 446 мм | 223 мм | 780 мм | 45 | 4 | скрытые защелки |
| ALWT-1225х500-Z-АА | 0.368 м² | 1225 мм | 1220 мм | 500 мм | 496 мм | 223 мм | 780 мм | 50 | 4 | скрытые защелки |
| ALWT-1225х525-Z-АА | 0.387 м² | 1225 мм | 1220 мм | 525 мм | 521 мм | 223 мм | 780 мм | 53 | 4 | скрытые защелки |
| ALWT-1225х550-Z-АА | 0.405 м² | 1225 мм | 1220 мм | 550 мм | 546 мм | 223 мм | 780 мм | 55 | 4 | скрытые защелки |
| ALWT-1225х600-Z-АА | 0.442 м² | 1225 мм | 1220 мм | 600 мм | 596 мм | 223 мм | 780 мм | 60 | 4 | скрытые защелки |
| ALWT-1225х625-Z-АА | 0.461 м² | 1225 мм | 1220 мм | 625 мм | 621 мм | 223 мм | 780 мм | 63 | 4 | скрытые защелки |
| ALWT-1225х650-Z-АА | 0.479 м² | 1225 мм | 1220 мм | 650 мм | 646 мм | 223 мм | 780 мм | 65 | 4 | скрытые защелки |
| ALWT-1250х100-Z-АА | 0.075 м² | 1250 мм | 1245 мм | 100 мм | 96 мм | 227 мм | 795 мм | 10 | 4 | скрытые защелки |
| ALWT-1250х125-Z-АА | 0.094 м² | 1250 мм | 1245 мм | 125 мм | 121 мм | 227 мм | 795 мм | 13 | 4 | скрытые защелки |
| ALWT-1250х150-Z-АА | 0.113 м² | 1250 мм | 1245 мм | 150 мм | 146 мм | 227 мм | 795 мм | 15 | 4 | скрытые защелки |
| ALWT-1250х200-Z-АА | 0.150 м² | 1250 мм | 1245 мм | 200 мм | 196 мм | 227 мм | 795 мм | 20 | 4 | скрытые защелки |
| ALWT-1250х225-Z-АА | 0.169 м² | 1250 мм | 1245 мм | 225 мм | 221 мм | 227 мм | 795 мм | 23 | 4 | скрытые защелки |
| ALWT-1250х250-Z-АА | 0.188 м² | 1250 мм | 1245 мм | 250 мм | 246 мм | 227 мм | 795 мм | 25 | 4 | скрытые защелки |
| ALWT-1250х300-Z-АА | 0.226 м² | 1250 мм | 1245 мм | 300 мм | 296 мм | 227 мм | 795 мм | 30 | 4 | скрытые защелки |
| ALWT-1250х325-Z-АА | 0.244 м² | 1250 мм | 1245 мм | 325 мм | 321 мм | 227 мм | 795 мм | 33 | 4 | скрытые защелки |
| ALWT-1250х350-Z-АА | 0.263 м² | 1250 мм | 1245 мм | 350 мм | 346 мм | 227 мм | 795 мм | 35 | 4 | скрытые защелки |
| ALWT-1250х400-Z-АА | 0.301 м² | 1250 мм | 1245 мм | 400 мм | 396 мм | 227 мм | 795 мм | 40 | 4 | скрытые защелки |
| ALWT-1250х425-Z-АА | 0.320 м² | 1250 мм | 1245 мм | 425 мм | 421 мм | 227 мм | 795 мм | 43 | 4 | скрытые защелки |
| ALWT-1250х450-Z-АА | 0.338 м² | 1250 мм | 1245 мм | 450 мм | 446 мм | 227 мм | 795 мм | 45 | 4 | скрытые защелки |
| ALWT-1250х500-Z-АА | 0.376 м² | 1250 мм | 1245 мм | 500 мм | 496 мм | 227 мм | 795 мм | 50 | 4 | скрытые защелки |
| ALWT-1250х525-Z-АА | 0.395 м² | 1250 мм | 1245 мм | 525 мм | 521 мм | 227 мм | 795 мм | 53 | 4 | скрытые защелки |
| ALWT-1250х550-Z-АА | 0.414 м² | 1250 мм | 1245 мм | 550 мм | 546 мм | 227 мм | 795 мм | 55 | 4 | скрытые защелки |
| ALWT-1250х600-Z-АА | 0.451 м² | 1250 мм | 1245 мм | 600 мм | 596 мм | 227 мм | 795 мм | 60 | 4 | скрытые защелки |
| ALWT-1250х625-Z-АА | 0.470 м² | 1250 мм | 1245 мм | 625 мм | 621 мм | 227 мм | 795 мм | 63 | 4 | скрытые защелки |
| ALWT-1250х650-Z-АА | 0.489 м² | 1250 мм | 1245 мм | 650 мм | 646 мм | 227 мм | 795 мм | 65 | 4 | скрытые защелки |
| ALWT-1300х100-Z-АА | 0.078 м² | 1300 мм | 1295 мм | 100 мм | 96 мм | 236 мм | 827 мм | 10 | 4 | скрытые защелки |
| ALWT-1300х125-Z-АА | 0.098 м² | 1300 мм | 1295 мм | 125 мм | 121 мм | 236 мм | 827 мм | 13 | 4 | скрытые защелки |
| ALWT-1300х150-Z-АА | 0.117 м² | 1300 мм | 1295 мм | 150 мм | 146 мм | 236 мм | 827 мм | 15 | 4 | скрытые защелки |
| ALWT-1300х200-Z-АА | 0.156 м² | 1300 мм | 1295 мм | 200 мм | 196 мм | 236 мм | 827 мм | 20 | 4 | скрытые защелки |
| ALWT-1300х225-Z-АА | 0.176 м² | 1300 мм | 1295 мм | 225 мм | 221 мм | 236 мм | 827 мм | 23 | 4 | скрытые защелки |
| ALWT-1300х250-Z-АА | 0.196 м² | 1300 мм | 1295 мм | 250 мм | 246 мм | 236 мм | 827 мм | 25 | 4 | скрытые защелки |
| ALWT-1300х300-Z-АА | 0.235 м² | 1300 мм | 1295 мм | 300 мм | 296 мм | 236 мм | 827 мм | 30 | 4 | скрытые защелки |
| ALWT-1300х325-Z-АА | 0.254 м² | 1300 мм | 1295 мм | 325 мм | 321 мм | 236 мм | 827 мм | 33 | 4 | скрытые защелки |
| ALWT-1300х350-Z-АА | 0.274 м² | 1300 мм | 1295 мм | 350 мм | 346 мм | 236 мм | 827 мм | 35 | 4 | скрытые защелки |
| ALWT-1300х400-Z-АА | 0.313 м² | 1300 мм | 1295 мм | 400 мм | 396 мм | 236 мм | 827 мм | 40 | 4 | скрытые защелки |
| ALWT-1300х425-Z-АА | 0.332 м² | 1300 мм | 1295 мм | 425 мм | 421 мм | 236 мм | 827 мм | 43 | 4 | скрытые защелки |
| ALWT-1300х450-Z-АА | 0.352 м² | 1300 мм | 1295 мм | 450 мм | 446 мм | 236 мм | 827 мм | 45 | 4 | скрытые защелки |
| ALWT-1300х500-Z-АА | 0.391 м² | 1300 мм | 1295 мм | 500 мм | 496 мм | 236 мм | 827 мм | 50 | 4 | скрытые защелки |
| ALWT-1300х525-Z-АА | 0.411 м² | 1300 мм | 1295 мм | 525 мм | 521 мм | 236 мм | 827 мм | 53 | 4 | скрытые защелки |
| ALWT-1300х550-Z-АА | 0.430 м² | 1300 мм | 1295 мм | 550 мм | 546 мм | 236 мм | 827 мм | 55 | 4 | скрытые защелки |
| ALWT-1300х600-Z-АА | 0.469 м² | 1300 мм | 1295 мм | 600 мм | 596 мм | 236 мм | 827 мм | 60 | 4 | скрытые защелки |
| ALWT-1300х625-Z-АА | 0.489 м² | 1300 мм | 1295 мм | 625 мм | 621 мм | 236 мм | 827 мм | 63 | 4 | скрытые защелки |
| ALWT-1300х650-Z-АА | 0.508 м² | 1300 мм | 1295 мм | 650 мм | 646 мм | 236 мм | 827 мм | 65 | 4 | скрытые защелки |
| ALWT-1325х100-Z-АА | 0.080 м² | 1325 мм | 1320 мм | 100 мм | 96 мм | 241 мм | 843 мм | 10 | 4 | скрытые защелки |
| ALWT-1325х125-Z-АА | 0.100 м² | 1325 мм | 1320 мм | 125 мм | 121 мм | 241 мм | 843 мм | 13 | 4 | скрытые защелки |
| ALWT-1325х150-Z-АА | 0.120 м² | 1325 мм | 1320 мм | 150 мм | 146 мм | 241 мм | 843 мм | 15 | 4 | скрытые защелки |
| ALWT-1325х200-Z-АА | 0.159 м² | 1325 мм | 1320 мм | 200 мм | 196 мм | 241 мм | 843 мм | 20 | 4 | скрытые защелки |
| ALWT-1325х225-Z-АА | 0.179 м² | 1325 мм | 1320 мм | 225 мм | 221 мм | 241 мм | 843 мм | 23 | 4 | скрытые защелки |
| ALWT-1325х250-Z-АА | 0.199 м² | 1325 мм | 1320 мм | 250 мм | 246 мм | 241 мм | 843 мм | 25 | 4 | скрытые защелки |
| ALWT-1325х300-Z-АА | 0.239 м² | 1325 мм | 1320 мм | 300 мм | 296 мм | 241 мм | 843 мм | 30 | 4 | скрытые защелки |
| ALWT-1325х325-Z-АА | 0.259 м² | 1325 мм | 1320 мм | 325 мм | 321 мм | 241 мм | 843 мм | 33 | 4 | скрытые защелки |
| ALWT-1325х350-Z-АА | 0.279 м² | 1325 мм | 1320 мм | 350 мм | 346 мм | 241 мм | 843 мм | 35 | 4 | скрытые защелки |
| ALWT-1325х400-Z-АА | 0.319 м² | 1325 мм | 1320 мм | 400 мм | 396 мм | 241 мм | 843 мм | 40 | 4 | скрытые защелки |
| ALWT-1325х425-Z-АА | 0.339 м² | 1325 мм | 1320 мм | 425 мм | 421 мм | 241 мм | 843 мм | 43 | 4 | скрытые защелки |
| ALWT-1325х450-Z-АА | 0.359 м² | 1325 мм | 1320 мм | 450 мм | 446 мм | 241 мм | 843 мм | 45 | 4 | скрытые защелки |
| ALWT-1325х500-Z-АА | 0.399 м² | 1325 мм | 1320 мм | 500 мм | 496 мм | 241 мм | 843 мм | 50 | 4 | скрытые защелки |
| ALWT-1325х525-Z-АА | 0.418 м² | 1325 мм | 1320 мм | 525 мм | 521 мм | 241 мм | 843 мм | 53 | 4 | скрытые защелки |
| ALWT-1325х550-Z-АА | 0.438 м² | 1325 мм | 1320 мм | 550 мм | 546 мм | 241 мм | 843 мм | 55 | 4 | скрытые защелки |
| ALWT-1325х600-Z-АА | 0.478 м² | 1325 мм | 1320 мм | 600 мм | 596 мм | 241 мм | 843 мм | 60 | 4 | скрытые защелки |
| ALWT-1325х625-Z-АА | 0.498 м² | 1325 мм | 1320 мм | 625 мм | 621 мм | 241 мм | 843 мм | 63 | 4 | скрытые защелки |
| ALWT-1325х650-Z-АА | 0.518 м² | 1325 мм | 1320 мм | 650 мм | 646 мм | 241 мм | 843 мм | 65 | 4 | скрытые защелки |
| ALWT-1350х100-Z-АА | 0.081 м² | 1350 мм | 1345 мм | 100 мм | 96 мм | 245 мм | 859 мм | 10 | 4 | скрытые защелки |
| ALWT-1350х125-Z-АА | 0.102 м² | 1350 мм | 1345 мм | 125 мм | 121 мм | 245 мм | 859 мм | 13 | 4 | скрытые защелки |
| ALWT-1350х150-Z-АА | 0.122 м² | 1350 мм | 1345 мм | 150 мм | 146 мм | 245 мм | 859 мм | 15 | 4 | скрытые защелки |
| ALWT-1350х200-Z-АА | 0.162 м² | 1350 мм | 1345 мм | 200 мм | 196 мм | 245 мм | 859 мм | 20 | 4 | скрытые защелки |
| ALWT-1350х225-Z-АА | 0.183 м² | 1350 мм | 1345 мм | 225 мм | 221 мм | 245 мм | 859 мм | 23 | 4 | скрытые защелки |
| ALWT-1350х250-Z-АА | 0.203 м² | 1350 мм | 1345 мм | 250 мм | 246 мм | 245 мм | 859 мм | 25 | 4 | скрытые защелки |
| ALWT-1350х300-Z-АА | 0.244 м² | 1350 мм | 1345 мм | 300 мм | 296 мм | 245 мм | 859 мм | 30 | 4 | скрытые защелки |
| ALWT-1350х325-Z-АА | 0.264 м² | 1350 мм | 1345 мм | 325 мм | 321 мм | 245 мм | 859 мм | 33 | 4 | скрытые защелки |
| ALWT-1350х350-Z-АА | 0.284 м² | 1350 мм | 1345 мм | 350 мм | 346 мм | 245 мм | 859 мм | 35 | 4 | скрытые защелки |
| ALWT-1350х400-Z-АА | 0.325 м² | 1350 мм | 1345 мм | 400 мм | 396 мм | 245 мм | 859 мм | 40 | 4 | скрытые защелки |
| ALWT-1350х425-Z-АА | 0.345 м² | 1350 мм | 1345 мм | 425 мм | 421 мм | 245 мм | 859 мм | 43 | 4 | скрытые защелки |
| ALWT-1350х450-Z-АА | 0.365 м² | 1350 мм | 1345 мм | 450 мм | 446 мм | 245 мм | 859 мм | 45 | 4 | скрытые защелки |
| ALWT-1350х500-Z-АА | 0.406 м² | 1350 мм | 1345 мм | 500 мм | 496 мм | 245 мм | 859 мм | 50 | 4 | скрытые защелки |
| ALWT-1350х525-Z-АА | 0.426 м² | 1350 мм | 1345 мм | 525 мм | 521 мм | 245 мм | 859 мм | 53 | 4 | скрытые защелки |
| ALWT-1350х550-Z-АА | 0.447 м² | 1350 мм | 1345 мм | 550 мм | 546 мм | 245 мм | 859 мм | 55 | 4 | скрытые защелки |
| ALWT-1350х600-Z-АА | 0.487 м² | 1350 мм | 1345 мм | 600 мм | 596 мм | 245 мм | 859 мм | 60 | 4 | скрытые защелки |
| ALWT-1350х625-Z-АА | 0.508 м² | 1350 мм | 1345 мм | 625 мм | 621 мм | 245 мм | 859 мм | 63 | 4 | скрытые защелки |
| ALWT-1350х650-Z-АА | 0.528 м² | 1350 мм | 1345 мм | 650 мм | 646 мм | 245 мм | 859 мм | 65 | 4 | скрытые защелки |
| ALWT-1400х100-Z-АА | 0.084 м² | 1400 мм | 1395 мм | 100 мм | 96 мм | 255 мм | 891 мм | 10 | 4 | скрытые защелки |
| ALWT-1400х125-Z-АА | 0.105 м² | 1400 мм | 1395 мм | 125 мм | 121 мм | 255 мм | 891 мм | 13 | 4 | скрытые защелки |
| ALWT-1400х150-Z-АА | 0.126 м² | 1400 мм | 1395 мм | 150 мм | 146 мм | 255 мм | 891 мм | 15 | 4 | скрытые защелки |
| ALWT-1400х200-Z-АА | 0.168 м² | 1400 мм | 1395 мм | 200 мм | 196 мм | 255 мм | 891 мм | 20 | 4 | скрытые защелки |
| ALWT-1400х225-Z-АА | 0.190 м² | 1400 мм | 1395 мм | 225 мм | 221 мм | 255 мм | 891 мм | 23 | 4 | скрытые защелки |
| ALWT-1400х250-Z-АА | 0.211 м² | 1400 мм | 1395 мм | 250 мм | 246 мм | 255 мм | 891 мм | 25 | 4 | скрытые защелки |
| ALWT-1400х300-Z-АА | 0.253 м² | 1400 мм | 1395 мм | 300 мм | 296 мм | 255 мм | 891 мм | 30 | 4 | скрытые защелки |
| ALWT-1400х325-Z-АА | 0.274 м² | 1400 мм | 1395 мм | 325 мм | 321 мм | 255 мм | 891 мм | 33 | 4 | скрытые защелки |
| ALWT-1400х350-Z-АА | 0.295 м² | 1400 мм | 1395 мм | 350 мм | 346 мм | 255 мм | 891 мм | 35 | 4 | скрытые защелки |
| ALWT-1400х400-Z-АА | 0.337 м² | 1400 мм | 1395 мм | 400 мм | 396 мм | 255 мм | 891 мм | 40 | 4 | скрытые защелки |
| ALWT-1400х425-Z-АА | 0.358 м² | 1400 мм | 1395 мм | 425 мм | 421 мм | 255 мм | 891 мм | 43 | 4 | скрытые защелки |
| ALWT-1400х450-Z-АА | 0.379 м² | 1400 мм | 1395 мм | 450 мм | 446 мм | 255 мм | 891 мм | 45 | 4 | скрытые защелки |
| ALWT-1400х500-Z-АА | 0.421 м² | 1400 мм | 1395 мм | 500 мм | 496 мм | 255 мм | 891 мм | 50 | 4 | скрытые защелки |
| ALWT-1400х525-Z-АА | 0.442 м² | 1400 мм | 1395 мм | 525 мм | 521 мм | 255 мм | 891 мм | 53 | 4 | скрытые защелки |
| ALWT-1400х550-Z-АА | 0.463 м² | 1400 мм | 1395 мм | 550 мм | 546 мм | 255 мм | 891 мм | 55 | 4 | скрытые защелки |
| ALWT-1400х600-Z-АА | 0.505 м² | 1400 мм | 1395 мм | 600 мм | 596 мм | 255 мм | 891 мм | 60 | 4 | скрытые защелки |
| ALWT-1400х625-Z-АА | 0.526 м² | 1400 мм | 1395 мм | 625 мм | 621 мм | 255 мм | 891 мм | 63 | 4 | скрытые защелки |
| ALWT-1400х650-Z-АА | 0.547 м² | 1400 мм | 1395 мм | 650 мм | 646 мм | 255 мм | 891 мм | 65 | 4 | скрытые защелки |
| ALWT-1425х100-Z-АА | 0.086 м² | 1425 мм | 1420 мм | 100 мм | 96 мм | 259 мм | 907 мм | 10 | 4 | скрытые защелки |
| ALWT-1425х125-Z-АА | 0.107 м² | 1425 мм | 1420 мм | 125 мм | 121 мм | 259 мм | 907 мм | 13 | 4 | скрытые защелки |
| ALWT-1425х150-Z-АА | 0.129 м² | 1425 мм | 1420 мм | 150 мм | 146 мм | 259 мм | 907 мм | 15 | 4 | скрытые защелки |
| ALWT-1425х200-Z-АА | 0.171 м² | 1425 мм | 1420 мм | 200 мм | 196 мм | 259 мм | 907 мм | 20 | 4 | скрытые защелки |
| ALWT-1425х225-Z-АА | 0.193 м² | 1425 мм | 1420 мм | 225 мм | 221 мм | 259 мм | 907 мм | 23 | 4 | скрытые защелки |
| ALWT-1425х250-Z-АА | 0.214 м² | 1425 мм | 1420 мм | 250 мм | 246 мм | 259 мм | 907 мм | 25 | 4 | скрытые защелки |
| ALWT-1425х300-Z-АА | 0.257 м² | 1425 мм | 1420 мм | 300 мм | 296 мм | 259 мм | 907 мм | 30 | 4 | скрытые защелки |
| ALWT-1425х325-Z-АА | 0.279 м² | 1425 мм | 1420 мм | 325 мм | 321 мм | 259 мм | 907 мм | 33 | 4 | скрытые защелки |
| ALWT-1425х350-Z-АА | 0.300 м² | 1425 мм | 1420 мм | 350 мм | 346 мм | 259 мм | 907 мм | 35 | 4 | скрытые защелки |
| ALWT-1425х400-Z-АА | 0.343 м² | 1425 мм | 1420 мм | 400 мм | 396 мм | 259 мм | 907 мм | 40 | 4 | скрытые защелки |
| ALWT-1425х425-Z-АА | 0.364 м² | 1425 мм | 1420 мм | 425 мм | 421 мм | 259 мм | 907 мм | 43 | 4 | скрытые защелки |
| ALWT-1425х450-Z-АА | 0.386 м² | 1425 мм | 1420 мм | 450 мм | 446 мм | 259 мм | 907 мм | 45 | 4 | скрытые защелки |
| ALWT-1425х500-Z-АА | 0.429 м² | 1425 мм | 1420 мм | 500 мм | 496 мм | 259 мм | 907 мм | 50 | 4 | скрытые защелки |
| ALWT-1425х525-Z-АА | 0.450 м² | 1425 мм | 1420 мм | 525 мм | 521 мм | 259 мм | 907 мм | 53 | 4 | скрытые защелки |
| ALWT-1425х550-Z-АА | 0.472 м² | 1425 мм | 1420 мм | 550 мм | 546 мм | 259 мм | 907 мм | 55 | 4 | скрытые защелки |
| ALWT-1425х600-Z-АА | 0.514 м² | 1425 мм | 1420 мм | 600 мм | 596 мм | 259 мм | 907 мм | 60 | 4 | скрытые защелки |
| ALWT-1425х625-Z-АА | 0.536 м² | 1425 мм | 1420 мм | 625 мм | 621 мм | 259 мм | 907 мм | 63 | 4 | скрытые защелки |
| ALWT-1425х650-Z-АА | 0.557 м² | 1425 мм | 1420 мм | 650 мм | 646 мм | 259 мм | 907 мм | 65 | 4 | скрытые защелки |
| ALWT-1450х100-Z-АА | 0.087 м² | 1450 мм | 1445 мм | 100 мм | 96 мм | 264 мм | 923 мм | 10 | 4 | скрытые защелки |
| ALWT-1450х125-Z-АА | 0.109 м² | 1450 мм | 1445 мм | 125 мм | 121 мм | 264 мм | 923 мм | 13 | 4 | скрытые защелки |
| ALWT-1450х150-Z-АА | 0.131 м² | 1450 мм | 1445 мм | 150 мм | 146 мм | 264 мм | 923 мм | 15 | 4 | скрытые защелки |
| ALWT-1450х200-Z-АА | 0.174 м² | 1450 мм | 1445 мм | 200 мм | 196 мм | 264 мм | 923 мм | 20 | 4 | скрытые защелки |
| ALWT-1450х225-Z-АА | 0.196 м² | 1450 мм | 1445 мм | 225 мм | 221 мм | 264 мм | 923 мм | 23 | 4 | скрытые защелки |
| ALWT-1450х250-Z-АА | 0.218 м² | 1450 мм | 1445 мм | 250 мм | 246 мм | 264 мм | 923 мм | 25 | 4 | скрытые защелки |
| ALWT-1450х300-Z-АА | 0.262 м² | 1450 мм | 1445 мм | 300 мм | 296 мм | 264 мм | 923 мм | 30 | 4 | скрытые защелки |
| ALWT-1450х325-Z-АА | 0.284 м² | 1450 мм | 1445 мм | 325 мм | 321 мм | 264 мм | 923 мм | 33 | 4 | скрытые защелки |
| ALWT-1450х350-Z-АА | 0.305 м² | 1450 мм | 1445 мм | 350 мм | 346 мм | 264 мм | 923 мм | 35 | 4 | скрытые защелки |
| ALWT-1450х400-Z-АА | 0.349 м² | 1450 мм | 1445 мм | 400 мм | 396 мм | 264 мм | 923 мм | 40 | 4 | скрытые защелки |
| ALWT-1450х425-Z-АА | 0.371 м² | 1450 мм | 1445 мм | 425 мм | 421 мм | 264 мм | 923 мм | 43 | 4 | скрытые защелки |
| ALWT-1450х450-Z-АА | 0.393 м² | 1450 мм | 1445 мм | 450 мм | 446 мм | 264 мм | 923 мм | 45 | 4 | скрытые защелки |
| ALWT-1450х500-Z-АА | 0.436 м² | 1450 мм | 1445 мм | 500 мм | 496 мм | 264 мм | 923 мм | 50 | 4 | скрытые защелки |
| ALWT-1450х525-Z-АА | 0.458 м² | 1450 мм | 1445 мм | 525 мм | 521 мм | 264 мм | 923 мм | 53 | 4 | скрытые защелки |
| ALWT-1450х550-Z-АА | 0.480 м² | 1450 мм | 1445 мм | 550 мм | 546 мм | 264 мм | 923 мм | 55 | 4 | скрытые защелки |
| ALWT-1450х600-Z-АА | 0.523 м² | 1450 мм | 1445 мм | 600 мм | 596 мм | 264 мм | 923 мм | 60 | 4 | скрытые защелки |
| ALWT-1450х625-Z-АА | 0.545 м² | 1450 мм | 1445 мм | 625 мм | 621 мм | 264 мм | 923 мм | 63 | 4 | скрытые защелки |
| ALWT-1450х650-Z-АА | 0.567 м² | 1450 мм | 1445 мм | 650 мм | 646 мм | 264 мм | 923 мм | 65 | 4 | скрытые защелки |
| ALWT-1500х100-Z-АА | 0.090 м² | 1500 мм | 1495 мм | 100 мм | 96 мм | 273 мм | 955 мм | 10 | 4 | скрытые защелки |
| ALWT-1500х125-Z-АА | 0.113 м² | 1500 мм | 1495 мм | 125 мм | 121 мм | 273 мм | 955 мм | 13 | 4 | скрытые защелки |
| ALWT-1500х150-Z-АА | 0.135 м² | 1500 мм | 1495 мм | 150 мм | 146 мм | 273 мм | 955 мм | 15 | 4 | скрытые защелки |
| ALWT-1500х200-Z-АА | 0.180 м² | 1500 мм | 1495 мм | 200 мм | 196 мм | 273 мм | 955 мм | 20 | 4 | скрытые защелки |
| ALWT-1500х225-Z-АА | 0.203 м² | 1500 мм | 1495 мм | 225 мм | 221 мм | 273 мм | 955 мм | 23 | 4 | скрытые защелки |
| ALWT-1500х250-Z-АА | 0.226 м² | 1500 мм | 1495 мм | 250 мм | 246 мм | 273 мм | 955 мм | 25 | 4 | скрытые защелки |
| ALWT-1500х300-Z-АА | 0.271 м² | 1500 мм | 1495 мм | 300 мм | 296 мм | 273 мм | 955 мм | 30 | 4 | скрытые защелки |
| ALWT-1500х325-Z-АА | 0.293 м² | 1500 мм | 1495 мм | 325 мм | 321 мм | 273 мм | 955 мм | 33 | 4 | скрытые защелки |
| ALWT-1500х350-Z-АА | 0.316 м² | 1500 мм | 1495 мм | 350 мм | 346 мм | 273 мм | 955 мм | 35 | 4 | скрытые защелки |
| ALWT-1500х400-Z-АА | 0.361 м² | 1500 мм | 1495 мм | 400 мм | 396 мм | 273 мм | 955 мм | 40 | 4 | скрытые защелки |
| ALWT-1500х425-Z-АА | 0.384 м² | 1500 мм | 1495 мм | 425 мм | 421 мм | 273 мм | 955 мм | 43 | 4 | скрытые защелки |
| ALWT-1500х450-Z-АА | 0.406 м² | 1500 мм | 1495 мм | 450 мм | 446 мм | 273 мм | 955 мм | 45 | 4 | скрытые защелки |
| ALWT-1500х500-Z-АА | 0.451 м² | 1500 мм | 1495 мм | 500 мм | 496 мм | 273 мм | 955 мм | 50 | 4 | скрытые защелки |
| ALWT-1500х525-Z-АА | 0.474 м² | 1500 мм | 1495 мм | 525 мм | 521 мм | 273 мм | 955 мм | 53 | 4 | скрытые защелки |
| ALWT-1500х550-Z-АА | 0.496 м² | 1500 мм | 1495 мм | 550 мм | 546 мм | 273 мм | 955 мм | 55 | 4 | скрытые защелки |
| ALWT-1500х600-Z-АА | 0.541 м² | 1500 мм | 1495 мм | 600 мм | 596 мм | 273 мм | 955 мм | 60 | 4 | скрытые защелки |
| ALWT-1500х625-Z-АА | 0.564 м² | 1500 мм | 1495 мм | 625 мм | 621 мм | 273 мм | 955 мм | 63 | 4 | скрытые защелки |
| ALWT-1500х650-Z-АА | 0.587 м² | 1500 мм | 1495 мм | 650 мм | 646 мм | 273 мм | 955 мм | 65 | 4 | скрытые защелки |
| ALWT-100х100-S-АА | 0.006 м² | 100 мм | 95 мм | 100 мм | 96 мм | 18 мм | 64 мм | 10 | 2 | потайной замок |
| ALWT-125х100-S-АА | 0.008 м² | 125 мм | 120 мм | 100 мм | 96 мм | 23 мм | 80 мм | 10 | 2 | потайной замок |
| ALWT-125х125-S-АА | 0.009 м² | 125 мм | 120 мм | 125 мм | 121 мм | 23 мм | 80 мм | 13 | 2 | потайной замок |
| ALWT-150х100-S-АА | 0.009 м² | 150 мм | 145 мм | 100 мм | 96 мм | 27 мм | 95 мм | 10 | 2 | потайной замок |
| ALWT-150х125-S-АА | 0.011 м² | 150 мм | 145 мм | 125 мм | 121 мм | 27 мм | 95 мм | 13 | 2 | потайной замок |
| ALWT-150х150-S-АА | 0.014 м² | 150 мм | 145 мм | 150 мм | 146 мм | 27 мм | 95 мм | 15 | 2 | потайной замок |
| ALWT-200х100-S-АА | 0.012 м² | 200 мм | 195 мм | 100 мм | 96 мм | 36 мм | 127 мм | 10 | 2 | потайной замок |
| ALWT-200х125-S-АА | 0.015 м² | 200 мм | 195 мм | 125 мм | 121 мм | 36 мм | 127 мм | 13 | 2 | потайной замок |
| ALWT-200х150-S-АА | 0.018 м² | 200 мм | 195 мм | 150 мм | 146 мм | 36 мм | 127 мм | 15 | 2 | потайной замок |
| ALWT-200х200-S-АА | 0.024 м² | 200 мм | 195 мм | 200 мм | 196 мм | 36 мм | 127 мм | 20 | 2 | потайной замок |
| ALWT-225х100-S-АА | 0.014 м² | 225 мм | 220 мм | 100 мм | 96 мм | 41 мм | 143 мм | 10 | 2 | потайной замок |
| ALWT-225х125-S-АА | 0.017 м² | 225 мм | 220 мм | 125 мм | 121 мм | 41 мм | 143 мм | 13 | 2 | потайной замок |
| ALWT-225х150-S-АА | 0.020 м² | 225 мм | 220 мм | 150 мм | 146 мм | 41 мм | 143 мм | 15 | 2 | потайной замок |
| ALWT-225х200-S-АА | 0.027 м² | 225 мм | 220 мм | 200 мм | 196 мм | 41 мм | 143 мм | 20 | 2 | потайной замок |
| ALWT-225х225-S-АА | 0.030 м² | 225 мм | 220 мм | 225 мм | 221 мм | 41 мм | 143 мм | 23 | 2 | потайной замок |
| ALWT-250х100-S-АА | 0.015 м² | 250 мм | 245 мм | 100 мм | 96 мм | 45 мм | 159 мм | 10 | 2 | потайной замок |
| ALWT-250х125-S-АА | 0.019 м² | 250 мм | 245 мм | 125 мм | 121 мм | 45 мм | 159 мм | 13 | 2 | потайной замок |
| ALWT-250х150-S-АА | 0.023 м² | 250 мм | 245 мм | 150 мм | 146 мм | 45 мм | 159 мм | 15 | 2 | потайной замок |
| ALWT-250х200-S-АА | 0.030 м² | 250 мм | 245 мм | 200 мм | 196 мм | 45 мм | 159 мм | 20 | 2 | потайной замок |
| ALWT-250х225-S-АА | 0.034 м² | 250 мм | 245 мм | 225 мм | 221 мм | 45 мм | 159 мм | 23 | 2 | потайной замок |
| ALWT-250х250-S-АА | 0.038 м² | 250 мм | 245 мм | 250 мм | 246 мм | 45 мм | 159 мм | 25 | 2 | потайной замок |
| ALWT-300х100-S-АА | 0.018 м² | 300 мм | 295 мм | 100 мм | 96 мм | 55 мм | 191 мм | 10 | 2 | потайной замок |
| ALWT-300х125-S-АА | 0.023 м² | 300 мм | 295 мм | 125 мм | 121 мм | 55 мм | 191 мм | 13 | 2 | потайной замок |
| ALWT-300х150-S-АА | 0.027 м² | 300 мм | 295 мм | 150 мм | 146 мм | 55 мм | 191 мм | 15 | 2 | потайной замок |
| ALWT-300х200-S-АА | 0.036 м² | 300 мм | 295 мм | 200 мм | 196 мм | 55 мм | 191 мм | 20 | 2 | потайной замок |
| ALWT-300х225-S-АА | 0.041 м² | 300 мм | 295 мм | 225 мм | 221 мм | 55 мм | 191 мм | 23 | 2 | потайной замок |
| ALWT-300х250-S-АА | 0.045 м² | 300 мм | 295 мм | 250 мм | 246 мм | 55 мм | 191 мм | 25 | 2 | потайной замок |
| ALWT-300х300-S-АА | 0.054 м² | 300 мм | 295 мм | 300 мм | 296 мм | 55 мм | 191 мм | 30 | 2 | потайной замок |
| ALWT-325х100-S-АА | 0.020 м² | 325 мм | 320 мм | 100 мм | 96 мм | 59 мм | 207 мм | 10 | 2 | потайной замок |
| ALWT-325х125-S-АА | 0.024 м² | 325 мм | 320 мм | 125 мм | 121 мм | 59 мм | 207 мм | 13 | 2 | потайной замок |
| ALWT-325х150-S-АА | 0.029 м² | 325 мм | 320 мм | 150 мм | 146 мм | 59 мм | 207 мм | 15 | 2 | потайной замок |
| ALWT-325х200-S-АА | 0.039 м² | 325 мм | 320 мм | 200 мм | 196 мм | 59 мм | 207 мм | 20 | 2 | потайной замок |
| ALWT-325х225-S-АА | 0.044 м² | 325 мм | 320 мм | 225 мм | 221 мм | 59 мм | 207 мм | 23 | 2 | потайной замок |
| ALWT-325х250-S-АА | 0.049 м² | 325 мм | 320 мм | 250 мм | 246 мм | 59 мм | 207 мм | 25 | 2 | потайной замок |
| ALWT-325х300-S-АА | 0.059 м² | 325 мм | 320 мм | 300 мм | 296 мм | 59 мм | 207 мм | 30 | 2 | потайной замок |
| ALWT-325х325-S-АА | 0.064 м² | 325 мм | 320 мм | 325 мм | 321 мм | 59 мм | 207 мм | 33 | 2 | потайной замок |
| ALWT-350х100-S-АА | 0.021 м² | 350 мм | 345 мм | 100 мм | 96 мм | 64 мм | 223 мм | 10 | 2 | потайной замок |
| ALWT-350х125-S-АА | 0.026 м² | 350 мм | 345 мм | 125 мм | 121 мм | 64 мм | 223 мм | 13 | 2 | потайной замок |
| ALWT-350х150-S-АА | 0.032 м² | 350 мм | 345 мм | 150 мм | 146 мм | 64 мм | 223 мм | 15 | 2 | потайной замок |
| ALWT-350х200-S-АА | 0.042 м² | 350 мм | 345 мм | 200 мм | 196 мм | 64 мм | 223 мм | 20 | 2 | потайной замок |
| ALWT-350х225-S-АА | 0.047 м² | 350 мм | 345 мм | 225 мм | 221 мм | 64 мм | 223 мм | 23 | 2 | потайной замок |
| ALWT-350х250-S-АА | 0.053 м² | 350 мм | 345 мм | 250 мм | 246 мм | 64 мм | 223 мм | 25 | 2 | потайной замок |
| ALWT-350х300-S-АА | 0.063 м² | 350 мм | 345 мм | 300 мм | 296 мм | 64 мм | 223 мм | 30 | 2 | потайной замок |
| ALWT-350х325-S-АА | 0.068 м² | 350 мм | 345 мм | 325 мм | 321 мм | 64 мм | 223 мм | 33 | 2 | потайной замок |
| ALWT-350х350-S-АА | 0.074 м² | 350 мм | 345 мм | 350 мм | 346 мм | 64 мм | 223 мм | 35 | 2 | потайной замок |
| ALWT-400х100-S-АА | 0.024 м² | 400 мм | 395 мм | 100 мм | 96 мм | 73 мм | 255 мм | 10 | 3 | потайной замок |
| ALWT-400х125-S-АА | 0.030 м² | 400 мм | 395 мм | 125 мм | 121 мм | 73 мм | 255 мм | 13 | 3 | потайной замок |
| ALWT-400х150-S-АА | 0.036 м² | 400 мм | 395 мм | 150 мм | 146 мм | 73 мм | 255 мм | 15 | 3 | потайной замок |
| ALWT-400х200-S-АА | 0.048 м² | 400 мм | 395 мм | 200 мм | 196 мм | 73 мм | 255 мм | 20 | 3 | потайной замок |
| ALWT-400х225-S-АА | 0.054 м² | 400 мм | 395 мм | 225 мм | 221 мм | 73 мм | 255 мм | 23 | 3 | потайной замок |
| ALWT-400х250-S-АА | 0.060 м² | 400 мм | 395 мм | 250 мм | 246 мм | 73 мм | 255 мм | 25 | 3 | потайной замок |
| ALWT-400х300-S-АА | 0.072 м² | 400 мм | 395 мм | 300 мм | 296 мм | 73 мм | 255 мм | 30 | 3 | потайной замок |
| ALWT-400х325-S-АА | 0.078 м² | 400 мм | 395 мм | 325 мм | 321 мм | 73 мм | 255 мм | 33 | 3 | потайной замок |
| ALWT-400х350-S-АА | 0.084 м² | 400 мм | 395 мм | 350 мм | 346 мм | 73 мм | 255 мм | 35 | 3 | потайной замок |
| ALWT-400х400-S-АА | 0.096 м² | 400 мм | 395 мм | 400 мм | 396 мм | 73 мм | 255 мм | 40 | 3 | потайной замок |
| ALWT-425х100-S-АА | 0.026 м² | 425 мм | 420 мм | 100 мм | 96 мм | 77 мм | 270 мм | 10 | 3 | потайной замок |
| ALWT-425х125-S-АА | 0.032 м² | 425 мм | 420 мм | 125 мм | 121 мм | 77 мм | 270 мм | 13 | 3 | потайной замок |
| ALWT-425х150-S-АА | 0.038 м² | 425 мм | 420 мм | 150 мм | 146 мм | 77 мм | 270 мм | 15 | 3 | потайной замок |
| ALWT-425х200-S-АА | 0.051 м² | 425 мм | 420 мм | 200 мм | 196 мм | 77 мм | 270 мм | 20 | 3 | потайной замок |
| ALWT-425х225-S-АА | 0.058 м² | 425 мм | 420 мм | 225 мм | 221 мм | 77 мм | 270 мм | 23 | 3 | потайной замок |
| ALWT-425х250-S-АА | 0.064 м² | 425 мм | 420 мм | 250 мм | 246 мм | 77 мм | 270 мм | 25 | 3 | потайной замок |
| ALWT-425х300-S-АА | 0.077 м² | 425 мм | 420 мм | 300 мм | 296 мм | 77 мм | 270 мм | 30 | 3 | потайной замок |
| ALWT-425х325-S-АА | 0.083 м² | 425 мм | 420 мм | 325 мм | 321 мм | 77 мм | 270 мм | 33 | 3 | потайной замок |
| ALWT-425х350-S-АА | 0.089 м² | 425 мм | 420 мм | 350 мм | 346 мм | 77 мм | 270 мм | 35 | 3 | потайной замок |
| ALWT-425х400-S-АА | 0.102 м² | 425 мм | 420 мм | 400 мм | 396 мм | 77 мм | 270 мм | 40 | 3 | потайной замок |
| ALWT-425х425-S-АА | 0.109 м² | 425 мм | 420 мм | 425 мм | 421 мм | 77 мм | 270 мм | 43 | 3 | потайной замок |
| ALWT-450х100-S-АА | 0.027 м² | 450 мм | 445 мм | 100 мм | 96 мм | 82 мм | 286 мм | 10 | 3 | потайной замок |
| ALWT-450х125-S-АА | 0.034 м² | 450 мм | 445 мм | 125 мм | 121 мм | 82 мм | 286 мм | 13 | 3 | потайной замок |
| ALWT-450х150-S-АА | 0.041 м² | 450 мм | 445 мм | 150 мм | 146 мм | 82 мм | 286 мм | 15 | 3 | потайной замок |
| ALWT-450х200-S-АА | 0.054 м² | 450 мм | 445 мм | 200 мм | 196 мм | 82 мм | 286 мм | 20 | 3 | потайной замок |
| ALWT-450х225-S-АА | 0.061 м² | 450 мм | 445 мм | 225 мм | 221 мм | 82 мм | 286 мм | 23 | 3 | потайной замок |
| ALWT-450х250-S-АА | 0.068 м² | 450 мм | 445 мм | 250 мм | 246 мм | 82 мм | 286 мм | 25 | 3 | потайной замок |
| ALWT-450х300-S-АА | 0.081 м² | 450 мм | 445 мм | 300 мм | 296 мм | 82 мм | 286 мм | 30 | 3 | потайной замок |
| ALWT-450х325-S-АА | 0.088 м² | 450 мм | 445 мм | 325 мм | 321 мм | 82 мм | 286 мм | 33 | 3 | потайной замок |
| ALWT-450х350-S-АА | 0.095 м² | 450 мм | 445 мм | 350 мм | 346 мм | 82 мм | 286 мм | 35 | 3 | потайной замок |
| ALWT-450х400-S-АА | 0.108 м² | 450 мм | 445 мм | 400 мм | 396 мм | 82 мм | 286 мм | 40 | 3 | потайной замок |
| ALWT-450х425-S-АА | 0.115 м² | 450 мм | 445 мм | 425 мм | 421 мм | 82 мм | 286 мм | 43 | 3 | потайной замок |
| ALWT-450х450-S-АА | 0.122 м² | 450 мм | 445 мм | 450 мм | 446 мм | 82 мм | 286 мм | 45 | 3 | потайной замок |
| ALWT-500х100-S-АА | 0.030 м² | 500 мм | 495 мм | 100 мм | 96 мм | 91 мм | 318 мм | 10 | 3 | потайной замок |
| ALWT-500х125-S-АА | 0.038 м² | 500 мм | 495 мм | 125 мм | 121 мм | 91 мм | 318 мм | 13 | 3 | потайной замок |
| ALWT-500х150-S-АА | 0.045 м² | 500 мм | 495 мм | 150 мм | 146 мм | 91 мм | 318 мм | 15 | 3 | потайной замок |
| ALWT-500х200-S-АА | 0.060 м² | 500 мм | 495 мм | 200 мм | 196 мм | 91 мм | 318 мм | 20 | 3 | потайной замок |
| ALWT-500х225-S-АА | 0.068 м² | 500 мм | 495 мм | 225 мм | 221 мм | 91 мм | 318 мм | 23 | 3 | потайной замок |
| ALWT-500х250-S-АА | 0.075 м² | 500 мм | 495 мм | 250 мм | 246 мм | 91 мм | 318 мм | 25 | 3 | потайной замок |
| ALWT-500х300-S-АА | 0.090 м² | 500 мм | 495 мм | 300 мм | 296 мм | 91 мм | 318 мм | 30 | 3 | потайной замок |
| ALWT-500х325-S-АА | 0.098 м² | 500 мм | 495 мм | 325 мм | 321 мм | 91 мм | 318 мм | 33 | 3 | потайной замок |
| ALWT-500х350-S-АА | 0.105 м² | 500 мм | 495 мм | 350 мм | 346 мм | 91 мм | 318 мм | 35 | 3 | потайной замок |
| ALWT-500х400-S-АА | 0.120 м² | 500 мм | 495 мм | 400 мм | 396 мм | 91 мм | 318 мм | 40 | 3 | потайной замок |
| ALWT-500х425-S-АА | 0.128 м² | 500 мм | 495 мм | 425 мм | 421 мм | 91 мм | 318 мм | 43 | 3 | потайной замок |
| ALWT-500х450-S-АА | 0.135 м² | 500 мм | 495 мм | 450 мм | 446 мм | 91 мм | 318 мм | 45 | 3 | потайной замок |
| ALWT-500х500-S-АА | 0.150 м² | 500 мм | 495 мм | 500 мм | 496 мм | 91 мм | 318 мм | 50 | 3 | потайной замок |
| ALWT-525х100-S-АА | 0.032 м² | 525 мм | 520 мм | 100 мм | 96 мм | 95 мм | 334 мм | 10 | 3 | потайной замок |
| ALWT-525х125-S-АА | 0.039 м² | 525 мм | 520 мм | 125 мм | 121 мм | 95 мм | 334 мм | 13 | 3 | потайной замок |
| ALWT-525х150-S-АА | 0.047 м² | 525 мм | 520 мм | 150 мм | 146 мм | 95 мм | 334 мм | 15 | 3 | потайной замок |
| ALWT-525х200-S-АА | 0.063 м² | 525 мм | 520 мм | 200 мм | 196 мм | 95 мм | 334 мм | 20 | 3 | потайной замок |
| ALWT-525х225-S-АА | 0.071 м² | 525 мм | 520 мм | 225 мм | 221 мм | 95 мм | 334 мм | 23 | 3 | потайной замок |
| ALWT-525х250-S-АА | 0.079 м² | 525 мм | 520 мм | 250 мм | 246 мм | 95 мм | 334 мм | 25 | 3 | потайной замок |
| ALWT-525х300-S-АА | 0.095 м² | 525 мм | 520 мм | 300 мм | 296 мм | 95 мм | 334 мм | 30 | 3 | потайной замок |
| ALWT-525х325-S-АА | 0.103 м² | 525 мм | 520 мм | 325 мм | 321 мм | 95 мм | 334 мм | 33 | 3 | потайной замок |
| ALWT-525х350-S-АА | 0.111 м² | 525 мм | 520 мм | 350 мм | 346 мм | 95 мм | 334 мм | 35 | 3 | потайной замок |
| ALWT-525х400-S-АА | 0.126 м² | 525 мм | 520 мм | 400 мм | 396 мм | 95 мм | 334 мм | 40 | 3 | потайной замок |
| ALWT-525х425-S-АА | 0.134 м² | 525 мм | 520 мм | 425 мм | 421 мм | 95 мм | 334 мм | 43 | 3 | потайной замок |
| ALWT-525х450-S-АА | 0.142 м² | 525 мм | 520 мм | 450 мм | 446 мм | 95 мм | 334 мм | 45 | 3 | потайной замок |
| ALWT-525х500-S-АА | 0.158 м² | 525 мм | 520 мм | 500 мм | 496 мм | 95 мм | 334 мм | 50 | 3 | потайной замок |
| ALWT-525х525-S-АА | 0.166 м² | 525 мм | 520 мм | 525 мм | 521 мм | 95 мм | 334 мм | 53 | 3 | потайной замок |
| ALWT-550х100-S-АА | 0.033 м² | 550 мм | 545 мм | 100 мм | 96 мм | 100 мм | 350 мм | 10 | 3 | потайной замок |
| ALWT-550х125-S-АА | 0.041 м² | 550 мм | 545 мм | 125 мм | 121 мм | 100 мм | 350 мм | 13 | 3 | потайной замок |
| ALWT-550х150-S-АА | 0.050 м² | 550 мм | 545 мм | 150 мм | 146 мм | 100 мм | 350 мм | 15 | 3 | потайной замок |
| ALWT-550х200-S-АА | 0.066 м² | 550 мм | 545 мм | 200 мм | 196 мм | 100 мм | 350 мм | 20 | 3 | потайной замок |
| ALWT-550х225-S-АА | 0.074 м² | 550 мм | 545 мм | 225 мм | 221 мм | 100 мм | 350 мм | 23 | 3 | потайной замок |
| ALWT-550х250-S-АА | 0.083 м² | 550 мм | 545 мм | 250 мм | 246 мм | 100 мм | 350 мм | 25 | 3 | потайной замок |
| ALWT-550х300-S-АА | 0.099 м² | 550 мм | 545 мм | 300 мм | 296 мм | 100 мм | 350 мм | 30 | 3 | потайной замок |
| ALWT-550х325-S-АА | 0.108 м² | 550 мм | 545 мм | 325 мм | 321 мм | 100 мм | 350 мм | 33 | 3 | потайной замок |
| ALWT-550х350-S-АА | 0.116 м² | 550 мм | 545 мм | 350 мм | 346 мм | 100 мм | 350 мм | 35 | 3 | потайной замок |
| ALWT-550х400-S-АА | 0.132 м² | 550 мм | 545 мм | 400 мм | 396 мм | 100 мм | 350 мм | 40 | 3 | потайной замок |
| ALWT-550х425-S-АА | 0.141 м² | 550 мм | 545 мм | 425 мм | 421 мм | 100 мм | 350 мм | 43 | 3 | потайной замок |
| ALWT-550х450-S-АА | 0.149 м² | 550 мм | 545 мм | 450 мм | 446 мм | 100 мм | 350 мм | 45 | 3 | потайной замок |
| ALWT-550х500-S-АА | 0.165 м² | 550 мм | 545 мм | 500 мм | 496 мм | 100 мм | 350 мм | 50 | 3 | потайной замок |
| ALWT-550х525-S-АА | 0.174 м² | 550 мм | 545 мм | 525 мм | 521 мм | 100 мм | 350 мм | 53 | 3 | потайной замок |
| ALWT-550х550-S-АА | 0.182 м² | 550 мм | 545 мм | 550 мм | 546 мм | 100 мм | 350 мм | 55 | 3 | потайной замок |
| ALWT-600х100-S-АА | 0.036 м² | 600 мм | 595 мм | 100 мм | 96 мм | 109 мм | 382 мм | 10 | 3 | потайной замок |
| ALWT-600х125-S-АА | 0.045 м² | 600 мм | 595 мм | 125 мм | 121 мм | 109 мм | 382 мм | 13 | 3 | потайной замок |
| ALWT-600х150-S-АА | 0.054 м² | 600 мм | 595 мм | 150 мм | 146 мм | 109 мм | 382 мм | 15 | 3 | потайной замок |
| ALWT-600х200-S-АА | 0.072 м² | 600 мм | 595 мм | 200 мм | 196 мм | 109 мм | 382 мм | 20 | 3 | потайной замок |
| ALWT-600х225-S-АА | 0.081 м² | 600 мм | 595 мм | 225 мм | 221 мм | 109 мм | 382 мм | 23 | 3 | потайной замок |
| ALWT-600х250-S-АА | 0.090 м² | 600 мм | 595 мм | 250 мм | 246 мм | 109 мм | 382 мм | 25 | 3 | потайной замок |
| ALWT-600х300-S-АА | 0.108 м² | 600 мм | 595 мм | 300 мм | 296 мм | 109 мм | 382 мм | 30 | 3 | потайной замок |
| ALWT-600х325-S-АА | 0.117 м² | 600 мм | 595 мм | 325 мм | 321 мм | 109 мм | 382 мм | 33 | 3 | потайной замок |
| ALWT-600х350-S-АА | 0.126 м² | 600 мм | 595 мм | 350 мм | 346 мм | 109 мм | 382 мм | 35 | 3 | потайной замок |
| ALWT-600х400-S-АА | 0.144 м² | 600 мм | 595 мм | 400 мм | 396 мм | 109 мм | 382 мм | 40 | 3 | потайной замок |
| ALWT-600х425-S-АА | 0.153 м² | 600 мм | 595 мм | 425 мм | 421 мм | 109 мм | 382 мм | 43 | 3 | потайной замок |
| ALWT-600х450-S-АА | 0.162 м² | 600 мм | 595 мм | 450 мм | 446 мм | 109 мм | 382 мм | 45 | 3 | потайной замок |
| ALWT-600х500-S-АА | 0.180 м² | 600 мм | 595 мм | 500 мм | 496 мм | 109 мм | 382 мм | 50 | 3 | потайной замок |
| ALWT-600х525-S-АА | 0.190 м² | 600 мм | 595 мм | 525 мм | 521 мм | 109 мм | 382 мм | 53 | 3 | потайной замок |
| ALWT-600х550-S-АА | 0.199 м² | 600 мм | 595 мм | 550 мм | 546 мм | 109 мм | 382 мм | 55 | 3 | потайной замок |
| ALWT-600х600-S-АА | 0.217 м² | 600 мм | 595 мм | 600 мм | 596 мм | 109 мм | 382 мм | 60 | 3 | потайной замок |
| ALWT-625х100-S-АА | 0.038 м² | 625 мм | 620 мм | 100 мм | 96 мм | 114 мм | 398 мм | 10 | 3 | потайной замок |
| ALWT-625х125-S-АА | 0.047 м² | 625 мм | 620 мм | 125 мм | 121 мм | 114 мм | 398 мм | 13 | 3 | потайной замок |
| ALWT-625х150-S-АА | 0.056 м² | 625 мм | 620 мм | 150 мм | 146 мм | 114 мм | 398 мм | 15 | 3 | потайной замок |
| ALWT-625х200-S-АА | 0.075 м² | 625 мм | 620 мм | 200 мм | 196 мм | 114 мм | 398 мм | 20 | 3 | потайной замок |
| ALWT-625х225-S-АА | 0.085 м² | 625 мм | 620 мм | 225 мм | 221 мм | 114 мм | 398 мм | 23 | 3 | потайной замок |
| ALWT-625х250-S-АА | 0.094 м² | 625 мм | 620 мм | 250 мм | 246 мм | 114 мм | 398 мм | 25 | 3 | потайной замок |
| ALWT-625х300-S-АА | 0.113 м² | 625 мм | 620 мм | 300 мм | 296 мм | 114 мм | 398 мм | 30 | 3 | потайной замок |
| ALWT-625х325-S-АА | 0.122 м² | 625 мм | 620 мм | 325 мм | 321 мм | 114 мм | 398 мм | 33 | 3 | потайной замок |
| ALWT-625х350-S-АА | 0.132 м² | 625 мм | 620 мм | 350 мм | 346 мм | 114 мм | 398 мм | 35 | 3 | потайной замок |
| ALWT-625х400-S-АА | 0.150 м² | 625 мм | 620 мм | 400 мм | 396 мм | 114 мм | 398 мм | 40 | 3 | потайной замок |
| ALWT-625х425-S-АА | 0.160 м² | 625 мм | 620 мм | 425 мм | 421 мм | 114 мм | 398 мм | 43 | 3 | потайной замок |
| ALWT-625х450-S-АА | 0.169 м² | 625 мм | 620 мм | 450 мм | 446 мм | 114 мм | 398 мм | 45 | 3 | потайной замок |
| ALWT-625х500-S-АА | 0.188 м² | 625 мм | 620 мм | 500 мм | 496 мм | 114 мм | 398 мм | 50 | 3 | потайной замок |
| ALWT-625х525-S-АА | 0.197 м² | 625 мм | 620 мм | 525 мм | 521 мм | 114 мм | 398 мм | 53 | 3 | потайной замок |
| ALWT-625х550-S-АА | 0.207 м² | 625 мм | 620 мм | 550 мм | 546 мм | 114 мм | 398 мм | 55 | 3 | потайной замок |
| ALWT-625х600-S-АА | 0.226 м² | 625 мм | 620 мм | 600 мм | 596 мм | 114 мм | 398 мм | 60 | 3 | потайной замок |
| ALWT-625х625-S-АА | 0.235 м² | 625 мм | 620 мм | 625 мм | 621 мм | 114 мм | 398 мм | 63 | 3 | потайной замок |
| ALWT-650х100-S-АА | 0.039 м² | 650 мм | 645 мм | 100 мм | 96 мм | 118 мм | 414 мм | 10 | 3 | потайной замок |
| ALWT-650х125-S-АА | 0.049 м² | 650 мм | 645 мм | 125 мм | 121 мм | 118 мм | 414 мм | 13 | 3 | потайной замок |
| ALWT-650х150-S-АА | 0.059 м² | 650 мм | 645 мм | 150 мм | 146 мм | 118 мм | 414 мм | 15 | 3 | потайной замок |
| ALWT-650х200-S-АА | 0.078 м² | 650 мм | 645 мм | 200 мм | 196 мм | 118 мм | 414 мм | 20 | 3 | потайной замок |
| ALWT-650х225-S-АА | 0.088 м² | 650 мм | 645 мм | 225 мм | 221 мм | 118 мм | 414 мм | 23 | 3 | потайной замок |
| ALWT-650х250-S-АА | 0.098 м² | 650 мм | 645 мм | 250 мм | 246 мм | 118 мм | 414 мм | 25 | 3 | потайной замок |
| ALWT-650х300-S-АА | 0.117 м² | 650 мм | 645 мм | 300 мм | 296 мм | 118 мм | 414 мм | 30 | 3 | потайной замок |
| ALWT-650х325-S-АА | 0.127 м² | 650 мм | 645 мм | 325 мм | 321 мм | 118 мм | 414 мм | 33 | 3 | потайной замок |
| ALWT-650х350-S-АА | 0.137 м² | 650 мм | 645 мм | 350 мм | 346 мм | 118 мм | 414 мм | 35 | 3 | потайной замок |
| ALWT-650х400-S-АА | 0.156 м² | 650 мм | 645 мм | 400 мм | 396 мм | 118 мм | 414 мм | 40 | 3 | потайной замок |
| ALWT-650х425-S-АА | 0.166 м² | 650 мм | 645 мм | 425 мм | 421 мм | 118 мм | 414 мм | 43 | 3 | потайной замок |
| ALWT-650х450-S-АА | 0.176 м² | 650 мм | 645 мм | 450 мм | 446 мм | 118 мм | 414 мм | 45 | 3 | потайной замок |
| ALWT-650х500-S-АА | 0.196 м² | 650 мм | 645 мм | 500 мм | 496 мм | 118 мм | 414 мм | 50 | 3 | потайной замок |
| ALWT-650х525-S-АА | 0.205 м² | 650 мм | 645 мм | 525 мм | 521 мм | 118 мм | 414 мм | 53 | 3 | потайной замок |
| ALWT-650х550-S-АА | 0.215 м² | 650 мм | 645 мм | 550 мм | 546 мм | 118 мм | 414 мм | 55 | 3 | потайной замок |
| ALWT-650х600-S-АА | 0.235 м² | 650 мм | 645 мм | 600 мм | 596 мм | 118 мм | 414 мм | 60 | 3 | потайной замок |
| ALWT-650х625-S-АА | 0.244 м² | 650 мм | 645 мм | 625 мм | 621 мм | 118 мм | 414 мм | 63 | 3 | потайной замок |
| ALWT-650х650-S-АА | 0.254 м² | 650 мм | 645 мм | 650 мм | 646 мм | 118 мм | 414 мм | 65 | 3 | потайной замок |
| ALWT-700х100-S-АА | 0.042 м² | 700 мм | 695 мм | 100 мм | 96 мм | 127 мм | 445 мм | 10 | 3 | потайной замок |
| ALWT-700х125-S-АА | 0.053 м² | 700 мм | 695 мм | 125 мм | 121 мм | 127 мм | 445 мм | 13 | 3 | потайной замок |
| ALWT-700х150-S-АА | 0.063 м² | 700 мм | 695 мм | 150 мм | 146 мм | 127 мм | 445 мм | 15 | 3 | потайной замок |
| ALWT-700х200-S-АА | 0.084 м² | 700 мм | 695 мм | 200 мм | 196 мм | 127 мм | 445 мм | 20 | 3 | потайной замок |
| ALWT-700х225-S-АА | 0.095 м² | 700 мм | 695 мм | 225 мм | 221 мм | 127 мм | 445 мм | 23 | 3 | потайной замок |
| ALWT-700х250-S-АА | 0.105 м² | 700 мм | 695 мм | 250 мм | 246 мм | 127 мм | 445 мм | 25 | 3 | потайной замок |
| ALWT-700х300-S-АА | 0.126 м² | 700 мм | 695 мм | 300 мм | 296 мм | 127 мм | 445 мм | 30 | 3 | потайной замок |
| ALWT-700х325-S-АА | 0.137 м² | 700 мм | 695 мм | 325 мм | 321 мм | 127 мм | 445 мм | 33 | 3 | потайной замок |
| ALWT-700х350-S-АА | 0.147 м² | 700 мм | 695 мм | 350 мм | 346 мм | 127 мм | 445 мм | 35 | 3 | потайной замок |
| ALWT-700х400-S-АА | 0.168 м² | 700 мм | 695 мм | 400 мм | 396 мм | 127 мм | 445 мм | 40 | 3 | потайной замок |
| ALWT-700х425-S-АА | 0.179 м² | 700 мм | 695 мм | 425 мм | 421 мм | 127 мм | 445 мм | 43 | 3 | потайной замок |
| ALWT-700х450-S-АА | 0.190 м² | 700 мм | 695 мм | 450 мм | 446 мм | 127 мм | 445 мм | 45 | 3 | потайной замок |
| ALWT-700х500-S-АА | 0.211 м² | 700 мм | 695 мм | 500 мм | 496 мм | 127 мм | 445 мм | 50 | 3 | потайной замок |
| ALWT-700х525-S-АА | 0.221 м² | 700 мм | 695 мм | 525 мм | 521 мм | 127 мм | 445 мм | 53 | 3 | потайной замок |
| ALWT-700х550-S-АА | 0.232 м² | 700 мм | 695 мм | 550 мм | 546 мм | 127 мм | 445 мм | 55 | 3 | потайной замок |
| ALWT-700х600-S-АА | 0.253 м² | 700 мм | 695 мм | 600 мм | 596 мм | 127 мм | 445 мм | 60 | 3 | потайной замок |
| ALWT-700х625-S-АА | 0.263 м² | 700 мм | 695 мм | 625 мм | 621 мм | 127 мм | 445 мм | 63 | 3 | потайной замок |
| ALWT-700х650-S-АА | 0.274 м² | 700 мм | 695 мм | 650 мм | 646 мм | 127 мм | 445 мм | 65 | 3 | потайной замок |
| ALWT-725х100-S-АА | 0.044 м² | 725 мм | 720 мм | 100 мм | 96 мм | 132 мм | 461 мм | 10 | 3 | потайной замок |
| ALWT-725х125-S-АА | 0.055 м² | 725 мм | 720 мм | 125 мм | 121 мм | 132 мм | 461 мм | 13 | 3 | потайной замок |
| ALWT-725х150-S-АА | 0.065 м² | 725 мм | 720 мм | 150 мм | 146 мм | 132 мм | 461 мм | 15 | 3 | потайной замок |
| ALWT-725х200-S-АА | 0.087 м² | 725 мм | 720 мм | 200 мм | 196 мм | 132 мм | 461 мм | 20 | 3 | потайной замок |
| ALWT-725х225-S-АА | 0.098 м² | 725 мм | 720 мм | 225 мм | 221 мм | 132 мм | 461 мм | 23 | 3 | потайной замок |
| ALWT-725х250-S-АА | 0.109 м² | 725 мм | 720 мм | 250 мм | 246 мм | 132 мм | 461 мм | 25 | 3 | потайной замок |
| ALWT-725х300-S-АА | 0.131 м² | 725 мм | 720 мм | 300 мм | 296 мм | 132 мм | 461 мм | 30 | 3 | потайной замок |
| ALWT-725х325-S-АА | 0.142 м² | 725 мм | 720 мм | 325 мм | 321 мм | 132 мм | 461 мм | 33 | 3 | потайной замок |
| ALWT-725х350-S-АА | 0.153 м² | 725 мм | 720 мм | 350 мм | 346 мм | 132 мм | 461 мм | 35 | 3 | потайной замок |
| ALWT-725х400-S-АА | 0.174 м² | 725 мм | 720 мм | 400 мм | 396 мм | 132 мм | 461 мм | 40 | 3 | потайной замок |
| ALWT-725х425-S-АА | 0.185 м² | 725 мм | 720 мм | 425 мм | 421 мм | 132 мм | 461 мм | 43 | 3 | потайной замок |
| ALWT-725х450-S-АА | 0.196 м² | 725 мм | 720 мм | 450 мм | 446 мм | 132 мм | 461 мм | 45 | 3 | потайной замок |
| ALWT-725х500-S-АА | 0.218 м² | 725 мм | 720 мм | 500 мм | 496 мм | 132 мм | 461 мм | 50 | 3 | потайной замок |
| ALWT-725х525-S-АА | 0.229 м² | 725 мм | 720 мм | 525 мм | 521 мм | 132 мм | 461 мм | 53 | 3 | потайной замок |
| ALWT-725х550-S-АА | 0.240 м² | 725 мм | 720 мм | 550 мм | 546 мм | 132 мм | 461 мм | 55 | 3 | потайной замок |
| ALWT-725х600-S-АА | 0.262 м² | 725 мм | 720 мм | 600 мм | 596 мм | 132 мм | 461 мм | 60 | 3 | потайной замок |
| ALWT-725х625-S-АА | 0.273 м² | 725 мм | 720 мм | 625 мм | 621 мм | 132 мм | 461 мм | 63 | 3 | потайной замок |
| ALWT-725х650-S-АА | 0.284 м² | 725 мм | 720 мм | 650 мм | 646 мм | 132 мм | 461 мм | 65 | 3 | потайной замок |
| ALWT-750х100-S-АА | 0.045 м² | 750 мм | 745 мм | 100 мм | 96 мм | 136 мм | 477 мм | 10 | 3 | потайной замок |
| ALWT-750х125-S-АА | 0.056 м² | 750 мм | 745 мм | 125 мм | 121 мм | 136 мм | 477 мм | 13 | 3 | потайной замок |
| ALWT-750х150-S-АА | 0.068 м² | 750 мм | 745 мм | 150 мм | 146 мм | 136 мм | 477 мм | 15 | 3 | потайной замок |
| ALWT-750х200-S-АА | 0.090 м² | 750 мм | 745 мм | 200 мм | 196 мм | 136 мм | 477 мм | 20 | 3 | потайной замок |
| ALWT-750х225-S-АА | 0.102 м² | 750 мм | 745 мм | 225 мм | 221 мм | 136 мм | 477 мм | 23 | 3 | потайной замок |
| ALWT-750х250-S-АА | 0.113 м² | 750 мм | 745 мм | 250 мм | 246 мм | 136 мм | 477 мм | 25 | 3 | потайной замок |
| ALWT-750х300-S-АА | 0.135 м² | 750 мм | 745 мм | 300 мм | 296 мм | 136 мм | 477 мм | 30 | 3 | потайной замок |
| ALWT-750х325-S-АА | 0.147 м² | 750 мм | 745 мм | 325 мм | 321 мм | 136 мм | 477 мм | 33 | 3 | потайной замок |
| ALWT-750х350-S-АА | 0.158 м² | 750 мм | 745 мм | 350 мм | 346 мм | 136 мм | 477 мм | 35 | 3 | потайной замок |
| ALWT-750х400-S-АА | 0.180 м² | 750 мм | 745 мм | 400 мм | 396 мм | 136 мм | 477 мм | 40 | 3 | потайной замок |
| ALWT-750х425-S-АА | 0.192 м² | 750 мм | 745 мм | 425 мм | 421 мм | 136 мм | 477 мм | 43 | 3 | потайной замок |
| ALWT-750х450-S-АА | 0.203 м² | 750 мм | 745 мм | 450 мм | 446 мм | 136 мм | 477 мм | 45 | 3 | потайной замок |
| ALWT-750х500-S-АА | 0.226 м² | 750 мм | 745 мм | 500 мм | 496 мм | 136 мм | 477 мм | 50 | 3 | потайной замок |
| ALWT-750х525-S-АА | 0.237 м² | 750 мм | 745 мм | 525 мм | 521 мм | 136 мм | 477 мм | 53 | 3 | потайной замок |
| ALWT-750х550-S-АА | 0.248 м² | 750 мм | 745 мм | 550 мм | 546 мм | 136 мм | 477 мм | 55 | 3 | потайной замок |
| ALWT-750х600-S-АА | 0.271 м² | 750 мм | 745 мм | 600 мм | 596 мм | 136 мм | 477 мм | 60 | 3 | потайной замок |
| ALWT-750х625-S-АА | 0.282 м² | 750 мм | 745 мм | 625 мм | 621 мм | 136 мм | 477 мм | 63 | 3 | потайной замок |
| ALWT-750х650-S-АА | 0.293 м² | 750 мм | 745 мм | 650 мм | 646 мм | 136 мм | 477 мм | 65 | 3 | потайной замок |
| ALWT-800х100-S-АА | 0.048 м² | 800 мм | 795 мм | 100 мм | 96 мм | 145 мм | 509 мм | 10 | 4 | потайной замок |
| ALWT-800х125-S-АА | 0.060 м² | 800 мм | 795 мм | 125 мм | 121 мм | 145 мм | 509 мм | 13 | 4 | потайной замок |
| ALWT-800х150-S-АА | 0.072 м² | 800 мм | 795 мм | 150 мм | 146 мм | 145 мм | 509 мм | 15 | 4 | потайной замок |
| ALWT-800х200-S-АА | 0.096 м² | 800 мм | 795 мм | 200 мм | 196 мм | 145 мм | 509 мм | 20 | 4 | потайной замок |
| ALWT-800х225-S-АА | 0.108 м² | 800 мм | 795 мм | 225 мм | 221 мм | 145 мм | 509 мм | 23 | 4 | потайной замок |
| ALWT-800х250-S-АА | 0.120 м² | 800 мм | 795 мм | 250 мм | 246 мм | 145 мм | 509 мм | 25 | 4 | потайной замок |
| ALWT-800х300-S-АА | 0.144 м² | 800 мм | 795 мм | 300 мм | 296 мм | 145 мм | 509 мм | 30 | 4 | потайной замок |
| ALWT-800х325-S-АА | 0.156 м² | 800 мм | 795 мм | 325 мм | 321 мм | 145 мм | 509 мм | 33 | 4 | потайной замок |
| ALWT-800х350-S-АА | 0.168 м² | 800 мм | 795 мм | 350 мм | 346 мм | 145 мм | 509 мм | 35 | 4 | потайной замок |
| ALWT-800х400-S-АА | 0.193 м² | 800 мм | 795 мм | 400 мм | 396 мм | 145 мм | 509 мм | 40 | 4 | потайной замок |
| ALWT-800х425-S-АА | 0.205 м² | 800 мм | 795 мм | 425 мм | 421 мм | 145 мм | 509 мм | 43 | 4 | потайной замок |
| ALWT-800х450-S-АА | 0.217 м² | 800 мм | 795 мм | 450 мм | 446 мм | 145 мм | 509 мм | 45 | 4 | потайной замок |
| ALWT-800х500-S-АА | 0.241 м² | 800 мм | 795 мм | 500 мм | 496 мм | 145 мм | 509 мм | 50 | 4 | потайной замок |
| ALWT-800х525-S-АА | 0.253 м² | 800 мм | 795 мм | 525 мм | 521 мм | 145 мм | 509 мм | 53 | 4 | потайной замок |
| ALWT-800х550-S-АА | 0.265 м² | 800 мм | 795 мм | 550 мм | 546 мм | 145 мм | 509 мм | 55 | 4 | потайной замок |
| ALWT-800х600-S-АА | 0.289 м² | 800 мм | 795 мм | 600 мм | 596 мм | 145 мм | 509 мм | 60 | 4 | потайной замок |
| ALWT-800х625-S-АА | 0.301 м² | 800 мм | 795 мм | 625 мм | 621 мм | 145 мм | 509 мм | 63 | 4 | потайной замок |
| ALWT-800х650-S-АА | 0.313 м² | 800 мм | 795 мм | 650 мм | 646 мм | 145 мм | 509 мм | 65 | 4 | потайной замок |
| ALWT-825х100-S-АА | 0.050 м² | 825 мм | 820 мм | 100 мм | 96 мм | 150 мм | 525 мм | 10 | 4 | потайной замок |
| ALWT-825х125-S-АА | 0.062 м² | 825 мм | 820 мм | 125 мм | 121 мм | 150 мм | 525 мм | 13 | 4 | потайной замок |
| ALWT-825х150-S-АА | 0.074 м² | 825 мм | 820 мм | 150 мм | 146 мм | 150 мм | 525 мм | 15 | 4 | потайной замок |
| ALWT-825х200-S-АА | 0.099 м² | 825 мм | 820 мм | 200 мм | 196 мм | 150 мм | 525 мм | 20 | 4 | потайной замок |
| ALWT-825х225-S-АА | 0.112 м² | 825 мм | 820 мм | 225 мм | 221 мм | 150 мм | 525 мм | 23 | 4 | потайной замок |
| ALWT-825х250-S-АА | 0.124 м² | 825 мм | 820 мм | 250 мм | 246 мм | 150 мм | 525 мм | 25 | 4 | потайной замок |
| ALWT-825х300-S-АА | 0.149 м² | 825 мм | 820 мм | 300 мм | 296 мм | 150 мм | 525 мм | 30 | 4 | потайной замок |
| ALWT-825х325-S-АА | 0.161 м² | 825 мм | 820 мм | 325 мм | 321 мм | 150 мм | 525 мм | 33 | 4 | потайной замок |
| ALWT-825х350-S-АА | 0.174 м² | 825 мм | 820 мм | 350 мм | 346 мм | 150 мм | 525 мм | 35 | 4 | потайной замок |
| ALWT-825х400-S-АА | 0.199 м² | 825 мм | 820 мм | 400 мм | 396 мм | 150 мм | 525 мм | 40 | 4 | потайной замок |
| ALWT-825х425-S-АА | 0.211 м² | 825 мм | 820 мм | 425 мм | 421 мм | 150 мм | 525 мм | 43 | 4 | потайной замок |
| ALWT-825х450-S-АА | 0.223 м² | 825 мм | 820 мм | 450 мм | 446 мм | 150 мм | 525 мм | 45 | 4 | потайной замок |
| ALWT-825х500-S-АА | 0.248 м² | 825 мм | 820 мм | 500 мм | 496 мм | 150 мм | 525 мм | 50 | 4 | потайной замок |
| ALWT-825х525-S-АА | 0.261 м² | 825 мм | 820 мм | 525 мм | 521 мм | 150 мм | 525 мм | 53 | 4 | потайной замок |
| ALWT-825х550-S-АА | 0.273 м² | 825 мм | 820 мм | 550 мм | 546 мм | 150 мм | 525 мм | 55 | 4 | потайной замок |
| ALWT-825х600-S-АА | 0.298 м² | 825 мм | 820 мм | 600 мм | 596 мм | 150 мм | 525 мм | 60 | 4 | потайной замок |
| ALWT-825х625-S-АА | 0.310 м² | 825 мм | 820 мм | 625 мм | 621 мм | 150 мм | 525 мм | 63 | 4 | потайной замок |
| ALWT-825х650-S-АА | 0.323 м² | 825 мм | 820 мм | 650 мм | 646 мм | 150 мм | 525 мм | 65 | 4 | потайной замок |
| ALWT-850х100-S-АА | 0.051 м² | 850 мм | 845 мм | 100 мм | 96 мм | 155 мм | 541 мм | 10 | 4 | потайной замок |
| ALWT-850х125-S-АА | 0.064 м² | 850 мм | 845 мм | 125 мм | 121 мм | 155 мм | 541 мм | 13 | 4 | потайной замок |
| ALWT-850х150-S-АА | 0.077 м² | 850 мм | 845 мм | 150 мм | 146 мм | 155 мм | 541 мм | 15 | 4 | потайной замок |
| ALWT-850х200-S-АА | 0.102 м² | 850 мм | 845 мм | 200 мм | 196 мм | 155 мм | 541 мм | 20 | 4 | потайной замок |
| ALWT-850х225-S-АА | 0.115 м² | 850 мм | 845 мм | 225 мм | 221 мм | 155 мм | 541 мм | 23 | 4 | потайной замок |
| ALWT-850х250-S-АА | 0.128 м² | 850 мм | 845 мм | 250 мм | 246 мм | 155 мм | 541 мм | 25 | 4 | потайной замок |
| ALWT-850х300-S-АА | 0.153 м² | 850 мм | 845 мм | 300 мм | 296 мм | 155 мм | 541 мм | 30 | 4 | потайной замок |
| ALWT-850х325-S-АА | 0.166 м² | 850 мм | 845 мм | 325 мм | 321 мм | 155 мм | 541 мм | 33 | 4 | потайной замок |
| ALWT-850х350-S-АА | 0.179 м² | 850 мм | 845 мм | 350 мм | 346 мм | 155 мм | 541 мм | 35 | 4 | потайной замок |
| ALWT-850х400-S-АА | 0.205 м² | 850 мм | 845 мм | 400 мм | 396 мм | 155 мм | 541 мм | 40 | 4 | потайной замок |
| ALWT-850х425-S-АА | 0.217 м² | 850 мм | 845 мм | 425 мм | 421 мм | 155 мм | 541 мм | 43 | 4 | потайной замок |
| ALWT-850х450-S-АА | 0.230 м² | 850 мм | 845 мм | 450 мм | 446 мм | 155 мм | 541 мм | 45 | 4 | потайной замок |
| ALWT-850х500-S-АА | 0.256 м² | 850 мм | 845 мм | 500 мм | 496 мм | 155 мм | 541 мм | 50 | 4 | потайной замок |
| ALWT-850х525-S-АА | 0.268 м² | 850 мм | 845 мм | 525 мм | 521 мм | 155 мм | 541 мм | 53 | 4 | потайной замок |
| ALWT-850х550-S-АА | 0.281 м² | 850 мм | 845 мм | 550 мм | 546 мм | 155 мм | 541 мм | 55 | 4 | потайной замок |
| ALWT-850х600-S-АА | 0.307 м² | 850 мм | 845 мм | 600 мм | 596 мм | 155 мм | 541 мм | 60 | 4 | потайной замок |
| ALWT-850х625-S-АА | 0.320 м² | 850 мм | 845 мм | 625 мм | 621 мм | 155 мм | 541 мм | 63 | 4 | потайной замок |
| ALWT-850х650-S-АА | 0.332 м² | 850 мм | 845 мм | 650 мм | 646 мм | 155 мм | 541 мм | 65 | 4 | потайной замок |
| ALWT-900х100-S-АА | 0.054 м² | 900 мм | 895 мм | 100 мм | 96 мм | 164 мм | 573 мм | 10 | 4 | потайной замок |
| ALWT-900х125-S-АА | 0.068 м² | 900 мм | 895 мм | 125 мм | 121 мм | 164 мм | 573 мм | 13 | 4 | потайной замок |
| ALWT-900х150-S-АА | 0.081 м² | 900 мм | 895 мм | 150 мм | 146 мм | 164 мм | 573 мм | 15 | 4 | потайной замок |
| ALWT-900х200-S-АА | 0.108 м² | 900 мм | 895 мм | 200 мм | 196 мм | 164 мм | 573 мм | 20 | 4 | потайной замок |
| ALWT-900х225-S-АА | 0.122 м² | 900 мм | 895 мм | 225 мм | 221 мм | 164 мм | 573 мм | 23 | 4 | потайной замок |
| ALWT-900х250-S-АА | 0.135 м² | 900 мм | 895 мм | 250 мм | 246 мм | 164 мм | 573 мм | 25 | 4 | потайной замок |
| ALWT-900х300-S-АА | 0.162 м² | 900 мм | 895 мм | 300 мм | 296 мм | 164 мм | 573 мм | 30 | 4 | потайной замок |
| ALWT-900х325-S-АА | 0.176 м² | 900 мм | 895 мм | 325 мм | 321 мм | 164 мм | 573 мм | 33 | 4 | потайной замок |
| ALWT-900х350-S-АА | 0.190 м² | 900 мм | 895 мм | 350 мм | 346 мм | 164 мм | 573 мм | 35 | 4 | потайной замок |
| ALWT-900х400-S-АА | 0.217 м² | 900 мм | 895 мм | 400 мм | 396 мм | 164 мм | 573 мм | 40 | 4 | потайной замок |
| ALWT-900х425-S-АА | 0.230 м² | 900 мм | 895 мм | 425 мм | 421 мм | 164 мм | 573 мм | 43 | 4 | потайной замок |
| ALWT-900х450-S-АА | 0.244 м² | 900 мм | 895 мм | 450 мм | 446 мм | 164 мм | 573 мм | 45 | 4 | потайной замок |
| ALWT-900х500-S-АА | 0.271 м² | 900 мм | 895 мм | 500 мм | 496 мм | 164 мм | 573 мм | 50 | 4 | потайной замок |
| ALWT-900х525-S-АА | 0.284 м² | 900 мм | 895 мм | 525 мм | 521 мм | 164 мм | 573 мм | 53 | 4 | потайной замок |
| ALWT-900х550-S-АА | 0.298 м² | 900 мм | 895 мм | 550 мм | 546 мм | 164 мм | 573 мм | 55 | 4 | потайной замок |
| ALWT-900х600-S-АА | 0.325 м² | 900 мм | 895 мм | 600 мм | 596 мм | 164 мм | 573 мм | 60 | 4 | потайной замок |
| ALWT-900х625-S-АА | 0.338 м² | 900 мм | 895 мм | 625 мм | 621 мм | 164 мм | 573 мм | 63 | 4 | потайной замок |
| ALWT-900х650-S-АА | 0.352 м² | 900 мм | 895 мм | 650 мм | 646 мм | 164 мм | 573 мм | 65 | 4 | потайной замок |
| ALWT-925х100-S-АА | 0.056 м² | 925 мм | 920 мм | 100 мм | 96 мм | 168 мм | 589 мм | 10 | 4 | потайной замок |
| ALWT-925х125-S-АА | 0.070 м² | 925 мм | 920 мм | 125 мм | 121 мм | 168 мм | 589 мм | 13 | 4 | потайной замок |
| ALWT-925х150-S-АА | 0.083 м² | 925 мм | 920 мм | 150 мм | 146 мм | 168 мм | 589 мм | 15 | 4 | потайной замок |
| ALWT-925х200-S-АА | 0.111 м² | 925 мм | 920 мм | 200 мм | 196 мм | 168 мм | 589 мм | 20 | 4 | потайной замок |
| ALWT-925х225-S-АА | 0.125 м² | 925 мм | 920 мм | 225 мм | 221 мм | 168 мм | 589 мм | 23 | 4 | потайной замок |
| ALWT-925х250-S-АА | 0.139 м² | 925 мм | 920 мм | 250 мм | 246 мм | 168 мм | 589 мм | 25 | 4 | потайной замок |
| ALWT-925х300-S-АА | 0.167 м² | 925 мм | 920 мм | 300 мм | 296 мм | 168 мм | 589 мм | 30 | 4 | потайной замок |
| ALWT-925х325-S-АА | 0.181 м² | 925 мм | 920 мм | 325 мм | 321 мм | 168 мм | 589 мм | 33 | 4 | потайной замок |
| ALWT-925х350-S-АА | 0.195 м² | 925 мм | 920 мм | 350 мм | 346 мм | 168 мм | 589 мм | 35 | 4 | потайной замок |
| ALWT-925х400-S-АА | 0.223 м² | 925 мм | 920 мм | 400 мм | 396 мм | 168 мм | 589 мм | 40 | 4 | потайной замок |
| ALWT-925х425-S-АА | 0.237 м² | 925 мм | 920 мм | 425 мм | 421 мм | 168 мм | 589 мм | 43 | 4 | потайной замок |
| ALWT-925х450-S-АА | 0.250 м² | 925 мм | 920 мм | 450 мм | 446 мм | 168 мм | 589 мм | 45 | 4 | потайной замок |
| ALWT-925х500-S-АА | 0.278 м² | 925 мм | 920 мм | 500 мм | 496 мм | 168 мм | 589 мм | 50 | 4 | потайной замок |
| ALWT-925х525-S-АА | 0.292 м² | 925 мм | 920 мм | 525 мм | 521 мм | 168 мм | 589 мм | 53 | 4 | потайной замок |
| ALWT-925х550-S-АА | 0.306 м² | 925 мм | 920 мм | 550 мм | 546 мм | 168 мм | 589 мм | 55 | 4 | потайной замок |
| ALWT-925х600-S-АА | 0.334 м² | 925 мм | 920 мм | 600 мм | 596 мм | 168 мм | 589 мм | 60 | 4 | потайной замок |
| ALWT-925х625-S-АА | 0.348 м² | 925 мм | 920 мм | 625 мм | 621 мм | 168 мм | 589 мм | 63 | 4 | потайной замок |
| ALWT-925х650-S-АА | 0.362 м² | 925 мм | 920 мм | 650 мм | 646 мм | 168 мм | 589 мм | 65 | 4 | потайной замок |
| ALWT-950х100-S-АА | 0.057 м² | 950 мм | 945 мм | 100 мм | 96 мм | 173 мм | 605 мм | 10 | 4 | потайной замок |
| ALWT-950х125-S-АА | 0.071 м² | 950 мм | 945 мм | 125 мм | 121 мм | 173 мм | 605 мм | 13 | 4 | потайной замок |
| ALWT-950х150-S-АА | 0.086 м² | 950 мм | 945 мм | 150 мм | 146 мм | 173 мм | 605 мм | 15 | 4 | потайной замок |
| ALWT-950х200-S-АА | 0.114 м² | 950 мм | 945 мм | 200 мм | 196 мм | 173 мм | 605 мм | 20 | 4 | потайной замок |
| ALWT-950х225-S-АА | 0.129 м² | 950 мм | 945 мм | 225 мм | 221 мм | 173 мм | 605 мм | 23 | 4 | потайной замок |
| ALWT-950х250-S-АА | 0.143 м² | 950 мм | 945 мм | 250 мм | 246 мм | 173 мм | 605 мм | 25 | 4 | потайной замок |
| ALWT-950х300-S-АА | 0.171 м² | 950 мм | 945 мм | 300 мм | 296 мм | 173 мм | 605 мм | 30 | 4 | потайной замок |
| ALWT-950х325-S-АА | 0.186 м² | 950 мм | 945 мм | 325 мм | 321 мм | 173 мм | 605 мм | 33 | 4 | потайной замок |
| ALWT-950х350-S-АА | 0.200 м² | 950 мм | 945 мм | 350 мм | 346 мм | 173 мм | 605 мм | 35 | 4 | потайной замок |
| ALWT-950х400-S-АА | 0.229 м² | 950 мм | 945 мм | 400 мм | 396 мм | 173 мм | 605 мм | 40 | 4 | потайной замок |
| ALWT-950х425-S-АА | 0.243 м² | 950 мм | 945 мм | 425 мм | 421 мм | 173 мм | 605 мм | 43 | 4 | потайной замок |
| ALWT-950х450-S-АА | 0.257 м² | 950 мм | 945 мм | 450 мм | 446 мм | 173 мм | 605 мм | 45 | 4 | потайной замок |
| ALWT-950х500-S-АА | 0.286 м² | 950 мм | 945 мм | 500 мм | 496 мм | 173 мм | 605 мм | 50 | 4 | потайной замок |
| ALWT-950х525-S-АА | 0.300 м² | 950 мм | 945 мм | 525 мм | 521 мм | 173 мм | 605 мм | 53 | 4 | потайной замок |
| ALWT-950х550-S-АА | 0.314 м² | 950 мм | 945 мм | 550 мм | 546 мм | 173 мм | 605 мм | 55 | 4 | потайной замок |
| ALWT-950х600-S-АА | 0.343 м² | 950 мм | 945 мм | 600 мм | 596 мм | 173 мм | 605 мм | 60 | 4 | потайной замок |
| ALWT-950х625-S-АА | 0.357 м² | 950 мм | 945 мм | 625 мм | 621 мм | 173 мм | 605 мм | 63 | 4 | потайной замок |
| ALWT-950х650-S-АА | 0.371 м² | 950 мм | 945 мм | 650 мм | 646 мм | 173 мм | 605 мм | 65 | 4 | потайной замок |
| ALWT-1000х100-S-АА | 0.060 м² | 1000 мм | 995 мм | 100 мм | 96 мм | 182 мм | 636 мм | 10 | 4 | потайной замок |
| ALWT-1000х125-S-АА | 0.075 м² | 1000 мм | 995 мм | 125 мм | 121 мм | 182 мм | 636 мм | 13 | 4 | потайной замок |
| ALWT-1000х150-S-АА | 0.090 м² | 1000 мм | 995 мм | 150 мм | 146 мм | 182 мм | 636 мм | 15 | 4 | потайной замок |
| ALWT-1000х200-S-АА | 0.120 м² | 1000 мм | 995 мм | 200 мм | 196 мм | 182 мм | 636 мм | 20 | 4 | потайной замок |
| ALWT-1000х225-S-АА | 0.135 м² | 1000 мм | 995 мм | 225 мм | 221 мм | 182 мм | 636 мм | 23 | 4 | потайной замок |
| ALWT-1000х250-S-АА | 0.150 м² | 1000 мм | 995 мм | 250 мм | 246 мм | 182 мм | 636 мм | 25 | 4 | потайной замок |
| ALWT-1000х300-S-АА | 0.180 м² | 1000 мм | 995 мм | 300 мм | 296 мм | 182 мм | 636 мм | 30 | 4 | потайной замок |
| ALWT-1000х325-S-АА | 0.196 м² | 1000 мм | 995 мм | 325 мм | 321 мм | 182 мм | 636 мм | 33 | 4 | потайной замок |
| ALWT-1000х350-S-АА | 0.211 м² | 1000 мм | 995 мм | 350 мм | 346 мм | 182 мм | 636 мм | 35 | 4 | потайной замок |
| ALWT-1000х400-S-АА | 0.241 м² | 1000 мм | 995 мм | 400 мм | 396 мм | 182 мм | 636 мм | 40 | 4 | потайной замок |
| ALWT-1000х425-S-АА | 0.256 м² | 1000 мм | 995 мм | 425 мм | 421 мм | 182 мм | 636 мм | 43 | 4 | потайной замок |
| ALWT-1000х450-S-АА | 0.271 м² | 1000 мм | 995 мм | 450 мм | 446 мм | 182 мм | 636 мм | 45 | 4 | потайной замок |
| ALWT-1000х500-S-АА | 0.301 м² | 1000 мм | 995 мм | 500 мм | 496 мм | 182 мм | 636 мм | 50 | 4 | потайной замок |
| ALWT-1000х525-S-АА | 0.316 м² | 1000 мм | 995 мм | 525 мм | 521 мм | 182 мм | 636 мм | 53 | 4 | потайной замок |
| ALWT-1000х550-S-АА | 0.331 м² | 1000 мм | 995 мм | 550 мм | 546 мм | 182 мм | 636 мм | 55 | 4 | потайной замок |
| ALWT-1000х600-S-АА | 0.361 м² | 1000 мм | 995 мм | 600 мм | 596 мм | 182 мм | 636 мм | 60 | 4 | потайной замок |
| ALWT-1000х625-S-АА | 0.376 м² | 1000 мм | 995 мм | 625 мм | 621 мм | 182 мм | 636 мм | 63 | 4 | потайной замок |
| ALWT-1000х650-S-АА | 0.391 м² | 1000 мм | 995 мм | 650 мм | 646 мм | 182 мм | 636 мм | 65 | 4 | потайной замок |
| ALWT-1025х100-S-АА | 0.062 м² | 1025 мм | 1020 мм | 100 мм | 96 мм | 186 мм | 652 мм | 10 | 4 | потайной замок |
| ALWT-1025х125-S-АА | 0.077 м² | 1025 мм | 1020 мм | 125 мм | 121 мм | 186 мм | 652 мм | 13 | 4 | потайной замок |
| ALWT-1025х150-S-АА | 0.092 м² | 1025 мм | 1020 мм | 150 мм | 146 мм | 186 мм | 652 мм | 15 | 4 | потайной замок |
| ALWT-1025х200-S-АА | 0.123 м² | 1025 мм | 1020 мм | 200 мм | 196 мм | 186 мм | 652 мм | 20 | 4 | потайной замок |
| ALWT-1025х225-S-АА | 0.139 м² | 1025 мм | 1020 мм | 225 мм | 221 мм | 186 мм | 652 мм | 23 | 4 | потайной замок |
| ALWT-1025х250-S-АА | 0.154 м² | 1025 мм | 1020 мм | 250 мм | 246 мм | 186 мм | 652 мм | 25 | 4 | потайной замок |
| ALWT-1025х300-S-АА | 0.185 м² | 1025 мм | 1020 мм | 300 мм | 296 мм | 186 мм | 652 мм | 30 | 4 | потайной замок |
| ALWT-1025х325-S-АА | 0.200 м² | 1025 мм | 1020 мм | 325 мм | 321 мм | 186 мм | 652 мм | 33 | 4 | потайной замок |
| ALWT-1025х350-S-АА | 0.216 м² | 1025 мм | 1020 мм | 350 мм | 346 мм | 186 мм | 652 мм | 35 | 4 | потайной замок |
| ALWT-1025х400-S-АА | 0.247 м² | 1025 мм | 1020 мм | 400 мм | 396 мм | 186 мм | 652 мм | 40 | 4 | потайной замок |
| ALWT-1025х425-S-АА | 0.262 м² | 1025 мм | 1020 мм | 425 мм | 421 мм | 186 мм | 652 мм | 43 | 4 | потайной замок |
| ALWT-1025х450-S-АА | 0.277 м² | 1025 мм | 1020 мм | 450 мм | 446 мм | 186 мм | 652 мм | 45 | 4 | потайной замок |
| ALWT-1025х500-S-АА | 0.308 м² | 1025 мм | 1020 мм | 500 мм | 496 мм | 186 мм | 652 мм | 50 | 4 | потайной замок |
| ALWT-1025х525-S-АА | 0.324 м² | 1025 мм | 1020 мм | 525 мм | 521 мм | 186 мм | 652 мм | 53 | 4 | потайной замок |
| ALWT-1025х550-S-АА | 0.339 м² | 1025 мм | 1020 мм | 550 мм | 546 мм | 186 мм | 652 мм | 55 | 4 | потайной замок |
| ALWT-1025х600-S-АА | 0.370 м² | 1025 мм | 1020 мм | 600 мм | 596 мм | 186 мм | 652 мм | 60 | 4 | потайной замок |
| ALWT-1025х625-S-АА | 0.385 м² | 1025 мм | 1020 мм | 625 мм | 621 мм | 186 мм | 652 мм | 63 | 4 | потайной замок |
| ALWT-1025х650-S-АА | 0.401 м² | 1025 мм | 1020 мм | 650 мм | 646 мм | 186 мм | 652 мм | 65 | 4 | потайной замок |
| ALWT-1050х100-S-АА | 0.063 м² | 1050 мм | 1045 мм | 100 мм | 96 мм | 191 мм | 668 мм | 10 | 4 | потайной замок |
| ALWT-1050х125-S-АА | 0.079 м² | 1050 мм | 1045 мм | 125 мм | 121 мм | 191 мм | 668 мм | 13 | 4 | потайной замок |
| ALWT-1050х150-S-АА | 0.095 м² | 1050 мм | 1045 мм | 150 мм | 146 мм | 191 мм | 668 мм | 15 | 4 | потайной замок |
| ALWT-1050х200-S-АА | 0.126 м² | 1050 мм | 1045 мм | 200 мм | 196 мм | 191 мм | 668 мм | 20 | 4 | потайной замок |
| ALWT-1050х225-S-АА | 0.142 м² | 1050 мм | 1045 мм | 225 мм | 221 мм | 191 мм | 668 мм | 23 | 4 | потайной замок |
| ALWT-1050х250-S-АА | 0.158 м² | 1050 мм | 1045 мм | 250 мм | 246 мм | 191 мм | 668 мм | 25 | 4 | потайной замок |
| ALWT-1050х300-S-АА | 0.190 м² | 1050 мм | 1045 мм | 300 мм | 296 мм | 191 мм | 668 мм | 30 | 4 | потайной замок |
| ALWT-1050х325-S-АА | 0.205 м² | 1050 мм | 1045 мм | 325 мм | 321 мм | 191 мм | 668 мм | 33 | 4 | потайной замок |
| ALWT-1050х350-S-АА | 0.221 м² | 1050 мм | 1045 мм | 350 мм | 346 мм | 191 мм | 668 мм | 35 | 4 | потайной замок |
| ALWT-1050х400-S-АА | 0.253 м² | 1050 мм | 1045 мм | 400 мм | 396 мм | 191 мм | 668 мм | 40 | 4 | потайной замок |
| ALWT-1050х425-S-АА | 0.268 м² | 1050 мм | 1045 мм | 425 мм | 421 мм | 191 мм | 668 мм | 43 | 4 | потайной замок |
| ALWT-1050х450-S-АА | 0.284 м² | 1050 мм | 1045 мм | 450 мм | 446 мм | 191 мм | 668 мм | 45 | 4 | потайной замок |
| ALWT-1050х500-S-АА | 0.316 м² | 1050 мм | 1045 мм | 500 мм | 496 мм | 191 мм | 668 мм | 50 | 4 | потайной замок |
| ALWT-1050х525-S-АА | 0.332 м² | 1050 мм | 1045 мм | 525 мм | 521 мм | 191 мм | 668 мм | 53 | 4 | потайной замок |
| ALWT-1050х550-S-АА | 0.347 м² | 1050 мм | 1045 мм | 550 мм | 546 мм | 191 мм | 668 мм | 55 | 4 | потайной замок |
| ALWT-1050х600-S-АА | 0.379 м² | 1050 мм | 1045 мм | 600 мм | 596 мм | 191 мм | 668 мм | 60 | 4 | потайной замок |
| ALWT-1050х625-S-АА | 0.395 м² | 1050 мм | 1045 мм | 625 мм | 621 мм | 191 мм | 668 мм | 63 | 4 | потайной замок |
| ALWT-1050х650-S-АА | 0.411 м² | 1050 мм | 1045 мм | 650 мм | 646 мм | 191 мм | 668 мм | 65 | 4 | потайной замок |
| ALWT-1100х100-S-АА | 0.066 м² | 1100 мм | 1095 мм | 100 мм | 96 мм | 200 мм | 700 мм | 10 | 4 | потайной замок |
| ALWT-1100х125-S-АА | 0.083 м² | 1100 мм | 1095 мм | 125 мм | 121 мм | 200 мм | 700 мм | 13 | 4 | потайной замок |
| ALWT-1100х150-S-АА | 0.099 м² | 1100 мм | 1095 мм | 150 мм | 146 мм | 200 мм | 700 мм | 15 | 4 | потайной замок |
| ALWT-1100х200-S-АА | 0.132 м² | 1100 мм | 1095 мм | 200 мм | 196 мм | 200 мм | 700 мм | 20 | 4 | потайной замок |
| ALWT-1100х225-S-АА | 0.149 м² | 1100 мм | 1095 мм | 225 мм | 221 мм | 200 мм | 700 мм | 23 | 4 | потайной замок |
| ALWT-1100х250-S-АА | 0.165 м² | 1100 мм | 1095 мм | 250 мм | 246 мм | 200 мм | 700 мм | 25 | 4 | потайной замок |
| ALWT-1100х300-S-АА | 0.199 м² | 1100 мм | 1095 мм | 300 мм | 296 мм | 200 мм | 700 мм | 30 | 4 | потайной замок |
| ALWT-1100х325-S-АА | 0.215 м² | 1100 мм | 1095 мм | 325 мм | 321 мм | 200 мм | 700 мм | 33 | 4 | потайной замок |
| ALWT-1100х350-S-АА | 0.232 м² | 1100 мм | 1095 мм | 350 мм | 346 мм | 200 мм | 700 мм | 35 | 4 | потайной замок |
| ALWT-1100х400-S-АА | 0.265 м² | 1100 мм | 1095 мм | 400 мм | 396 мм | 200 мм | 700 мм | 40 | 4 | потайной замок |
| ALWT-1100х425-S-АА | 0.281 м² | 1100 мм | 1095 мм | 425 мм | 421 мм | 200 мм | 700 мм | 43 | 4 | потайной замок |
| ALWT-1100х450-S-АА | 0.298 м² | 1100 мм | 1095 мм | 450 мм | 446 мм | 200 мм | 700 мм | 45 | 4 | потайной замок |
| ALWT-1100х500-S-АА | 0.331 м² | 1100 мм | 1095 мм | 500 мм | 496 мм | 200 мм | 700 мм | 50 | 4 | потайной замок |
| ALWT-1100х525-S-АА | 0.347 м² | 1100 мм | 1095 мм | 525 мм | 521 мм | 200 мм | 700 мм | 53 | 4 | потайной замок |
| ALWT-1100х550-S-АА | 0.364 м² | 1100 мм | 1095 мм | 550 мм | 546 мм | 200 мм | 700 мм | 55 | 4 | потайной замок |
| ALWT-1100х600-S-АА | 0.397 м² | 1100 мм | 1095 мм | 600 мм | 596 мм | 200 мм | 700 мм | 60 | 4 | потайной замок |
| ALWT-1100х625-S-АА | 0.414 м² | 1100 мм | 1095 мм | 625 мм | 621 мм | 200 мм | 700 мм | 63 | 4 | потайной замок |
| ALWT-1100х650-S-АА | 0.430 м² | 1100 мм | 1095 мм | 650 мм | 646 мм | 200 мм | 700 мм | 65 | 4 | потайной замок |
| ALWT-1125х100-S-АА | 0.068 м² | 1125 мм | 1120 мм | 100 мм | 96 мм | 205 мм | 716 мм | 10 | 4 | потайной замок |
| ALWT-1125х125-S-АА | 0.085 м² | 1125 мм | 1120 мм | 125 мм | 121 мм | 205 мм | 716 мм | 13 | 4 | потайной замок |
| ALWT-1125х150-S-АА | 0.102 м² | 1125 мм | 1120 мм | 150 мм | 146 мм | 205 мм | 716 мм | 15 | 4 | потайной замок |
| ALWT-1125х200-S-АА | 0.135 м² | 1125 мм | 1120 мм | 200 мм | 196 мм | 205 мм | 716 мм | 20 | 4 | потайной замок |
| ALWT-1125х225-S-АА | 0.152 м² | 1125 мм | 1120 мм | 225 мм | 221 мм | 205 мм | 716 мм | 23 | 4 | потайной замок |
| ALWT-1125х250-S-АА | 0.169 м² | 1125 мм | 1120 мм | 250 мм | 246 мм | 205 мм | 716 мм | 25 | 4 | потайной замок |
| ALWT-1125х300-S-АА | 0.203 м² | 1125 мм | 1120 мм | 300 мм | 296 мм | 205 мм | 716 мм | 30 | 4 | потайной замок |
| ALWT-1125х325-S-АА | 0.220 м² | 1125 мм | 1120 мм | 325 мм | 321 мм | 205 мм | 716 мм | 33 | 4 | потайной замок |
| ALWT-1125х350-S-АА | 0.237 м² | 1125 мм | 1120 мм | 350 мм | 346 мм | 205 мм | 716 мм | 35 | 4 | потайной замок |
| ALWT-1125х400-S-АА | 0.271 м² | 1125 мм | 1120 мм | 400 мм | 396 мм | 205 мм | 716 мм | 40 | 4 | потайной замок |
| ALWT-1125х425-S-АА | 0.288 м² | 1125 мм | 1120 мм | 425 мм | 421 мм | 205 мм | 716 мм | 43 | 4 | потайной замок |
| ALWT-1125х450-S-АА | 0.305 м² | 1125 мм | 1120 мм | 450 мм | 446 мм | 205 мм | 716 мм | 45 | 4 | потайной замок |
| ALWT-1125х500-S-АА | 0.338 м² | 1125 мм | 1120 мм | 500 мм | 496 мм | 205 мм | 716 мм | 50 | 4 | потайной замок |
| ALWT-1125х525-S-АА | 0.355 м² | 1125 мм | 1120 мм | 525 мм | 521 мм | 205 мм | 716 мм | 53 | 4 | потайной замок |
| ALWT-1125х550-S-АА | 0.372 м² | 1125 мм | 1120 мм | 550 мм | 546 мм | 205 мм | 716 мм | 55 | 4 | потайной замок |
| ALWT-1125х600-S-АА | 0.406 м² | 1125 мм | 1120 мм | 600 мм | 596 мм | 205 мм | 716 мм | 60 | 4 | потайной замок |
| ALWT-1125х625-S-АА | 0.423 м² | 1125 мм | 1120 мм | 625 мм | 621 мм | 205 мм | 716 мм | 63 | 4 | потайной замок |
| ALWT-1125х650-S-АА | 0.440 м² | 1125 мм | 1120 мм | 650 мм | 646 мм | 205 мм | 716 мм | 65 | 4 | потайной замок |
| ALWT-1150х100-S-АА | 0.069 м² | 1150 мм | 1145 мм | 100 мм | 96 мм | 209 мм | 732 мм | 10 | 4 | потайной замок |
| ALWT-1150х125-S-АА | 0.086 м² | 1150 мм | 1145 мм | 125 мм | 121 мм | 209 мм | 732 мм | 13 | 4 | потайной замок |
| ALWT-1150х150-S-АА | 0.104 м² | 1150 мм | 1145 мм | 150 мм | 146 мм | 209 мм | 732 мм | 15 | 4 | потайной замок |
| ALWT-1150х200-S-АА | 0.138 м² | 1150 мм | 1145 мм | 200 мм | 196 мм | 209 мм | 732 мм | 20 | 4 | потайной замок |
| ALWT-1150х225-S-АА | 0.156 м² | 1150 мм | 1145 мм | 225 мм | 221 мм | 209 мм | 732 мм | 23 | 4 | потайной замок |
| ALWT-1150х250-S-АА | 0.173 м² | 1150 мм | 1145 мм | 250 мм | 246 мм | 209 мм | 732 мм | 25 | 4 | потайной замок |
| ALWT-1150х300-S-АА | 0.208 м² | 1150 мм | 1145 мм | 300 мм | 296 мм | 209 мм | 732 мм | 30 | 4 | потайной замок |
| ALWT-1150х325-S-АА | 0.225 м² | 1150 мм | 1145 мм | 325 мм | 321 мм | 209 мм | 732 мм | 33 | 4 | потайной замок |
| ALWT-1150х350-S-АА | 0.242 м² | 1150 мм | 1145 мм | 350 мм | 346 мм | 209 мм | 732 мм | 35 | 4 | потайной замок |
| ALWT-1150х400-S-АА | 0.277 м² | 1150 мм | 1145 мм | 400 мм | 396 мм | 209 мм | 732 мм | 40 | 4 | потайной замок |
| ALWT-1150х425-S-АА | 0.294 м² | 1150 мм | 1145 мм | 425 мм | 421 мм | 209 мм | 732 мм | 43 | 4 | потайной замок |
| ALWT-1150х450-S-АА | 0.311 м² | 1150 мм | 1145 мм | 450 мм | 446 мм | 209 мм | 732 мм | 45 | 4 | потайной замок |
| ALWT-1150х500-S-АА | 0.346 м² | 1150 мм | 1145 мм | 500 мм | 496 мм | 209 мм | 732 мм | 50 | 4 | потайной замок |
| ALWT-1150х525-S-АА | 0.363 м² | 1150 мм | 1145 мм | 525 мм | 521 мм | 209 мм | 732 мм | 53 | 4 | потайной замок |
| ALWT-1150х550-S-АА | 0.381 м² | 1150 мм | 1145 мм | 550 мм | 546 мм | 209 мм | 732 мм | 55 | 4 | потайной замок |
| ALWT-1150х600-S-АА | 0.415 м² | 1150 мм | 1145 мм | 600 мм | 596 мм | 209 мм | 732 мм | 60 | 4 | потайной замок |
| ALWT-1150х625-S-АА | 0.432 м² | 1150 мм | 1145 мм | 625 мм | 621 мм | 209 мм | 732 мм | 63 | 4 | потайной замок |
| ALWT-1150х650-S-АА | 0.450 м² | 1150 мм | 1145 мм | 650 мм | 646 мм | 209 мм | 732 мм | 65 | 4 | потайной замок |
| ALWT-1200х100-S-АА | 0.072 м² | 1200 мм | 1195 мм | 100 мм | 96 мм | 218 мм | 764 мм | 10 | 4 | потайной замок |
| ALWT-1200х125-S-АА | 0.090 м² | 1200 мм | 1195 мм | 125 мм | 121 мм | 218 мм | 764 мм | 13 | 4 | потайной замок |
| ALWT-1200х150-S-АА | 0.108 м² | 1200 мм | 1195 мм | 150 мм | 146 мм | 218 мм | 764 мм | 15 | 4 | потайной замок |
| ALWT-1200х200-S-АА | 0.144 м² | 1200 мм | 1195 мм | 200 мм | 196 мм | 218 мм | 764 мм | 20 | 4 | потайной замок |
| ALWT-1200х225-S-АА | 0.162 м² | 1200 мм | 1195 мм | 225 мм | 221 мм | 218 мм | 764 мм | 23 | 4 | потайной замок |
| ALWT-1200х250-S-АА | 0.180 м² | 1200 мм | 1195 мм | 250 мм | 246 мм | 218 мм | 764 мм | 25 | 4 | потайной замок |
| ALWT-1200х300-S-АА | 0.217 м² | 1200 мм | 1195 мм | 300 мм | 296 мм | 218 мм | 764 мм | 30 | 4 | потайной замок |
| ALWT-1200х325-S-АА | 0.235 м² | 1200 мм | 1195 мм | 325 мм | 321 мм | 218 мм | 764 мм | 33 | 4 | потайной замок |
| ALWT-1200х350-S-АА | 0.253 м² | 1200 мм | 1195 мм | 350 мм | 346 мм | 218 мм | 764 мм | 35 | 4 | потайной замок |
| ALWT-1200х400-S-АА | 0.289 м² | 1200 мм | 1195 мм | 400 мм | 396 мм | 218 мм | 764 мм | 40 | 4 | потайной замок |
| ALWT-1200х425-S-АА | 0.307 м² | 1200 мм | 1195 мм | 425 мм | 421 мм | 218 мм | 764 мм | 43 | 4 | потайной замок |
| ALWT-1200х450-S-АА | 0.325 м² | 1200 мм | 1195 мм | 450 мм | 446 мм | 218 мм | 764 мм | 45 | 4 | потайной замок |
| ALWT-1200х500-S-АА | 0.361 м² | 1200 мм | 1195 мм | 500 мм | 496 мм | 218 мм | 764 мм | 50 | 4 | потайной замок |
| ALWT-1200х525-S-АА | 0.379 м² | 1200 мм | 1195 мм | 525 мм | 521 мм | 218 мм | 764 мм | 53 | 4 | потайной замок |
| ALWT-1200х550-S-АА | 0.397 м² | 1200 мм | 1195 мм | 550 мм | 546 мм | 218 мм | 764 мм | 55 | 4 | потайной замок |
| ALWT-1200х600-S-АА | 0.433 м² | 1200 мм | 1195 мм | 600 мм | 596 мм | 218 мм | 764 мм | 60 | 4 | потайной замок |
| ALWT-1200х625-S-АА | 0.451 м² | 1200 мм | 1195 мм | 625 мм | 621 мм | 218 мм | 764 мм | 63 | 4 | потайной замок |
| ALWT-1200х650-S-АА | 0.469 м² | 1200 мм | 1195 мм | 650 мм | 646 мм | 218 мм | 764 мм | 65 | 4 | потайной замок |
| ALWT-1225х100-S-АА | 0.074 м² | 1225 мм | 1220 мм | 100 мм | 96 мм | 223 мм | 780 мм | 10 | 4 | потайной замок |
| ALWT-1225х125-S-АА | 0.092 м² | 1225 мм | 1220 мм | 125 мм | 121 мм | 223 мм | 780 мм | 13 | 4 | потайной замок |
| ALWT-1225х150-S-АА | 0.111 м² | 1225 мм | 1220 мм | 150 мм | 146 мм | 223 мм | 780 мм | 15 | 4 | потайной замок |
| ALWT-1225х200-S-АА | 0.147 м² | 1225 мм | 1220 мм | 200 мм | 196 мм | 223 мм | 780 мм | 20 | 4 | потайной замок |
| ALWT-1225х225-S-АА | 0.166 м² | 1225 мм | 1220 мм | 225 мм | 221 мм | 223 мм | 780 мм | 23 | 4 | потайной замок |
| ALWT-1225х250-S-АА | 0.184 м² | 1225 мм | 1220 мм | 250 мм | 246 мм | 223 мм | 780 мм | 25 | 4 | потайной замок |
| ALWT-1225х300-S-АА | 0.221 м² | 1225 мм | 1220 мм | 300 мм | 296 мм | 223 мм | 780 мм | 30 | 4 | потайной замок |
| ALWT-1225х325-S-АА | 0.240 м² | 1225 мм | 1220 мм | 325 мм | 321 мм | 223 мм | 780 мм | 33 | 4 | потайной замок |
| ALWT-1225х350-S-АА | 0.258 м² | 1225 мм | 1220 мм | 350 мм | 346 мм | 223 мм | 780 мм | 35 | 4 | потайной замок |
| ALWT-1225х400-S-АА | 0.295 м² | 1225 мм | 1220 мм | 400 мм | 396 мм | 223 мм | 780 мм | 40 | 4 | потайной замок |
| ALWT-1225х425-S-АА | 0.313 м² | 1225 мм | 1220 мм | 425 мм | 421 мм | 223 мм | 780 мм | 43 | 4 | потайной замок |
| ALWT-1225х450-S-АА | 0.332 м² | 1225 мм | 1220 мм | 450 мм | 446 мм | 223 мм | 780 мм | 45 | 4 | потайной замок |
| ALWT-1225х500-S-АА | 0.368 м² | 1225 мм | 1220 мм | 500 мм | 496 мм | 223 мм | 780 мм | 50 | 4 | потайной замок |
| ALWT-1225х525-S-АА | 0.387 м² | 1225 мм | 1220 мм | 525 мм | 521 мм | 223 мм | 780 мм | 53 | 4 | потайной замок |
| ALWT-1225х550-S-АА | 0.405 м² | 1225 мм | 1220 мм | 550 мм | 546 мм | 223 мм | 780 мм | 55 | 4 | потайной замок |
| ALWT-1225х600-S-АА | 0.442 м² | 1225 мм | 1220 мм | 600 мм | 596 мм | 223 мм | 780 мм | 60 | 4 | потайной замок |
| ALWT-1225х625-S-АА | 0.461 м² | 1225 мм | 1220 мм | 625 мм | 621 мм | 223 мм | 780 мм | 63 | 4 | потайной замок |
| ALWT-1225х650-S-АА | 0.479 м² | 1225 мм | 1220 мм | 650 мм | 646 мм | 223 мм | 780 мм | 65 | 4 | потайной замок |
| ALWT-1250х100-S-АА | 0.075 м² | 1250 мм | 1245 мм | 100 мм | 96 мм | 227 мм | 795 мм | 10 | 4 | потайной замок |
| ALWT-1250х125-S-АА | 0.094 м² | 1250 мм | 1245 мм | 125 мм | 121 мм | 227 мм | 795 мм | 13 | 4 | потайной замок |
| ALWT-1250х150-S-АА | 0.113 м² | 1250 мм | 1245 мм | 150 мм | 146 мм | 227 мм | 795 мм | 15 | 4 | потайной замок |
| ALWT-1250х200-S-АА | 0.150 м² | 1250 мм | 1245 мм | 200 мм | 196 мм | 227 мм | 795 мм | 20 | 4 | потайной замок |
| ALWT-1250х225-S-АА | 0.169 м² | 1250 мм | 1245 мм | 225 мм | 221 мм | 227 мм | 795 мм | 23 | 4 | потайной замок |
| ALWT-1250х250-S-АА | 0.188 м² | 1250 мм | 1245 мм | 250 мм | 246 мм | 227 мм | 795 мм | 25 | 4 | потайной замок |
| ALWT-1250х300-S-АА | 0.226 м² | 1250 мм | 1245 мм | 300 мм | 296 мм | 227 мм | 795 мм | 30 | 4 | потайной замок |
| ALWT-1250х325-S-АА | 0.244 м² | 1250 мм | 1245 мм | 325 мм | 321 мм | 227 мм | 795 мм | 33 | 4 | потайной замок |
| ALWT-1250х350-S-АА | 0.263 м² | 1250 мм | 1245 мм | 350 мм | 346 мм | 227 мм | 795 мм | 35 | 4 | потайной замок |
| ALWT-1250х400-S-АА | 0.301 м² | 1250 мм | 1245 мм | 400 мм | 396 мм | 227 мм | 795 мм | 40 | 4 | потайной замок |
| ALWT-1250х425-S-АА | 0.320 м² | 1250 мм | 1245 мм | 425 мм | 421 мм | 227 мм | 795 мм | 43 | 4 | потайной замок |
| ALWT-1250х450-S-АА | 0.338 м² | 1250 мм | 1245 мм | 450 мм | 446 мм | 227 мм | 795 мм | 45 | 4 | потайной замок |
| ALWT-1250х500-S-АА | 0.376 м² | 1250 мм | 1245 мм | 500 мм | 496 мм | 227 мм | 795 мм | 50 | 4 | потайной замок |
| ALWT-1250х525-S-АА | 0.395 м² | 1250 мм | 1245 мм | 525 мм | 521 мм | 227 мм | 795 мм | 53 | 4 | потайной замок |
| ALWT-1250х550-S-АА | 0.414 м² | 1250 мм | 1245 мм | 550 мм | 546 мм | 227 мм | 795 мм | 55 | 4 | потайной замок |
| ALWT-1250х600-S-АА | 0.451 м² | 1250 мм | 1245 мм | 600 мм | 596 мм | 227 мм | 795 мм | 60 | 4 | потайной замок |
| ALWT-1250х625-S-АА | 0.470 м² | 1250 мм | 1245 мм | 625 мм | 621 мм | 227 мм | 795 мм | 63 | 4 | потайной замок |
| ALWT-1250х650-S-АА | 0.489 м² | 1250 мм | 1245 мм | 650 мм | 646 мм | 227 мм | 795 мм | 65 | 4 | потайной замок |
| ALWT-1300х100-S-АА | 0.078 м² | 1300 мм | 1295 мм | 100 мм | 96 мм | 236 мм | 827 мм | 10 | 4 | потайной замок |
| ALWT-1300х125-S-АА | 0.098 м² | 1300 мм | 1295 мм | 125 мм | 121 мм | 236 мм | 827 мм | 13 | 4 | потайной замок |
| ALWT-1300х150-S-АА | 0.117 м² | 1300 мм | 1295 мм | 150 мм | 146 мм | 236 мм | 827 мм | 15 | 4 | потайной замок |
| ALWT-1300х200-S-АА | 0.156 м² | 1300 мм | 1295 мм | 200 мм | 196 мм | 236 мм | 827 мм | 20 | 4 | потайной замок |
| ALWT-1300х225-S-АА | 0.176 м² | 1300 мм | 1295 мм | 225 мм | 221 мм | 236 мм | 827 мм | 23 | 4 | потайной замок |
| ALWT-1300х250-S-АА | 0.196 м² | 1300 мм | 1295 мм | 250 мм | 246 мм | 236 мм | 827 мм | 25 | 4 | потайной замок |
| ALWT-1300х300-S-АА | 0.235 м² | 1300 мм | 1295 мм | 300 мм | 296 мм | 236 мм | 827 мм | 30 | 4 | потайной замок |
| ALWT-1300х325-S-АА | 0.254 м² | 1300 мм | 1295 мм | 325 мм | 321 мм | 236 мм | 827 мм | 33 | 4 | потайной замок |
| ALWT-1300х350-S-АА | 0.274 м² | 1300 мм | 1295 мм | 350 мм | 346 мм | 236 мм | 827 мм | 35 | 4 | потайной замок |
| ALWT-1300х400-S-АА | 0.313 м² | 1300 мм | 1295 мм | 400 мм | 396 мм | 236 мм | 827 мм | 40 | 4 | потайной замок |
| ALWT-1300х425-S-АА | 0.332 м² | 1300 мм | 1295 мм | 425 мм | 421 мм | 236 мм | 827 мм | 43 | 4 | потайной замок |
| ALWT-1300х450-S-АА | 0.352 м² | 1300 мм | 1295 мм | 450 мм | 446 мм | 236 мм | 827 мм | 45 | 4 | потайной замок |
| ALWT-1300х500-S-АА | 0.391 м² | 1300 мм | 1295 мм | 500 мм | 496 мм | 236 мм | 827 мм | 50 | 4 | потайной замок |
| ALWT-1300х525-S-АА | 0.411 м² | 1300 мм | 1295 мм | 525 мм | 521 мм | 236 мм | 827 мм | 53 | 4 | потайной замок |
| ALWT-1300х550-S-АА | 0.430 м² | 1300 мм | 1295 мм | 550 мм | 546 мм | 236 мм | 827 мм | 55 | 4 | потайной замок |
| ALWT-1300х600-S-АА | 0.469 м² | 1300 мм | 1295 мм | 600 мм | 596 мм | 236 мм | 827 мм | 60 | 4 | потайной замок |
| ALWT-1300х625-S-АА | 0.489 м² | 1300 мм | 1295 мм | 625 мм | 621 мм | 236 мм | 827 мм | 63 | 4 | потайной замок |
| ALWT-1300х650-S-АА | 0.508 м² | 1300 мм | 1295 мм | 650 мм | 646 мм | 236 мм | 827 мм | 65 | 4 | потайной замок |
| ALWT-1325х100-S-АА | 0.080 м² | 1325 мм | 1320 мм | 100 мм | 96 мм | 241 мм | 843 мм | 10 | 4 | потайной замок |
| ALWT-1325х125-S-АА | 0.100 м² | 1325 мм | 1320 мм | 125 мм | 121 мм | 241 мм | 843 мм | 13 | 4 | потайной замок |
| ALWT-1325х150-S-АА | 0.120 м² | 1325 мм | 1320 мм | 150 мм | 146 мм | 241 мм | 843 мм | 15 | 4 | потайной замок |
| ALWT-1325х200-S-АА | 0.159 м² | 1325 мм | 1320 мм | 200 мм | 196 мм | 241 мм | 843 мм | 20 | 4 | потайной замок |
| ALWT-1325х225-S-АА | 0.179 м² | 1325 мм | 1320 мм | 225 мм | 221 мм | 241 мм | 843 мм | 23 | 4 | потайной замок |
| ALWT-1325х250-S-АА | 0.199 м² | 1325 мм | 1320 мм | 250 мм | 246 мм | 241 мм | 843 мм | 25 | 4 | потайной замок |
| ALWT-1325х300-S-АА | 0.239 м² | 1325 мм | 1320 мм | 300 мм | 296 мм | 241 мм | 843 мм | 30 | 4 | потайной замок |
| ALWT-1325х325-S-АА | 0.259 м² | 1325 мм | 1320 мм | 325 мм | 321 мм | 241 мм | 843 мм | 33 | 4 | потайной замок |
| ALWT-1325х350-S-АА | 0.279 м² | 1325 мм | 1320 мм | 350 мм | 346 мм | 241 мм | 843 мм | 35 | 4 | потайной замок |
| ALWT-1325х400-S-АА | 0.319 м² | 1325 мм | 1320 мм | 400 мм | 396 мм | 241 мм | 843 мм | 40 | 4 | потайной замок |
| ALWT-1325х425-S-АА | 0.339 м² | 1325 мм | 1320 мм | 425 мм | 421 мм | 241 мм | 843 мм | 43 | 4 | потайной замок |
| ALWT-1325х450-S-АА | 0.359 м² | 1325 мм | 1320 мм | 450 мм | 446 мм | 241 мм | 843 мм | 45 | 4 | потайной замок |
| ALWT-1325х500-S-АА | 0.399 м² | 1325 мм | 1320 мм | 500 мм | 496 мм | 241 мм | 843 мм | 50 | 4 | потайной замок |
| ALWT-1325х525-S-АА | 0.418 м² | 1325 мм | 1320 мм | 525 мм | 521 мм | 241 мм | 843 мм | 53 | 4 | потайной замок |
| ALWT-1325х550-S-АА | 0.438 м² | 1325 мм | 1320 мм | 550 мм | 546 мм | 241 мм | 843 мм | 55 | 4 | потайной замок |
| ALWT-1325х600-S-АА | 0.478 м² | 1325 мм | 1320 мм | 600 мм | 596 мм | 241 мм | 843 мм | 60 | 4 | потайной замок |
| ALWT-1325х625-S-АА | 0.498 м² | 1325 мм | 1320 мм | 625 мм | 621 мм | 241 мм | 843 мм | 63 | 4 | потайной замок |
| ALWT-1325х650-S-АА | 0.518 м² | 1325 мм | 1320 мм | 650 мм | 646 мм | 241 мм | 843 мм | 65 | 4 | потайной замок |
| ALWT-1350х100-S-АА | 0.081 м² | 1350 мм | 1345 мм | 100 мм | 96 мм | 245 мм | 859 мм | 10 | 4 | потайной замок |
| ALWT-1350х125-S-АА | 0.102 м² | 1350 мм | 1345 мм | 125 мм | 121 мм | 245 мм | 859 мм | 13 | 4 | потайной замок |
| ALWT-1350х150-S-АА | 0.122 м² | 1350 мм | 1345 мм | 150 мм | 146 мм | 245 мм | 859 мм | 15 | 4 | потайной замок |
| ALWT-1350х200-S-АА | 0.162 м² | 1350 мм | 1345 мм | 200 мм | 196 мм | 245 мм | 859 мм | 20 | 4 | потайной замок |
| ALWT-1350х225-S-АА | 0.183 м² | 1350 мм | 1345 мм | 225 мм | 221 мм | 245 мм | 859 мм | 23 | 4 | потайной замок |
| ALWT-1350х250-S-АА | 0.203 м² | 1350 мм | 1345 мм | 250 мм | 246 мм | 245 мм | 859 мм | 25 | 4 | потайной замок |
| ALWT-1350х300-S-АА | 0.244 м² | 1350 мм | 1345 мм | 300 мм | 296 мм | 245 мм | 859 мм | 30 | 4 | потайной замок |
| ALWT-1350х325-S-АА | 0.264 м² | 1350 мм | 1345 мм | 325 мм | 321 мм | 245 мм | 859 мм | 33 | 4 | потайной замок |
| ALWT-1350х350-S-АА | 0.284 м² | 1350 мм | 1345 мм | 350 мм | 346 мм | 245 мм | 859 мм | 35 | 4 | потайной замок |
| ALWT-1350х400-S-АА | 0.325 м² | 1350 мм | 1345 мм | 400 мм | 396 мм | 245 мм | 859 мм | 40 | 4 | потайной замок |
| ALWT-1350х425-S-АА | 0.345 м² | 1350 мм | 1345 мм | 425 мм | 421 мм | 245 мм | 859 мм | 43 | 4 | потайной замок |
| ALWT-1350х450-S-АА | 0.365 м² | 1350 мм | 1345 мм | 450 мм | 446 мм | 245 мм | 859 мм | 45 | 4 | потайной замок |
| ALWT-1350х500-S-АА | 0.406 м² | 1350 мм | 1345 мм | 500 мм | 496 мм | 245 мм | 859 мм | 50 | 4 | потайной замок |
| ALWT-1350х525-S-АА | 0.426 м² | 1350 мм | 1345 мм | 525 мм | 521 мм | 245 мм | 859 мм | 53 | 4 | потайной замок |
| ALWT-1350х550-S-АА | 0.447 м² | 1350 мм | 1345 мм | 550 мм | 546 мм | 245 мм | 859 мм | 55 | 4 | потайной замок |
| ALWT-1350х600-S-АА | 0.487 м² | 1350 мм | 1345 мм | 600 мм | 596 мм | 245 мм | 859 мм | 60 | 4 | потайной замок |
| ALWT-1350х625-S-АА | 0.508 м² | 1350 мм | 1345 мм | 625 мм | 621 мм | 245 мм | 859 мм | 63 | 4 | потайной замок |
| ALWT-1350х650-S-АА | 0.528 м² | 1350 мм | 1345 мм | 650 мм | 646 мм | 245 мм | 859 мм | 65 | 4 | потайной замок |
| ALWT-1400х100-S-АА | 0.084 м² | 1400 мм | 1395 мм | 100 мм | 96 мм | 255 мм | 891 мм | 10 | 4 | потайной замок |
| ALWT-1400х125-S-АА | 0.105 м² | 1400 мм | 1395 мм | 125 мм | 121 мм | 255 мм | 891 мм | 13 | 4 | потайной замок |
| ALWT-1400х150-S-АА | 0.126 м² | 1400 мм | 1395 мм | 150 мм | 146 мм | 255 мм | 891 мм | 15 | 4 | потайной замок |
| ALWT-1400х200-S-АА | 0.168 м² | 1400 мм | 1395 мм | 200 мм | 196 мм | 255 мм | 891 мм | 20 | 4 | потайной замок |
| ALWT-1400х225-S-АА | 0.190 м² | 1400 мм | 1395 мм | 225 мм | 221 мм | 255 мм | 891 мм | 23 | 4 | потайной замок |
| ALWT-1400х250-S-АА | 0.211 м² | 1400 мм | 1395 мм | 250 мм | 246 мм | 255 мм | 891 мм | 25 | 4 | потайной замок |
| ALWT-1400х300-S-АА | 0.253 м² | 1400 мм | 1395 мм | 300 мм | 296 мм | 255 мм | 891 мм | 30 | 4 | потайной замок |
| ALWT-1400х325-S-АА | 0.274 м² | 1400 мм | 1395 мм | 325 мм | 321 мм | 255 мм | 891 мм | 33 | 4 | потайной замок |
| ALWT-1400х350-S-АА | 0.295 м² | 1400 мм | 1395 мм | 350 мм | 346 мм | 255 мм | 891 мм | 35 | 4 | потайной замок |
| ALWT-1400х400-S-АА | 0.337 м² | 1400 мм | 1395 мм | 400 мм | 396 мм | 255 мм | 891 мм | 40 | 4 | потайной замок |
| ALWT-1400х425-S-АА | 0.358 м² | 1400 мм | 1395 мм | 425 мм | 421 мм | 255 мм | 891 мм | 43 | 4 | потайной замок |
| ALWT-1400х450-S-АА | 0.379 м² | 1400 мм | 1395 мм | 450 мм | 446 мм | 255 мм | 891 мм | 45 | 4 | потайной замок |
| ALWT-1400х500-S-АА | 0.421 м² | 1400 мм | 1395 мм | 500 мм | 496 мм | 255 мм | 891 мм | 50 | 4 | потайной замок |
| ALWT-1400х525-S-АА | 0.442 м² | 1400 мм | 1395 мм | 525 мм | 521 мм | 255 мм | 891 мм | 53 | 4 | потайной замок |
| ALWT-1400х550-S-АА | 0.463 м² | 1400 мм | 1395 мм | 550 мм | 546 мм | 255 мм | 891 мм | 55 | 4 | потайной замок |
| ALWT-1400х600-S-АА | 0.505 м² | 1400 мм | 1395 мм | 600 мм | 596 мм | 255 мм | 891 мм | 60 | 4 | потайной замок |
| ALWT-1400х625-S-АА | 0.526 м² | 1400 мм | 1395 мм | 625 мм | 621 мм | 255 мм | 891 мм | 63 | 4 | потайной замок |
| ALWT-1400х650-S-АА | 0.547 м² | 1400 мм | 1395 мм | 650 мм | 646 мм | 255 мм | 891 мм | 65 | 4 | потайной замок |
| ALWT-1425х100-S-АА | 0.086 м² | 1425 мм | 1420 мм | 100 мм | 96 мм | 259 мм | 907 мм | 10 | 4 | потайной замок |
| ALWT-1425х125-S-АА | 0.107 м² | 1425 мм | 1420 мм | 125 мм | 121 мм | 259 мм | 907 мм | 13 | 4 | потайной замок |
| ALWT-1425х150-S-АА | 0.129 м² | 1425 мм | 1420 мм | 150 мм | 146 мм | 259 мм | 907 мм | 15 | 4 | потайной замок |
| ALWT-1425х200-S-АА | 0.171 м² | 1425 мм | 1420 мм | 200 мм | 196 мм | 259 мм | 907 мм | 20 | 4 | потайной замок |
| ALWT-1425х225-S-АА | 0.193 м² | 1425 мм | 1420 мм | 225 мм | 221 мм | 259 мм | 907 мм | 23 | 4 | потайной замок |
| ALWT-1425х250-S-АА | 0.214 м² | 1425 мм | 1420 мм | 250 мм | 246 мм | 259 мм | 907 мм | 25 | 4 | потайной замок |
| ALWT-1425х300-S-АА | 0.257 м² | 1425 мм | 1420 мм | 300 мм | 296 мм | 259 мм | 907 мм | 30 | 4 | потайной замок |
| ALWT-1425х325-S-АА | 0.279 м² | 1425 мм | 1420 мм | 325 мм | 321 мм | 259 мм | 907 мм | 33 | 4 | потайной замок |
| ALWT-1425х350-S-АА | 0.300 м² | 1425 мм | 1420 мм | 350 мм | 346 мм | 259 мм | 907 мм | 35 | 4 | потайной замок |
| ALWT-1425х400-S-АА | 0.343 м² | 1425 мм | 1420 мм | 400 мм | 396 мм | 259 мм | 907 мм | 40 | 4 | потайной замок |
| ALWT-1425х425-S-АА | 0.364 м² | 1425 мм | 1420 мм | 425 мм | 421 мм | 259 мм | 907 мм | 43 | 4 | потайной замок |
| ALWT-1425х450-S-АА | 0.386 м² | 1425 мм | 1420 мм | 450 мм | 446 мм | 259 мм | 907 мм | 45 | 4 | потайной замок |
| ALWT-1425х500-S-АА | 0.429 м² | 1425 мм | 1420 мм | 500 мм | 496 мм | 259 мм | 907 мм | 50 | 4 | потайной замок |
| ALWT-1425х525-S-АА | 0.450 м² | 1425 мм | 1420 мм | 525 мм | 521 мм | 259 мм | 907 мм | 53 | 4 | потайной замок |
| ALWT-1425х550-S-АА | 0.472 м² | 1425 мм | 1420 мм | 550 мм | 546 мм | 259 мм | 907 мм | 55 | 4 | потайной замок |
| ALWT-1425х600-S-АА | 0.514 м² | 1425 мм | 1420 мм | 600 мм | 596 мм | 259 мм | 907 мм | 60 | 4 | потайной замок |
| ALWT-1425х625-S-АА | 0.536 м² | 1425 мм | 1420 мм | 625 мм | 621 мм | 259 мм | 907 мм | 63 | 4 | потайной замок |
| ALWT-1425х650-S-АА | 0.557 м² | 1425 мм | 1420 мм | 650 мм | 646 мм | 259 мм | 907 мм | 65 | 4 | потайной замок |
| ALWT-1450х100-S-АА | 0.087 м² | 1450 мм | 1445 мм | 100 мм | 96 мм | 264 мм | 923 мм | 10 | 4 | потайной замок |
| ALWT-1450х125-S-АА | 0.109 м² | 1450 мм | 1445 мм | 125 мм | 121 мм | 264 мм | 923 мм | 13 | 4 | потайной замок |
| ALWT-1450х150-S-АА | 0.131 м² | 1450 мм | 1445 мм | 150 мм | 146 мм | 264 мм | 923 мм | 15 | 4 | потайной замок |
| ALWT-1450х200-S-АА | 0.174 м² | 1450 мм | 1445 мм | 200 мм | 196 мм | 264 мм | 923 мм | 20 | 4 | потайной замок |
| ALWT-1450х225-S-АА | 0.196 м² | 1450 мм | 1445 мм | 225 мм | 221 мм | 264 мм | 923 мм | 23 | 4 | потайной замок |
| ALWT-1450х250-S-АА | 0.218 м² | 1450 мм | 1445 мм | 250 мм | 246 мм | 264 мм | 923 мм | 25 | 4 | потайной замок |
| ALWT-1450х300-S-АА | 0.262 м² | 1450 мм | 1445 мм | 300 мм | 296 мм | 264 мм | 923 мм | 30 | 4 | потайной замок |
| ALWT-1450х325-S-АА | 0.284 м² | 1450 мм | 1445 мм | 325 мм | 321 мм | 264 мм | 923 мм | 33 | 4 | потайной замок |
| ALWT-1450х350-S-АА | 0.305 м² | 1450 мм | 1445 мм | 350 мм | 346 мм | 264 мм | 923 мм | 35 | 4 | потайной замок |
| ALWT-1450х400-S-АА | 0.349 м² | 1450 мм | 1445 мм | 400 мм | 396 мм | 264 мм | 923 мм | 40 | 4 | потайной замок |
| ALWT-1450х425-S-АА | 0.371 м² | 1450 мм | 1445 мм | 425 мм | 421 мм | 264 мм | 923 мм | 43 | 4 | потайной замок |
| ALWT-1450х450-S-АА | 0.393 м² | 1450 мм | 1445 мм | 450 мм | 446 мм | 264 мм | 923 мм | 45 | 4 | потайной замок |
| ALWT-1450х500-S-АА | 0.436 м² | 1450 мм | 1445 мм | 500 мм | 496 мм | 264 мм | 923 мм | 50 | 4 | потайной замок |
| ALWT-1450х525-S-АА | 0.458 м² | 1450 мм | 1445 мм | 525 мм | 521 мм | 264 мм | 923 мм | 53 | 4 | потайной замок |
| ALWT-1450х550-S-АА | 0.480 м² | 1450 мм | 1445 мм | 550 мм | 546 мм | 264 мм | 923 мм | 55 | 4 | потайной замок |
| ALWT-1450х600-S-АА | 0.523 м² | 1450 мм | 1445 мм | 600 мм | 596 мм | 264 мм | 923 мм | 60 | 4 | потайной замок |
| ALWT-1450х625-S-АА | 0.545 м² | 1450 мм | 1445 мм | 625 мм | 621 мм | 264 мм | 923 мм | 63 | 4 | потайной замок |
| ALWT-1450х650-S-АА | 0.567 м² | 1450 мм | 1445 мм | 650 мм | 646 мм | 264 мм | 923 мм | 65 | 4 | потайной замок |
| ALWT-1500х100-S-АА | 0.090 м² | 1500 мм | 1495 мм | 100 мм | 96 мм | 273 мм | 955 мм | 10 | 4 | потайной замок |
| ALWT-1500х125-S-АА | 0.113 м² | 1500 мм | 1495 мм | 125 мм | 121 мм | 273 мм | 955 мм | 13 | 4 | потайной замок |
| ALWT-1500х150-S-АА | 0.135 м² | 1500 мм | 1495 мм | 150 мм | 146 мм | 273 мм | 955 мм | 15 | 4 | потайной замок |
| ALWT-1500х200-S-АА | 0.180 м² | 1500 мм | 1495 мм | 200 мм | 196 мм | 273 мм | 955 мм | 20 | 4 | потайной замок |
| ALWT-1500х225-S-АА | 0.203 м² | 1500 мм | 1495 мм | 225 мм | 221 мм | 273 мм | 955 мм | 23 | 4 | потайной замок |
| ALWT-1500х250-S-АА | 0.226 м² | 1500 мм | 1495 мм | 250 мм | 246 мм | 273 мм | 955 мм | 25 | 4 | потайной замок |
| ALWT-1500х300-S-АА | 0.271 м² | 1500 мм | 1495 мм | 300 мм | 296 мм | 273 мм | 955 мм | 30 | 4 | потайной замок |
| ALWT-1500х325-S-АА | 0.293 м² | 1500 мм | 1495 мм | 325 мм | 321 мм | 273 мм | 955 мм | 33 | 4 | потайной замок |
| ALWT-1500х350-S-АА | 0.316 м² | 1500 мм | 1495 мм | 350 мм | 346 мм | 273 мм | 955 мм | 35 | 4 | потайной замок |
| ALWT-1500х400-S-АА | 0.361 м² | 1500 мм | 1495 мм | 400 мм | 396 мм | 273 мм | 955 мм | 40 | 4 | потайной замок |
| ALWT-1500х425-S-АА | 0.384 м² | 1500 мм | 1495 мм | 425 мм | 421 мм | 273 мм | 955 мм | 43 | 4 | потайной замок |
| ALWT-1500х450-S-АА | 0.406 м² | 1500 мм | 1495 мм | 450 мм | 446 мм | 273 мм | 955 мм | 45 | 4 | потайной замок |
| ALWT-1500х500-S-АА | 0.451 м² | 1500 мм | 1495 мм | 500 мм | 496 мм | 273 мм | 955 мм | 50 | 4 | потайной замок |
| ALWT-1500х525-S-АА | 0.474 м² | 1500 мм | 1495 мм | 525 мм | 521 мм | 273 мм | 955 мм | 53 | 4 | потайной замок |
| ALWT-1500х550-S-АА | 0.496 м² | 1500 мм | 1495 мм | 550 мм | 546 мм | 273 мм | 955 мм | 55 | 4 | потайной замок |
| ALWT-1500х600-S-АА | 0.541 м² | 1500 мм | 1495 мм | 600 мм | 596 мм | 273 мм | 955 мм | 60 | 4 | потайной замок |
| ALWT-1500х625-S-АА | 0.564 м² | 1500 мм | 1495 мм | 625 мм | 621 мм | 273 мм | 955 мм | 63 | 4 | потайной замок |
| ALWT-1500х650-S-АА | 0.587 м² | 1500 мм | 1495 мм | 650 мм | 646 мм | 273 мм | 955 мм | 65 | 4 | потайной замок |

note: column(s) folded — value = type name in every type: Комментарии к типоразмеру
